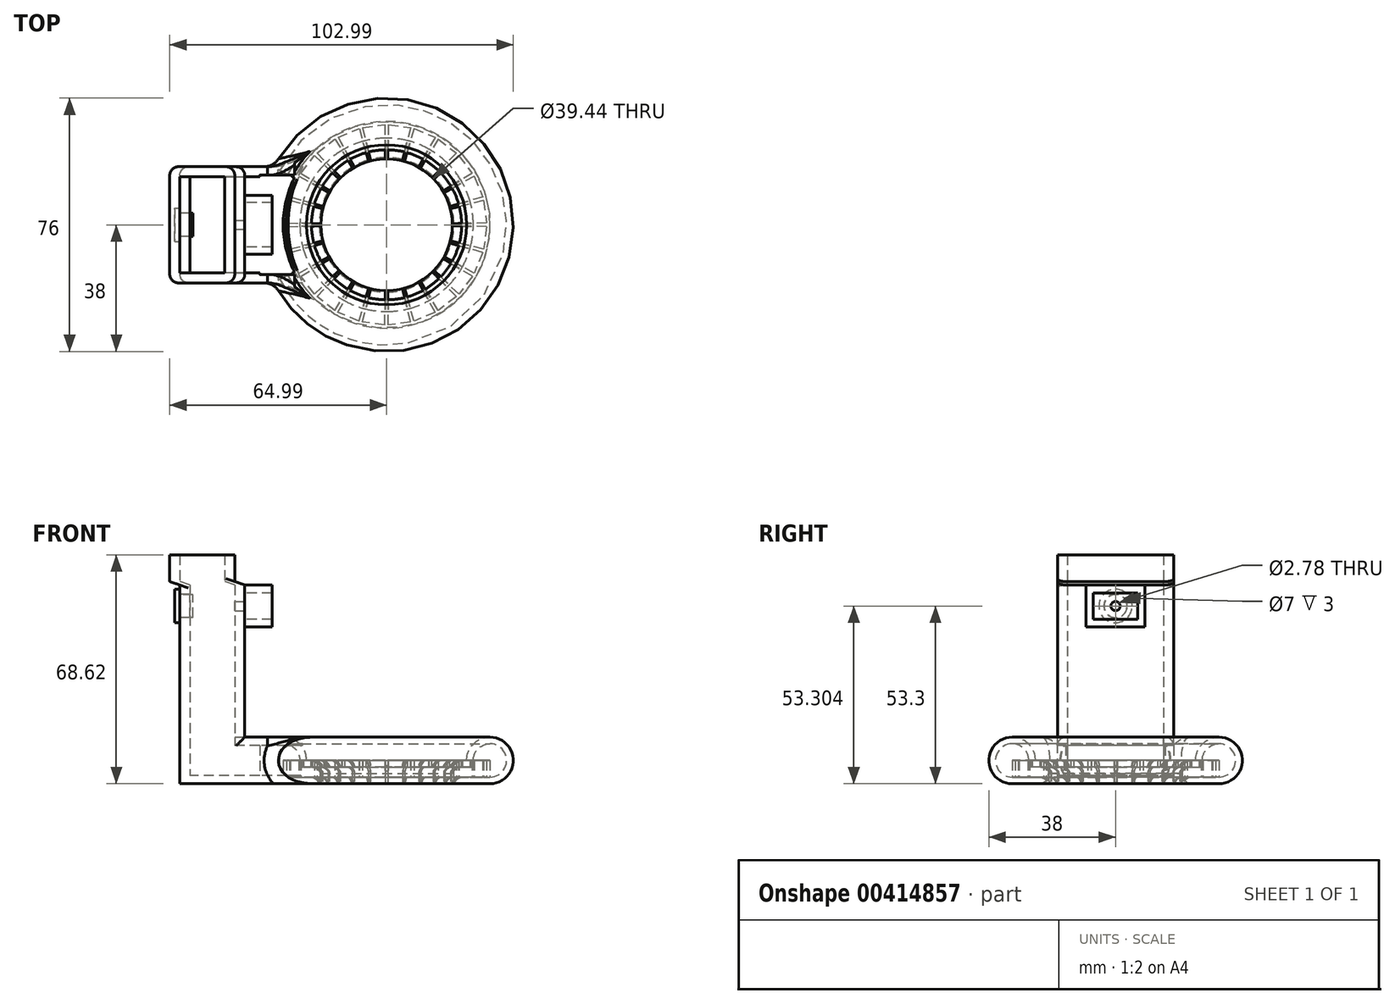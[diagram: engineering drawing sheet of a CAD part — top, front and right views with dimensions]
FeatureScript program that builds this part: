
annotation { "Feature Type Name" : "Feature", "Feature Type Description" : "" }
export const myFeature = defineFeature(function(context is Context, id is Id, definition is map)
    precondition{}
    {
        {
            var Q0;
            Q0=qCreatedBy(makeId("Right.planeOp"),FACE);
            cPlane(context, id + "F0", {"entities" : qUnion([Q0]), "cplaneType" : CPlaneType.OFFSET, "offset" : 42.5 * mm, "oppositeDirection" : true, "width" : 150 * mm, "height" : 150 * mm});
        }
        {
            var Q0;
            Q0=qCreatedBy(makeId("Front.planeOp"),FACE);
            cPlane(context, id + "F1", {"entities" : qUnion([Q0]), "cplaneType" : CPlaneType.OFFSET, "offset" : 17.41 * mm, "width" : 150 * mm, "height" : 150 * mm});
        }
        {
            var Q0;
            Q0=qCreatedBy(makeId("Front.planeOp"),FACE);
            cPlane(context, id + "F2", {"entities" : qUnion([Q0]), "cplaneType" : CPlaneType.OFFSET, "offset" : 17.41 * mm, "oppositeDirection" : true, "width" : 150 * mm, "height" : 150 * mm});
        }
        {
            var Q0;
            Q0=qCreatedBy(makeId("Top.planeOp"),FACE);
            cPlane(context, id + "F3", {"entities" : qUnion([Q0]), "cplaneType" : CPlaneType.OFFSET, "offset" : 7 * mm, "width" : 150 * mm, "height" : 150 * mm});
        }
        {
            var Q0;
            Q0=qCreatedBy(id+"F3.planeOp",FACE);
            cPlane(context, id + "F4", {"entities" : qUnion([Q0]), "cplaneType" : CPlaneType.OFFSET, "offset" : 6.95 * mm, "width" : 150 * mm, "height" : 150 * mm});
        }
        {
            var Q0;
            Q0=qCreatedBy(id+"F3.planeOp",FACE);
            cPlane(context, id + "F5", {"entities" : qUnion([Q0]), "cplaneType" : CPlaneType.OFFSET, "offset" : 52.62 * mm, "width" : 150 * mm, "height" : 150 * mm});
        }
        {
            var Q0;
            Q0=qCreatedBy(makeId("Right.planeOp"),FACE);
            cPlane(context, id + "F6", {"entities" : qUnion([Q0]), "cplaneType" : CPlaneType.OFFSET, "offset" : 62 * mm, "oppositeDirection" : true, "width" : 150 * mm, "height" : 150 * mm});
        }
        {
            var Q0;
            Q0=qCreatedBy(id+"F5.planeOp",FACE);
            cPlane(context, id + "F7", {"entities" : qUnion([Q0]), "cplaneType" : CPlaneType.OFFSET, "offset" : 1 * mm, "width" : 150 * mm, "height" : 150 * mm});
        }
        {
            var Q0;
            Q0=qCreatedBy(makeId("Top.planeOp"),FACE);
            var sketch = newSketch(context, id + "F8", { "sketchPlane" : qUnion([Q0])});
            skCircle(sketch, "E0", {"center": v(-293.13, 11) * mm, "radius": 45 * mm});
            skCircle(sketch, "E1.0", {"center": v(-293.13, 11) * mm, "radius": 38.5 * mm});
            skCircle(sketch, "E2", {"center": v(0, 0) * mm, "radius": 1.25 * mm, "construction": true});
            skLineSegment(sketch, "E3", {"start": v(-292.49, 47.5) * mm, "end": v(-292.6, 41) * mm});
            skLineSegment(sketch, "E4", {"start": v(-284.93, 39.86) * mm, "end": v(-283.16, 46.11) * mm});
            skLineSegment(sketch, "E5", {"start": v(-274.33, 42.29) * mm, "end": v(-277.67, 36.72) * mm});
            skLineSegment(sketch, "E6", {"start": v(-271.5, 31.8) * mm, "end": v(-266.82, 36.3) * mm});
            skLineSegment(sketch, "E7", {"start": v(-266.9, 25.56) * mm, "end": v(-261.21, 28.71) * mm});
            skLineSegment(sketch, "E8", {"start": v(-264.04, 18.33) * mm, "end": v(-257.73, 19.92) * mm});
            skLineSegment(sketch, "E9", {"start": v(-263.13, 10.5) * mm, "end": v(-256.63, 10.38) * mm});
            skLineSegment(sketch, "E10.MirrorCS", {"start": v(-264.3, 2.68) * mm, "end": v(-258.06, 0.88) * mm});
            skLineSegment(sketch, "E11.MirrorCS", {"start": v(-267.4, -4.44) * mm, "end": v(-261.83, -7.78) * mm});
            skLineSegment(sketch, "E12.MirrorCS", {"start": v(-272.22, -10.52) * mm, "end": v(-267.7, -15.18) * mm});
            skLineSegment(sketch, "E13.MirrorCS", {"start": v(-275.4, -20.9) * mm, "end": v(-278.55, -15.23) * mm});
            skLineSegment(sketch, "E14.MirrorCS", {"start": v(-285.92, -18.12) * mm, "end": v(-284.35, -24.43) * mm});
            skLineSegment(sketch, "E15.MirrorCS", {"start": v(-300.3, 40.13) * mm, "end": v(-301.87, 46.44) * mm});
            skLineSegment(sketch, "E16.MirrorCS", {"start": v(-310.82, 42.92) * mm, "end": v(-307.67, 37.25) * mm});
            skLineSegment(sketch, "E17.MirrorCS", {"start": v(-314.01, 32.54) * mm, "end": v(-318.54, 37.2) * mm});
            skLineSegment(sketch, "E18.MirrorCS", {"start": v(-318.83, 26.46) * mm, "end": v(-324.4, 29.81) * mm});
            skLineSegment(sketch, "E19.MirrorCS", {"start": v(-321.94, 19.34) * mm, "end": v(-328.19, 21.15) * mm});
            skLineSegment(sketch, "E20.MirrorCS", {"start": v(-322.22, 3.7) * mm, "end": v(-328.53, 2.11) * mm});
            skLineSegment(sketch, "E21.MirrorCS", {"start": v(-319.37, -3.53) * mm, "end": v(-325.06, -6.68) * mm});
            skLineSegment(sketch, "E22.MirrorCS", {"start": v(-314.77, -9.77) * mm, "end": v(-319.46, -14.28) * mm});
            skLineSegment(sketch, "E23.MirrorCS", {"start": v(-311.95, -20.27) * mm, "end": v(-308.6, -14.7) * mm});
            skLineSegment(sketch, "E24.MirrorCS", {"start": v(-301.35, -17.85) * mm, "end": v(-303.13, -24.1) * mm});
            skLineSegment(sketch, "E25", {"start": v(-293.65, -19) * mm, "end": v(-293.76, -25.5) * mm});
            skLineSegment(sketch, "E26", {"start": v(-323.12, 11.52) * mm, "end": v(-329.62, 11.64) * mm});
            skLineSegment(sketch, "E27", {"start": v(-293.76, 47.5) * mm, "end": v(-293.65, 41) * mm});
            skLineSegment(sketch, "E28", {"start": v(-285.94, 40.13) * mm, "end": v(-284.39, 46.44) * mm});
            skLineSegment(sketch, "E29", {"start": v(-275.43, 42.92) * mm, "end": v(-278.58, 37.25) * mm});
            skLineSegment(sketch, "E30", {"start": v(-272.24, 32.54) * mm, "end": v(-267.72, 37.2) * mm});
            skLineSegment(sketch, "E31", {"start": v(-267.42, 26.46) * mm, "end": v(-261.85, 29.81) * mm});
            skLineSegment(sketch, "E32", {"start": v(-264.3, 19.34) * mm, "end": v(-258.07, 21.15) * mm});
            skLineSegment(sketch, "E33", {"start": v(-263.13, 11.54) * mm, "end": v(-256.63, 11.65) * mm});
            skLineSegment(sketch, "E34.MirrorCS", {"start": v(-264.03, 3.7) * mm, "end": v(-257.73, 2.11) * mm});
            skLineSegment(sketch, "E35.MirrorCS", {"start": v(-266.88, -3.53) * mm, "end": v(-261.2, -6.68) * mm});
            skLineSegment(sketch, "E36.MirrorCS", {"start": v(-271.48, -9.77) * mm, "end": v(-266.8, -14.28) * mm});
            skLineSegment(sketch, "E37.MirrorCS", {"start": v(-274.3, -20.27) * mm, "end": v(-277.65, -14.7) * mm});
            skLineSegment(sketch, "E38.MirrorCS", {"start": v(-284.9, -17.85) * mm, "end": v(-283.12, -24.1) * mm});
            skLineSegment(sketch, "E39.MirrorCS", {"start": v(-301.32, 39.86) * mm, "end": v(-303.1, 46.11) * mm});
            skLineSegment(sketch, "E40.MirrorCS", {"start": v(-311.93, 42.29) * mm, "end": v(-308.58, 36.72) * mm});
            skLineSegment(sketch, "E41.MirrorCS", {"start": v(-314.75, 31.8) * mm, "end": v(-319.44, 36.3) * mm});
            skLineSegment(sketch, "E42.MirrorCS", {"start": v(-319.36, 25.56) * mm, "end": v(-325.04, 28.71) * mm});
            skLineSegment(sketch, "E43.MirrorCS", {"start": v(-322.22, 18.33) * mm, "end": v(-328.52, 19.92) * mm});
            skLineSegment(sketch, "E44.MirrorCS", {"start": v(-321.95, 2.68) * mm, "end": v(-328.2, 0.88) * mm});
            skLineSegment(sketch, "E45.MirrorCS", {"start": v(-318.85, -4.44) * mm, "end": v(-324.42, -7.78) * mm});
            skLineSegment(sketch, "E46.MirrorCS", {"start": v(-314.03, -10.52) * mm, "end": v(-318.56, -15.18) * mm});
            skLineSegment(sketch, "E47.MirrorCS", {"start": v(-310.85, -20.9) * mm, "end": v(-307.7, -15.23) * mm});
            skLineSegment(sketch, "E48.MirrorCS", {"start": v(-300.34, -18.12) * mm, "end": v(-301.9, -24.43) * mm});
            skLineSegment(sketch, "E49", {"start": v(-292.6, -19) * mm, "end": v(-292.49, -25.5) * mm});
            skLineSegment(sketch, "E50", {"start": v(-323.12, 10.48) * mm, "end": v(-329.62, 10.36) * mm});
            skCircle(sketch, "E51", {"center": v(-293.13, 11) * mm, "radius": 1.25 * mm, "construction": true});
            skLineSegment(sketch, "E52", {"start": v(-322.22, 18.33) * mm, "end": v(-321.94, 19.34) * mm});
            skLineSegment(sketch, "E53", {"start": v(-321.94, 19.34) * mm, "end": v(-319.36, 25.56) * mm});
            skLineSegment(sketch, "E54", {"start": v(-319.36, 25.56) * mm, "end": v(-318.83, 26.46) * mm});
            skLineSegment(sketch, "E55", {"start": v(-318.83, 26.46) * mm, "end": v(-314.75, 31.8) * mm});
            skLineSegment(sketch, "E56", {"start": v(-314.75, 31.8) * mm, "end": v(-314.01, 32.54) * mm});
            skLineSegment(sketch, "E57", {"start": v(-314.01, 32.54) * mm, "end": v(-308.58, 36.72) * mm});
            skLineSegment(sketch, "E58", {"start": v(-308.58, 36.72) * mm, "end": v(-307.67, 37.25) * mm});
            skLineSegment(sketch, "E59", {"start": v(-307.67, 37.25) * mm, "end": v(-301.32, 39.86) * mm});
            skLineSegment(sketch, "E60", {"start": v(-301.32, 39.86) * mm, "end": v(-300.3, 40.13) * mm});
            skLineSegment(sketch, "E61", {"start": v(-300.3, 40.13) * mm, "end": v(-293.65, 41) * mm});
            skLineSegment(sketch, "E62", {"start": v(-293.65, 41) * mm, "end": v(-292.6, 41) * mm});
            skLineSegment(sketch, "E63", {"start": v(-292.6, 41) * mm, "end": v(-285.94, 40.13) * mm});
            skLineSegment(sketch, "E64", {"start": v(-285.94, 40.13) * mm, "end": v(-284.93, 39.86) * mm});
            skLineSegment(sketch, "E65", {"start": v(-284.93, 39.86) * mm, "end": v(-278.58, 37.25) * mm});
            skLineSegment(sketch, "E66", {"start": v(-278.58, 37.25) * mm, "end": v(-277.67, 36.72) * mm});
            skLineSegment(sketch, "E67", {"start": v(-277.67, 36.72) * mm, "end": v(-272.24, 32.54) * mm});
            skLineSegment(sketch, "E68", {"start": v(-272.24, 32.54) * mm, "end": v(-271.5, 31.8) * mm});
            skLineSegment(sketch, "E69", {"start": v(-271.5, 31.8) * mm, "end": v(-267.42, 26.46) * mm});
            skLineSegment(sketch, "E70", {"start": v(-267.42, 26.46) * mm, "end": v(-266.9, 25.56) * mm});
            skLineSegment(sketch, "E71", {"start": v(-266.9, 25.56) * mm, "end": v(-264.3, 19.34) * mm});
            skLineSegment(sketch, "E72", {"start": v(-264.3, 19.34) * mm, "end": v(-264.04, 18.33) * mm});
            skLineSegment(sketch, "E73", {"start": v(-264.04, 18.33) * mm, "end": v(-263.13, 11.54) * mm});
            skLineSegment(sketch, "E74", {"start": v(-263.13, 11.54) * mm, "end": v(-263.13, 10.5) * mm});
            skLineSegment(sketch, "E75", {"start": v(-263.13, 10.5) * mm, "end": v(-264.03, 3.7) * mm});
            skLineSegment(sketch, "E76", {"start": v(-264.03, 3.7) * mm, "end": v(-264.3, 2.68) * mm});
            skLineSegment(sketch, "E77", {"start": v(-264.3, 2.68) * mm, "end": v(-266.88, -3.53) * mm});
            skLineSegment(sketch, "E78", {"start": v(-266.88, -3.53) * mm, "end": v(-267.4, -4.44) * mm});
            skLineSegment(sketch, "E79", {"start": v(-267.4, -4.44) * mm, "end": v(-271.48, -9.77) * mm});
            skLineSegment(sketch, "E80", {"start": v(-271.48, -9.77) * mm, "end": v(-272.22, -10.52) * mm});
            skLineSegment(sketch, "E81", {"start": v(-272.22, -10.52) * mm, "end": v(-277.65, -14.7) * mm});
            skLineSegment(sketch, "E82", {"start": v(-277.65, -14.7) * mm, "end": v(-278.55, -15.23) * mm});
            skLineSegment(sketch, "E83", {"start": v(-278.55, -15.23) * mm, "end": v(-284.9, -17.85) * mm});
            skLineSegment(sketch, "E84", {"start": v(-284.9, -17.85) * mm, "end": v(-285.92, -18.12) * mm});
            skLineSegment(sketch, "E85", {"start": v(-285.92, -18.12) * mm, "end": v(-292.6, -19) * mm});
            skLineSegment(sketch, "E86", {"start": v(-292.6, -19) * mm, "end": v(-293.65, -19) * mm});
            skLineSegment(sketch, "E87", {"start": v(-293.65, -19) * mm, "end": v(-300.34, -18.12) * mm});
            skLineSegment(sketch, "E88", {"start": v(-300.34, -18.12) * mm, "end": v(-301.35, -17.85) * mm});
            skLineSegment(sketch, "E89", {"start": v(-301.35, -17.85) * mm, "end": v(-307.7, -15.23) * mm});
            skLineSegment(sketch, "E90", {"start": v(-307.7, -15.23) * mm, "end": v(-308.6, -14.7) * mm});
            skLineSegment(sketch, "E91", {"start": v(-308.6, -14.7) * mm, "end": v(-314.03, -10.52) * mm});
            skLineSegment(sketch, "E92", {"start": v(-314.03, -10.52) * mm, "end": v(-314.77, -9.77) * mm});
            skLineSegment(sketch, "E93", {"start": v(-314.77, -9.77) * mm, "end": v(-318.85, -4.44) * mm});
            skLineSegment(sketch, "E94", {"start": v(-318.85, -4.44) * mm, "end": v(-319.37, -3.53) * mm});
            skLineSegment(sketch, "E95", {"start": v(-321.95, 2.68) * mm, "end": v(-322.22, 3.7) * mm});
            skLineSegment(sketch, "E96", {"start": v(-319.37, -3.53) * mm, "end": v(-321.95, 2.68) * mm});
            skLineSegment(sketch, "E97", {"start": v(-322.22, 3.7) * mm, "end": v(-323.12, 10.48) * mm});
            skLineSegment(sketch, "E98", {"start": v(-323.12, 10.48) * mm, "end": v(-323.12, 11.52) * mm});
            skLineSegment(sketch, "E99", {"start": v(-323.12, 11.52) * mm, "end": v(-322.22, 18.33) * mm});
            skLineSegment(sketch, "E100", {"start": v(-329.62, 11.64) * mm, "end": v(-328.52, 19.92) * mm});
            skLineSegment(sketch, "E101", {"start": v(-328.19, 21.15) * mm, "end": v(-325.04, 28.71) * mm});
            skLineSegment(sketch, "E102", {"start": v(-324.4, 29.81) * mm, "end": v(-319.44, 36.3) * mm});
            skLineSegment(sketch, "E103", {"start": v(-318.54, 37.2) * mm, "end": v(-311.93, 42.29) * mm});
            skLineSegment(sketch, "E104", {"start": v(-310.82, 42.92) * mm, "end": v(-303.1, 46.11) * mm});
            skLineSegment(sketch, "E105", {"start": v(-301.87, 46.44) * mm, "end": v(-293.76, 47.5) * mm});
            skLineSegment(sketch, "E106", {"start": v(-292.49, 47.5) * mm, "end": v(-284.39, 46.44) * mm});
            skLineSegment(sketch, "E107", {"start": v(-283.16, 46.11) * mm, "end": v(-275.43, 42.92) * mm});
            skLineSegment(sketch, "E108", {"start": v(-274.33, 42.29) * mm, "end": v(-267.72, 37.2) * mm});
            skLineSegment(sketch, "E109", {"start": v(-266.82, 36.3) * mm, "end": v(-261.85, 29.81) * mm});
            skLineSegment(sketch, "E110", {"start": v(-261.21, 28.71) * mm, "end": v(-258.07, 21.15) * mm});
            skLineSegment(sketch, "E111", {"start": v(-257.73, 19.92) * mm, "end": v(-256.63, 11.65) * mm});
            skLineSegment(sketch, "E112", {"start": v(-256.63, 10.38) * mm, "end": v(-257.73, 2.11) * mm});
            skLineSegment(sketch, "E113", {"start": v(-258.06, 0.88) * mm, "end": v(-261.2, -6.68) * mm});
            skLineSegment(sketch, "E114", {"start": v(-261.83, -7.78) * mm, "end": v(-266.8, -14.28) * mm});
            skLineSegment(sketch, "E115", {"start": v(-267.7, -15.18) * mm, "end": v(-274.3, -20.27) * mm});
            skLineSegment(sketch, "E116", {"start": v(-275.4, -20.9) * mm, "end": v(-283.12, -24.1) * mm});
            skLineSegment(sketch, "E117", {"start": v(-284.35, -24.43) * mm, "end": v(-292.49, -25.5) * mm});
            skLineSegment(sketch, "E118", {"start": v(-293.76, -25.5) * mm, "end": v(-301.9, -24.43) * mm});
            skLineSegment(sketch, "E119", {"start": v(-303.13, -24.1) * mm, "end": v(-310.85, -20.9) * mm});
            skLineSegment(sketch, "E120", {"start": v(-311.95, -20.27) * mm, "end": v(-318.56, -15.18) * mm});
            skLineSegment(sketch, "E121", {"start": v(-319.46, -14.28) * mm, "end": v(-324.42, -7.78) * mm});
            skLineSegment(sketch, "E122", {"start": v(-325.06, -6.68) * mm, "end": v(-328.2, 0.88) * mm});
            skLineSegment(sketch, "E123", {"start": v(-328.53, 2.11) * mm, "end": v(-329.62, 10.36) * mm});
            skCircle(sketch, "E124", {"center": v(0, 0) * mm, "radius": 20 * mm});
            skLineSegment(sketch, "E125", {"start": v(8.2, 28.86) * mm, "end": v(5.46, 19.24) * mm});
            skLineSegment(sketch, "E126", {"start": v(15.46, 25.72) * mm, "end": v(10.3, 17.15) * mm});
            skLineSegment(sketch, "E127", {"start": v(21.62, 20.8) * mm, "end": v(14.41, 13.87) * mm});
            skLineSegment(sketch, "E128", {"start": v(26.23, 14.56) * mm, "end": v(17.49, 9.7) * mm});
            skLineSegment(sketch, "E129", {"start": v(29.1, 7.33) * mm, "end": v(19.4, 4.9) * mm});
            skLineSegment(sketch, "E130", {"start": v(30, -0.5) * mm, "end": v(20, -0.34) * mm});
            skLineSegment(sketch, "E131", {"start": v(28.82, -8.32) * mm, "end": v(19.22, -5.54) * mm});
            skLineSegment(sketch, "E132", {"start": v(25.72, -15.44) * mm, "end": v(17.15, -10.29) * mm});
            skLineSegment(sketch, "E133", {"start": v(20.9, -21.52) * mm, "end": v(13.94, -14.34) * mm});
            skLineSegment(sketch, "E134", {"start": v(14.57, -26.23) * mm, "end": v(9.72, -17.48) * mm});
            skLineSegment(sketch, "E135", {"start": v(7.21, -29.12) * mm, "end": v(4.81, -19.41) * mm});
            skLineSegment(sketch, "E136", {"start": v(-0.52, -30) * mm, "end": v(-0.35, -20) * mm});
            skLineSegment(sketch, "E137.MirrorCS", {"start": v(-7.18, 29.13) * mm, "end": v(-4.78, 19.42) * mm});
            skLineSegment(sketch, "E138.MirrorCS", {"start": v(-14.55, 26.25) * mm, "end": v(-9.7, 17.5) * mm});
            skLineSegment(sketch, "E139.MirrorCS", {"start": v(-20.88, 21.54) * mm, "end": v(-13.92, 14.36) * mm});
            skLineSegment(sketch, "E140.MirrorCS", {"start": v(-25.7, 15.46) * mm, "end": v(-17.14, 10.31) * mm});
            skLineSegment(sketch, "E141.MirrorCS", {"start": v(-28.82, 8.34) * mm, "end": v(-19.2, 5.57) * mm});
            skLineSegment(sketch, "E142.MirrorCS", {"start": v(-29.1, -7.3) * mm, "end": v(-19.4, -4.87) * mm});
            skLineSegment(sketch, "E143.MirrorCS", {"start": v(-26.25, -14.53) * mm, "end": v(-17.5, -9.68) * mm});
            skLineSegment(sketch, "E144.MirrorCS", {"start": v(-21.64, -20.77) * mm, "end": v(-14.43, -13.85) * mm});
            skLineSegment(sketch, "E145.MirrorCS", {"start": v(-15.48, -25.7) * mm, "end": v(-10.32, -17.13) * mm});
            skLineSegment(sketch, "E146.MirrorCS", {"start": v(-8.22, -28.85) * mm, "end": v(-5.49, -19.23) * mm});
            skLineSegment(sketch, "E147", {"start": v(-30, 0.52) * mm, "end": v(-20, 0.35) * mm});
            skLineSegment(sketch, "E148", {"start": v(0.52, 30) * mm, "end": v(0.35, 20) * mm});
            skLineSegment(sketch, "E149", {"start": v(7.18, 29.13) * mm, "end": v(4.78, 19.42) * mm});
            skLineSegment(sketch, "E150", {"start": v(14.55, 26.25) * mm, "end": v(9.7, 17.5) * mm});
            skLineSegment(sketch, "E151", {"start": v(20.88, 21.54) * mm, "end": v(13.92, 14.36) * mm});
            skLineSegment(sketch, "E152", {"start": v(25.7, 15.46) * mm, "end": v(17.14, 10.31) * mm});
            skLineSegment(sketch, "E153", {"start": v(28.82, 8.34) * mm, "end": v(19.2, 5.57) * mm});
            skLineSegment(sketch, "E154", {"start": v(30, 0.54) * mm, "end": v(20, 0.36) * mm});
            skLineSegment(sketch, "E155", {"start": v(29.1, -7.3) * mm, "end": v(19.4, -4.87) * mm});
            skLineSegment(sketch, "E156", {"start": v(26.25, -14.53) * mm, "end": v(17.5, -9.68) * mm});
            skLineSegment(sketch, "E157", {"start": v(21.64, -20.77) * mm, "end": v(14.43, -13.85) * mm});
            skLineSegment(sketch, "E158", {"start": v(15.48, -25.7) * mm, "end": v(10.32, -17.13) * mm});
            skLineSegment(sketch, "E159", {"start": v(8.22, -28.85) * mm, "end": v(5.49, -19.23) * mm});
            skLineSegment(sketch, "E160", {"start": v(0.52, -30) * mm, "end": v(0.35, -20) * mm});
            skLineSegment(sketch, "E161.MirrorCS", {"start": v(-8.2, 28.86) * mm, "end": v(-5.46, 19.24) * mm});
            skLineSegment(sketch, "E162.MirrorCS", {"start": v(-15.46, 25.72) * mm, "end": v(-10.3, 17.15) * mm});
            skLineSegment(sketch, "E163.MirrorCS", {"start": v(-21.62, 20.8) * mm, "end": v(-14.41, 13.87) * mm});
            skLineSegment(sketch, "E164.MirrorCS", {"start": v(-26.23, 14.56) * mm, "end": v(-17.49, 9.7) * mm});
            skLineSegment(sketch, "E165.MirrorCS", {"start": v(-29.1, 7.33) * mm, "end": v(-19.4, 4.9) * mm});
            skLineSegment(sketch, "E166.MirrorCS", {"start": v(-28.82, -8.32) * mm, "end": v(-19.22, -5.54) * mm});
            skLineSegment(sketch, "E167.MirrorCS", {"start": v(-25.72, -15.44) * mm, "end": v(-17.15, -10.29) * mm});
            skLineSegment(sketch, "E168.MirrorCS", {"start": v(-20.9, -21.52) * mm, "end": v(-13.94, -14.34) * mm});
            skLineSegment(sketch, "E169.MirrorCS", {"start": v(-14.57, -26.23) * mm, "end": v(-9.72, -17.48) * mm});
            skLineSegment(sketch, "E170.MirrorCS", {"start": v(-7.21, -29.12) * mm, "end": v(-4.81, -19.41) * mm});
            skLineSegment(sketch, "E171", {"start": v(-30, -0.52) * mm, "end": v(-20, -0.35) * mm});
            skLineSegment(sketch, "E172", {"start": v(-0.52, 30) * mm, "end": v(-0.35, 20) * mm});
            skLineSegment(sketch, "E173", {"start": v(-14.55, 26.25) * mm, "end": v(-8.2, 28.86) * mm});
            skLineSegment(sketch, "E174", {"start": v(-7.18, 29.13) * mm, "end": v(-0.52, 30) * mm});
            skLineSegment(sketch, "E175", {"start": v(0.52, 30) * mm, "end": v(7.18, 29.13) * mm});
            skLineSegment(sketch, "E176", {"start": v(8.2, 28.86) * mm, "end": v(14.55, 26.25) * mm});
            skLineSegment(sketch, "E177", {"start": v(15.46, 25.72) * mm, "end": v(20.88, 21.54) * mm});
            skLineSegment(sketch, "E178", {"start": v(21.62, 20.8) * mm, "end": v(25.7, 15.46) * mm});
            skLineSegment(sketch, "E179", {"start": v(26.23, 14.56) * mm, "end": v(28.82, 8.34) * mm});
            skLineSegment(sketch, "E180", {"start": v(29.1, 7.33) * mm, "end": v(30, 0.54) * mm});
            skLineSegment(sketch, "E181", {"start": v(30, -0.5) * mm, "end": v(29.1, -7.3) * mm});
            skLineSegment(sketch, "E182", {"start": v(28.82, -8.32) * mm, "end": v(26.25, -14.53) * mm});
            skLineSegment(sketch, "E183", {"start": v(25.72, -15.44) * mm, "end": v(21.64, -20.77) * mm});
            skLineSegment(sketch, "E184", {"start": v(20.9, -21.52) * mm, "end": v(15.48, -25.7) * mm});
            skLineSegment(sketch, "E185", {"start": v(14.57, -26.23) * mm, "end": v(8.22, -28.85) * mm});
            skLineSegment(sketch, "E186", {"start": v(7.21, -29.12) * mm, "end": v(0.52, -30) * mm});
            skLineSegment(sketch, "E187", {"start": v(-0.52, -30) * mm, "end": v(-7.21, -29.12) * mm});
            skLineSegment(sketch, "E188", {"start": v(-8.22, -28.85) * mm, "end": v(-14.57, -26.23) * mm});
            skLineSegment(sketch, "E189", {"start": v(-15.48, -25.7) * mm, "end": v(-20.9, -21.52) * mm});
            skLineSegment(sketch, "E190", {"start": v(-21.64, -20.77) * mm, "end": v(-25.72, -15.44) * mm});
            skLineSegment(sketch, "E191", {"start": v(-26.25, -14.53) * mm, "end": v(-28.82, -8.32) * mm});
            skLineSegment(sketch, "E192", {"start": v(-29.1, -7.3) * mm, "end": v(-30, -0.52) * mm});
            skLineSegment(sketch, "E193", {"start": v(-28.82, 8.34) * mm, "end": v(-26.23, 14.56) * mm});
            skLineSegment(sketch, "E194", {"start": v(-25.7, 15.46) * mm, "end": v(-21.62, 20.8) * mm});
            skLineSegment(sketch, "E195", {"start": v(-30, 0.52) * mm, "end": v(-29.1, 7.33) * mm});
            skLineSegment(sketch, "E196", {"start": v(-20.88, 21.54) * mm, "end": v(-15.46, 25.72) * mm});
            skCircle(sketch, "E197", {"center": v(0, 0) * mm, "radius": 31 * mm});
            skCircle(sketch, "E198", {"center": v(0, 0) * mm, "radius": 37.5 * mm});
            skSolve(sketch);
        }
        {
            var Q0;
            Q0=qCreatedBy(makeId("Front.planeOp"),FACE);
            var sketch = newSketch(context, id + "F9", { "sketchPlane" : qUnion([Q0])});
            skLineSegment(sketch, "E199.top", {"start": v(38.5, -7) * mm, "end": v(-38.5, -7) * mm, "construction": true});
            skLineSegment(sketch, "E199.left", {"start": v(31, 7) * mm, "end": v(31, -7) * mm, "construction": true});
            skPoint(sketch, "E199.middle", {"position": v(0, 0) * mm});
            skLineSegment(sketch, "E200", {"start": v(-38.5, 0) * mm, "end": v(38.5, 0) * mm, "construction": true});
            skArc(sketch, "E201", {"start": v(31, 0) * mm, "mid": v(35.95, 11.95) * mm, "end": v(24, 7) * mm});
            skArc(sketch, "E202", {"start": v(31, 2) * mm, "mid": v(34.53, 10.54) * mm, "end": v(26, 7) * mm});
            skLineSegment(sketch, "E203", {"start": v(31, 2) * mm, "end": v(31, 0) * mm});
            skLineSegment(sketch, "E204", {"start": v(31, 2) * mm, "end": v(24, 2) * mm, "construction": true});
            skLineSegment(sketch, "E205", {"start": v(24, 2) * mm, "end": v(24, 0) * mm, "construction": true});
            skLineSegment(sketch, "E206", {"start": v(22.5, 0) * mm, "end": v(22.5, 7) * mm, "construction": true});
            skLineSegment(sketch, "E207", {"start": v(24, 7) * mm, "end": v(22.5, 7) * mm});
            skLineSegment(sketch, "E208", {"start": v(30, 7) * mm, "end": v(30, 5) * mm});
            skLineSegment(sketch, "E209", {"start": v(22.5, 5) * mm, "end": v(26, 5) * mm});
            skLineSegment(sketch, "E210", {"start": v(26, 5) * mm, "end": v(26, 7) * mm});
            skLineSegment(sketch, "E211", {"start": v(0, -7) * mm, "end": v(0, 7) * mm, "construction": true});
            skLineSegment(sketch, "E212", {"start": v(31, 7) * mm, "end": v(31, 14) * mm, "construction": true});
            skLineSegment(sketch, "E213", {"start": v(31, 7) * mm, "end": v(38, 7) * mm, "construction": true});
            skLineSegment(sketch, "E214", {"start": v(31, 12) * mm, "end": v(31, 14) * mm});
            skLineSegment(sketch, "E215", {"start": v(36, 7) * mm, "end": v(38, 7) * mm});
            skLineSegment(sketch, "E216.MirrorCS", {"start": v(-31, 2) * mm, "end": v(-31, 0) * mm});
            skLineSegment(sketch, "E217.MirrorCS", {"start": v(-30, 7) * mm, "end": v(-30, 5) * mm});
            skLineSegment(sketch, "E218.MirrorCS", {"start": v(-24, 7) * mm, "end": v(-22.5, 7) * mm});
            skLineSegment(sketch, "E219.MirrorCS", {"start": v(-26, 5) * mm, "end": v(-26, 7) * mm});
            skLineSegment(sketch, "E220.MirrorCS", {"start": v(-36, 7) * mm, "end": v(-38, 7) * mm});
            skLineSegment(sketch, "E221.MirrorCS", {"start": v(-22.5, 5) * mm, "end": v(-26, 5) * mm});
            skLineSegment(sketch, "E222.MirrorCS", {"start": v(-24, 2) * mm, "end": v(-24, 0) * mm, "construction": true});
            skLineSegment(sketch, "E223.MirrorCS", {"start": v(-31, 12) * mm, "end": v(-31, 14) * mm});
            skLineSegment(sketch, "E224.MirrorCS", {"start": v(-31, 7) * mm, "end": v(-38, 7) * mm, "construction": true});
            skLineSegment(sketch, "E225.MirrorCS", {"start": v(-31, 2) * mm, "end": v(-24, 2) * mm, "construction": true});
            skLineSegment(sketch, "E226.MirrorCS", {"start": v(-31, 7) * mm, "end": v(-31, -7) * mm, "construction": true});
            skLineSegment(sketch, "E227.MirrorCS", {"start": v(-31, 7) * mm, "end": v(-31, 14) * mm, "construction": true});
            skArc(sketch, "E228.MirrorCS", {"start": v(-31, 0) * mm, "mid": v(-35.95, 11.95) * mm, "end": v(-24, 7) * mm});
            skArc(sketch, "E229.MirrorCS", {"start": v(-31, 2) * mm, "mid": v(-34.54, 10.54) * mm, "end": v(-26, 7) * mm});
            skLineSegment(sketch, "E230.MirrorCS", {"start": v(-22.5, 0) * mm, "end": v(-22.5, 7) * mm, "construction": true});
            skLineSegment(sketch, "E231", {"start": v(-22.5, 5) * mm, "end": v(-15.5, 5) * mm});
            skArc(sketch, "E232.MirrorCS", {"start": v(-17.5, 7) * mm, "mid": v(-16.08, 6.41) * mm, "end": v(-15.5, 5) * mm});
            skLineSegment(sketch, "E233", {"start": v(-22.5, 7) * mm, "end": v(-17.5, 7) * mm});
            skLineSegment(sketch, "E234", {"start": v(22.5, 5) * mm, "end": v(-22.5, 5) * mm, "construction": true});
            skArc(sketch, "E235", {"start": v(22.5, 7) * mm, "mid": v(20.94, 6.23) * mm, "end": v(19.72, 5) * mm});
            skLineSegment(sketch, "E236", {"start": v(24, 2) * mm, "end": v(-24, 2) * mm, "construction": true});
            skLineSegment(sketch, "E237", {"start": v(19.72, 5) * mm, "end": v(19.72, 0) * mm, "construction": true});
            skArc(sketch, "E238", {"start": v(22.5, 5) * mm, "mid": v(20.83, 4.5) * mm, "end": v(19.72, 3.15) * mm});
            skLineSegment(sketch, "E239", {"start": v(19.72, 5) * mm, "end": v(19.72, 3.15) * mm});
            skSolve(sketch);
        }
        {
            var Q0;
            Q0=qCreatedBy(id+"F0.planeOp",FACE);
            var sketch = newSketch(context, id + "F10", { "sketchPlane" : qUnion([Q0])});
            skLineSegment(sketch, "E240.bottom", {"start": v(45.5, 14) * mm, "end": v(-45.5, 14) * mm, "construction": true});
            skLineSegment(sketch, "E240.top", {"start": v(45.5, -14) * mm, "end": v(-45.5, -14) * mm, "construction": true});
            skLineSegment(sketch, "E240.left", {"start": v(45.5, 14) * mm, "end": v(45.5, -14) * mm, "construction": true});
            skLineSegment(sketch, "E240.right", {"start": v(-45.5, 14) * mm, "end": v(-45.5, -14) * mm, "construction": true});
            skPoint(sketch, "E240.middle", {"position": v(0, 0) * mm});
            skLineSegment(sketch, "E241", {"start": v(-45.5, 0) * mm, "end": v(45.5, 0) * mm, "construction": true});
            skLineSegment(sketch, "E242", {"start": v(0, 14) * mm, "end": v(0, -14) * mm, "construction": true});
            skLineSegment(sketch, "E243.0", {"start": v(-17.41, 14) * mm, "end": v(-17.41, -14) * mm, "construction": true});
            skLineSegment(sketch, "E244.MirrorCS", {"start": v(17.41, 14) * mm, "end": v(17.41, -14) * mm, "construction": true});
            skLineSegment(sketch, "E245.0", {"start": v(45.5, 7) * mm, "end": v(-45.5, 7) * mm, "construction": true});
            skLineSegment(sketch, "E246", {"start": v(-17.41, 14) * mm, "end": v(-17.41, 7) * mm});
            skLineSegment(sketch, "E247", {"start": v(-17.41, 7) * mm, "end": v(17.41, 7) * mm});
            skLineSegment(sketch, "E248", {"start": v(17.41, 7) * mm, "end": v(17.41, 14) * mm});
            skLineSegment(sketch, "E249", {"start": v(17.41, 14) * mm, "end": v(-17.41, 14) * mm});
            skLineSegment(sketch, "E250.0", {"start": v(45.5, 12) * mm, "end": v(-45.5, 12) * mm, "construction": true});
            skLineSegment(sketch, "E251.0", {"start": v(-14.73, 14) * mm, "end": v(-14.73, -14) * mm, "construction": true});
            skLineSegment(sketch, "E252.MirrorCS", {"start": v(14.73, 14) * mm, "end": v(14.73, -14) * mm, "construction": true});
            skLineSegment(sketch, "E253", {"start": v(-14.73, 7) * mm, "end": v(-14.73, 14) * mm});
            skLineSegment(sketch, "E254", {"start": v(14.73, 7) * mm, "end": v(14.73, 14) * mm});
            skLineSegment(sketch, "E255", {"start": v(17.41, 12) * mm, "end": v(-17.41, 12) * mm});
            skPoint(sketch, "E255.startSnap0", {"position": v(17.41, 10.5) * mm});
            skLineSegment(sketch, "E256", {"start": v(-6.63, 57.23) * mm, "end": v(6.63, 57.23) * mm});
            skLineSegment(sketch, "E257", {"start": v(-8.8, 47.05) * mm, "end": v(-8.8, 59.63) * mm});
            skLineSegment(sketch, "E258.MirrorCS", {"start": v(8.8, 47.05) * mm, "end": v(8.8, 59.63) * mm});
            skLineSegment(sketch, "E259", {"start": v(-8.8, 59.63) * mm, "end": v(8.8, 59.63) * mm});
            skLineSegment(sketch, "E260", {"start": v(-6.63, 57.23) * mm, "end": v(-8.8, 57.23) * mm});
            skLineSegment(sketch, "E261", {"start": v(6.63, 57.23) * mm, "end": v(8.8, 57.23) * mm});
            skLineSegment(sketch, "E262", {"start": v(-8.8, 47.05) * mm, "end": v(8.8, 47.05) * mm});
            skCircle(sketch, "E263", {"center": v(0, 0) * mm, "radius": 1.5 * mm, "construction": true});
            skCircle(sketch, "E264", {"center": v(0, 53.3) * mm, "radius": 1.39 * mm});
            skCircle(sketch, "E265", {"center": v(0, 53.3) * mm, "radius": 1.25 * mm, "construction": true});
            skLineSegment(sketch, "E266", {"start": v(14.73, 14) * mm, "end": v(14.73, 52.5) * mm});
            skLineSegment(sketch, "E267", {"start": v(0, 58.3) * mm, "end": v(0, 16.5) * mm, "construction": true});
            skLineSegment(sketch, "E268.MirrorCS", {"start": v(-14.73, 14) * mm, "end": v(-14.73, 52.5) * mm});
            skLineSegment(sketch, "E269", {"start": v(17.41, 14) * mm, "end": v(17.41, 52.5) * mm});
            skLineSegment(sketch, "E270", {"start": v(-17.41, 14) * mm, "end": v(-17.41, 52.5) * mm});
            skLineSegment(sketch, "E271", {"start": v(-8.8, 59.63) * mm, "end": v(-17.41, 59.63) * mm});
            skLineSegment(sketch, "E272", {"start": v(8.8, 59.63) * mm, "end": v(17.41, 59.63) * mm});
            skLineSegment(sketch, "E273", {"start": v(17.41, 50) * mm, "end": v(17.41, 59.63) * mm});
            skLineSegment(sketch, "E274", {"start": v(14.73, 50) * mm, "end": v(14.73, 59.63) * mm});
            skLineSegment(sketch, "E275", {"start": v(-14.73, 50) * mm, "end": v(-14.73, 59.63) * mm});
            skLineSegment(sketch, "E276", {"start": v(-17.41, 50) * mm, "end": v(-17.41, 59.63) * mm});
            skLineSegment(sketch, "E277", {"start": v(0, 53.3) * mm, "end": v(8.8, 53.3) * mm, "construction": true});
            skLineSegment(sketch, "E278.MirrorCS", {"start": v(-6.63, 49.38) * mm, "end": v(6.63, 49.38) * mm});
            skLineSegment(sketch, "E279", {"start": v(-6.63, 57.23) * mm, "end": v(-6.63, 49.38) * mm});
            skLineSegment(sketch, "E280", {"start": v(6.63, 57.23) * mm, "end": v(6.63, 49.38) * mm});
            skSolve(sketch);
        }
        {
            var Q0;
            Q0=qCreatedBy(id+"F1.planeOp",FACE);
            var sketch = newSketch(context, id + "F11", { "sketchPlane" : qUnion([Q0])});
            skLineSegment(sketch, "E281.top", {"start": v(45.5, -14) * mm, "end": v(-45.5, -14) * mm, "construction": true});
            skLineSegment(sketch, "E281.left", {"start": v(45.5, 14) * mm, "end": v(45.5, -14) * mm, "construction": true});
            skLineSegment(sketch, "E281.right", {"start": v(-45.5, 14) * mm, "end": v(-45.5, -14) * mm, "construction": true});
            skPoint(sketch, "E281.middle", {"position": v(0, 0) * mm});
            skLineSegment(sketch, "E282", {"start": v(0, 14) * mm, "end": v(0, -14) * mm, "construction": true});
            skLineSegment(sketch, "E283.0", {"start": v(-17.41, 14) * mm, "end": v(-17.41, -14) * mm, "construction": true});
            skLineSegment(sketch, "E284.MirrorCS", {"start": v(17.41, 14) * mm, "end": v(17.41, -14) * mm, "construction": true});
            skLineSegment(sketch, "E285", {"start": v(-17.41, 14) * mm, "end": v(-17.41, 7) * mm});
            skLineSegment(sketch, "E286", {"start": v(-17.41, 7) * mm, "end": v(17.41, 7) * mm});
            skLineSegment(sketch, "E287", {"start": v(17.41, 7) * mm, "end": v(17.41, 14) * mm});
            skLineSegment(sketch, "E288", {"start": v(17.41, 14) * mm, "end": v(-17.41, 14) * mm});
            skLineSegment(sketch, "E289.0", {"start": v(-14.73, 14) * mm, "end": v(-14.73, -14) * mm, "construction": true});
            skLineSegment(sketch, "E290.MirrorCS", {"start": v(14.73, 14) * mm, "end": v(14.73, -14) * mm, "construction": true});
            skLineSegment(sketch, "E291", {"start": v(-14.73, 7) * mm, "end": v(-14.73, 14) * mm});
            skLineSegment(sketch, "E292", {"start": v(14.73, 7) * mm, "end": v(14.73, 14) * mm});
            skLineSegment(sketch, "E293", {"start": v(17.41, 12) * mm, "end": v(-17.41, 12) * mm});
            skPoint(sketch, "E293.startSnap0", {"position": v(17.41, 10.5) * mm});
            skLineSegment(sketch, "E294", {"start": v(45.5, 14) * mm, "end": v(45.5, 7) * mm});
            skCircle(sketch, "E295", {"center": v(-27.57, 7) * mm, "radius": 7 * mm, "construction": true});
            skArc(sketch, "E296", {"start": v(-27.57, 12) * mm, "mid": v(-32.57, 7) * mm, "end": v(-27.57, 2) * mm});
            skLineSegment(sketch, "E297", {"start": v(-27.57, 12) * mm, "end": v(-27.57, 14) * mm});
            skLineSegment(sketch, "E298", {"start": v(-27.57, 14) * mm, "end": v(-38, 14) * mm});
            skLineSegment(sketch, "E299", {"start": v(-38, 14) * mm, "end": v(-38, 0) * mm});
            skLineSegment(sketch, "E300", {"start": v(-38, 0) * mm, "end": v(-27.57, 0) * mm});
            skLineSegment(sketch, "E301", {"start": v(-27.57, 0) * mm, "end": v(-27.57, 2) * mm});
            skCircle(sketch, "E302", {"center": v(0, 7) * mm, "radius": 1.25 * mm, "construction": true});
            skSolve(sketch);
        }
        {
            var Q0;
            Q0=qCreatedBy(id+"F2.planeOp",FACE);
            var sketch = newSketch(context, id + "F12", { "sketchPlane" : qUnion([Q0])});
            skLineSegment(sketch, "E303.top", {"start": v(45.5, -14) * mm, "end": v(-45.5, -14) * mm, "construction": true});
            skLineSegment(sketch, "E303.left", {"start": v(45.5, 14) * mm, "end": v(45.5, -14) * mm, "construction": true});
            skLineSegment(sketch, "E303.right", {"start": v(-45.5, 14) * mm, "end": v(-45.5, -14) * mm, "construction": true});
            skPoint(sketch, "E303.middle", {"position": v(0, 0) * mm});
            skLineSegment(sketch, "E304", {"start": v(0, 14) * mm, "end": v(0, -14) * mm, "construction": true});
            skLineSegment(sketch, "E305.0", {"start": v(-17.41, 14) * mm, "end": v(-17.41, -14) * mm, "construction": true});
            skLineSegment(sketch, "E306.MirrorCS", {"start": v(17.41, 14) * mm, "end": v(17.41, -14) * mm, "construction": true});
            skLineSegment(sketch, "E307", {"start": v(-17.41, 14) * mm, "end": v(-17.41, 7) * mm});
            skLineSegment(sketch, "E308", {"start": v(-17.41, 7) * mm, "end": v(17.41, 7) * mm});
            skLineSegment(sketch, "E309", {"start": v(17.41, 7) * mm, "end": v(17.41, 14) * mm});
            skLineSegment(sketch, "E310", {"start": v(17.41, 14) * mm, "end": v(-17.41, 14) * mm});
            skLineSegment(sketch, "E311.0", {"start": v(-14.73, 14) * mm, "end": v(-14.73, -14) * mm, "construction": true});
            skLineSegment(sketch, "E312.MirrorCS", {"start": v(14.73, 14) * mm, "end": v(14.73, -14) * mm, "construction": true});
            skLineSegment(sketch, "E313", {"start": v(-14.73, 7) * mm, "end": v(-14.73, 14) * mm});
            skLineSegment(sketch, "E314", {"start": v(14.73, 7) * mm, "end": v(14.73, 14) * mm});
            skLineSegment(sketch, "E315", {"start": v(17.41, 12) * mm, "end": v(-17.41, 12) * mm});
            skPoint(sketch, "E315.startSnap0", {"position": v(17.41, 10.5) * mm});
            skLineSegment(sketch, "E316", {"start": v(45.5, 14) * mm, "end": v(45.5, 7) * mm});
            skCircle(sketch, "E317", {"center": v(-27.57, 7) * mm, "radius": 7 * mm, "construction": true});
            skArc(sketch, "E318", {"start": v(-27.57, 12) * mm, "mid": v(-32.57, 7) * mm, "end": v(-27.57, 2) * mm});
            skLineSegment(sketch, "E319", {"start": v(-27.57, 12) * mm, "end": v(-27.57, 14) * mm});
            skLineSegment(sketch, "E320", {"start": v(-27.57, 14) * mm, "end": v(-38, 14) * mm});
            skLineSegment(sketch, "E321", {"start": v(-38, 14) * mm, "end": v(-38, 0) * mm});
            skLineSegment(sketch, "E322", {"start": v(-38, 0) * mm, "end": v(-27.57, 0) * mm});
            skLineSegment(sketch, "E323", {"start": v(-27.57, 0) * mm, "end": v(-27.57, 2) * mm});
            skCircle(sketch, "E324", {"center": v(0, 7) * mm, "radius": 1.25 * mm, "construction": true});
            skSolve(sketch);
        }
        {
            var Q0;
            Q0=qCreatedBy(makeId("Top.planeOp"),FACE);
            var sketch = newSketch(context, id + "F13", { "sketchPlane" : qUnion([Q0])});
            skPoint(sketch, "E325.middle", {"position": v(0, 0) * mm});
            skCircle(sketch, "E326", {"center": v(0, 0) * mm, "radius": 2.5 * mm, "construction": true});
            skLineSegment(sketch, "E327.MirrorCS", {"start": v(-25.15, 17.41) * mm, "end": v(-38, 17.41) * mm});
            skLineSegment(sketch, "E328.MirrorCS", {"start": v(-25.15, -17.41) * mm, "end": v(-38, -17.41) * mm});
            skLineSegment(sketch, "E329.MirrorCS", {"start": v(-38, 17.41) * mm, "end": v(-38, -17.41) * mm});
            skArc(sketch, "E330", {"start": v(-25.15, 17.41) * mm, "mid": v(-29.5, 0) * mm, "end": v(-25.15, -17.41) * mm});
            skLineSegment(sketch, "E331.bottom", {"start": v(-45.5, 8.28) * mm, "end": v(-45.5, -8.52) * mm, "construction": true});
            skLineSegment(sketch, "E331.left", {"start": v(-45.5, 8.28) * mm, "end": v(-59, 8.28) * mm, "construction": true});
            skLineSegment(sketch, "E332", {"start": v(-45.5, -8.52) * mm, "end": v(-59, -8.52) * mm, "construction": true});
            skLineSegment(sketch, "E333", {"start": v(-59, -8.52) * mm, "end": v(-59, 8.28) * mm, "construction": true});
            skLineSegment(sketch, "E334", {"start": v(-45.5, 8.28) * mm, "end": v(-59, -8.52) * mm, "construction": true});
            skLineSegment(sketch, "E335", {"start": v(-45.5, -8.52) * mm, "end": v(-59, 8.28) * mm, "construction": true});
            skLineSegment(sketch, "E336", {"start": v(-52.24, 0) * mm, "end": v(-42.5, 0) * mm, "construction": true});
            skLineSegment(sketch, "E337", {"start": v(-27.2, 0) * mm, "end": v(-42.4, 0) * mm, "construction": true});
            skLineSegment(sketch, "E338.0", {"start": v(-62, -8.52) * mm, "end": v(-62, 8.28) * mm, "construction": true});
            skLineSegment(sketch, "E339", {"start": v(-45.5, 17.41) * mm, "end": v(-62, 17.41) * mm});
            skLineSegment(sketch, "E340", {"start": v(-62, 17.41) * mm, "end": v(-62, -17.41) * mm});
            skLineSegment(sketch, "E341", {"start": v(-62, -17.41) * mm, "end": v(-45.5, -17.41) * mm});
            skLineSegment(sketch, "E342.0", {"start": v(-59, -14.41) * mm, "end": v(-45.5, -14.41) * mm});
            skLineSegment(sketch, "E342.1", {"start": v(-59, 14.41) * mm, "end": v(-59, -14.41) * mm});
            skLineSegment(sketch, "E342.2", {"start": v(-45.5, 14.41) * mm, "end": v(-59, 14.41) * mm});
            skLineSegment(sketch, "E343", {"start": v(-38, -17.41) * mm, "end": v(-45.5, -17.41) * mm});
            skLineSegment(sketch, "E344", {"start": v(-45.5, -14.41) * mm, "end": v(-38, -14.41) * mm});
            skLineSegment(sketch, "E345", {"start": v(-45.5, 14.41) * mm, "end": v(-38, 14.41) * mm});
            skLineSegment(sketch, "E346", {"start": v(-45.5, 17.41) * mm, "end": v(-38, 17.41) * mm});
            skSolve(sketch);
        }
        {
            var Q0;
            Q0=qCreatedBy(id+"F4.planeOp",FACE);
            var sketch = newSketch(context, id + "F14", { "sketchPlane" : qUnion([Q0])});
            skPoint(sketch, "E347.middle", {"position": v(0, 0) * mm});
            skCircle(sketch, "E348", {"center": v(0, 0) * mm, "radius": 2.5 * mm, "construction": true});
            skLineSegment(sketch, "E349.MirrorCS", {"start": v(-25.15, 17.41) * mm, "end": v(-38, 17.41) * mm});
            skLineSegment(sketch, "E350.MirrorCS", {"start": v(-25.15, -17.41) * mm, "end": v(-38, -17.41) * mm});
            skLineSegment(sketch, "E351.MirrorCS", {"start": v(-45.5, 17.41) * mm, "end": v(-45.5, -17.41) * mm});
            skArc(sketch, "E352", {"start": v(-25.15, 17.41) * mm, "mid": v(-29.5, 0) * mm, "end": v(-25.15, -17.41) * mm});
            skLineSegment(sketch, "E353.bottom", {"start": v(-45.5, 8.28) * mm, "end": v(-45.5, -8.52) * mm, "construction": true});
            skLineSegment(sketch, "E353.left", {"start": v(-45.5, 8.28) * mm, "end": v(-59, 8.28) * mm, "construction": true});
            skLineSegment(sketch, "E354", {"start": v(-45.5, -8.52) * mm, "end": v(-59, -8.52) * mm, "construction": true});
            skLineSegment(sketch, "E355", {"start": v(-59, -8.52) * mm, "end": v(-59, 8.28) * mm, "construction": true});
            skLineSegment(sketch, "E356", {"start": v(-45.5, 8.28) * mm, "end": v(-59, -8.52) * mm, "construction": true});
            skLineSegment(sketch, "E357", {"start": v(-45.5, -8.52) * mm, "end": v(-59, 8.28) * mm, "construction": true});
            skLineSegment(sketch, "E358", {"start": v(-52.24, 0) * mm, "end": v(-42.5, 0) * mm, "construction": true});
            skLineSegment(sketch, "E359", {"start": v(-27.2, 0) * mm, "end": v(-42.4, 0) * mm, "construction": true});
            skLineSegment(sketch, "E360.0", {"start": v(-62, -8.52) * mm, "end": v(-62, 8.28) * mm, "construction": true});
            skLineSegment(sketch, "E361", {"start": v(-45.5, 17.41) * mm, "end": v(-62, 17.41) * mm});
            skLineSegment(sketch, "E362", {"start": v(-62, 17.41) * mm, "end": v(-62, -17.41) * mm});
            skLineSegment(sketch, "E363", {"start": v(-62, -17.41) * mm, "end": v(-45.5, -17.41) * mm});
            skLineSegment(sketch, "E364.0", {"start": v(-59, -14.41) * mm, "end": v(-45.5, -14.41) * mm});
            skLineSegment(sketch, "E364.1", {"start": v(-59, 14.41) * mm, "end": v(-59, -14.41) * mm});
            skLineSegment(sketch, "E364.2", {"start": v(-45.5, 14.41) * mm, "end": v(-59, 14.41) * mm});
            skLineSegment(sketch, "E365.0", {"start": v(-42.5, 17.41) * mm, "end": v(-42.5, -17.41) * mm});
            skLineSegment(sketch, "E366", {"start": v(-38, 17.41) * mm, "end": v(-45.5, 17.41) * mm});
            skLineSegment(sketch, "E367", {"start": v(-38, -17.41) * mm, "end": v(-45.5, -17.41) * mm});
            skSolve(sketch);
        }
        {
            var Q0;
            {var subQ45=sQuery(id+"F8.wireOp",EDGE,"E125");Q0=makeQuery(id+"F8.imprint","IMPRINT",FACE,{"disambiguationData":[TD([[makeQuery(id+"F8.imprint","IMPRINT",EDGE,{"derivedFrom":subQ45}),-1.0]])]});}
            extrude(context, id + "F15", {"entities" : qUnion([Q0]), "depth" : 7 * mm});
        }
        {
            var Q0;
            {var subQ0=sQuery(id+"F8.wireOp",EDGE,"E138.MirrorCS");Q0=makeQuery(id+"F8.imprint","IMPRINT",FACE,{"disambiguationData":[TD([[makeQuery(id+"F8.imprint","IMPRINT",EDGE,{"derivedFrom":subQ0}),1.0]])]});}
            var Q1;
            {var subQ0=sQuery(id+"F8.wireOp",EDGE,"E137.MirrorCS");Q1=makeQuery(id+"F8.imprint","IMPRINT",FACE,{"disambiguationData":[TD([[makeQuery(id+"F8.imprint","IMPRINT",EDGE,{"derivedFrom":subQ0}),1.0]])]});}
            var Q2;
            {var subQ0=sQuery(id+"F8.wireOp",EDGE,"E148");Q2=makeQuery(id+"F8.imprint","IMPRINT",FACE,{"disambiguationData":[TD([[makeQuery(id+"F8.imprint","IMPRINT",EDGE,{"derivedFrom":subQ0}),1.0]])]});}
            var Q3;
            {var subQ0=sQuery(id+"F8.wireOp",EDGE,"E125");Q3=makeQuery(id+"F8.imprint","IMPRINT",FACE,{"disambiguationData":[TD([[makeQuery(id+"F8.imprint","IMPRINT",EDGE,{"derivedFrom":subQ0}),1.0]])]});}
            var Q4;
            {var subQ0=sQuery(id+"F8.wireOp",EDGE,"E126");Q4=makeQuery(id+"F8.imprint","IMPRINT",FACE,{"disambiguationData":[TD([[makeQuery(id+"F8.imprint","IMPRINT",EDGE,{"derivedFrom":subQ0}),1.0]])]});}
            var Q5;
            {var subQ0=sQuery(id+"F8.wireOp",EDGE,"E127");Q5=makeQuery(id+"F8.imprint","IMPRINT",FACE,{"disambiguationData":[TD([[makeQuery(id+"F8.imprint","IMPRINT",EDGE,{"derivedFrom":subQ0}),1.0]])]});}
            var Q6;
            {var subQ0=sQuery(id+"F8.wireOp",EDGE,"E128");Q6=makeQuery(id+"F8.imprint","IMPRINT",FACE,{"disambiguationData":[TD([[makeQuery(id+"F8.imprint","IMPRINT",EDGE,{"derivedFrom":subQ0}),1.0]])]});}
            var Q7;
            {var subQ0=sQuery(id+"F8.wireOp",EDGE,"E129");Q7=makeQuery(id+"F8.imprint","IMPRINT",FACE,{"disambiguationData":[TD([[makeQuery(id+"F8.imprint","IMPRINT",EDGE,{"derivedFrom":subQ0}),1.0]])]});}
            var Q8;
            {var subQ0=sQuery(id+"F8.wireOp",EDGE,"E130");Q8=makeQuery(id+"F8.imprint","IMPRINT",FACE,{"disambiguationData":[TD([[makeQuery(id+"F8.imprint","IMPRINT",EDGE,{"derivedFrom":subQ0}),1.0]])]});}
            var Q9;
            {var subQ0=sQuery(id+"F8.wireOp",EDGE,"E131");Q9=makeQuery(id+"F8.imprint","IMPRINT",FACE,{"disambiguationData":[TD([[makeQuery(id+"F8.imprint","IMPRINT",EDGE,{"derivedFrom":subQ0}),1.0]])]});}
            var Q10;
            {var subQ0=sQuery(id+"F8.wireOp",EDGE,"E132");Q10=makeQuery(id+"F8.imprint","IMPRINT",FACE,{"disambiguationData":[TD([[makeQuery(id+"F8.imprint","IMPRINT",EDGE,{"derivedFrom":subQ0}),1.0]])]});}
            var Q11;
            {var subQ0=sQuery(id+"F8.wireOp",EDGE,"E133");Q11=makeQuery(id+"F8.imprint","IMPRINT",FACE,{"disambiguationData":[TD([[makeQuery(id+"F8.imprint","IMPRINT",EDGE,{"derivedFrom":subQ0}),1.0]])]});}
            var Q12;
            {var subQ0=sQuery(id+"F8.wireOp",EDGE,"E134");Q12=makeQuery(id+"F8.imprint","IMPRINT",FACE,{"disambiguationData":[TD([[makeQuery(id+"F8.imprint","IMPRINT",EDGE,{"derivedFrom":subQ0}),1.0]])]});}
            var Q13;
            {var subQ0=sQuery(id+"F8.wireOp",EDGE,"E135");Q13=makeQuery(id+"F8.imprint","IMPRINT",FACE,{"disambiguationData":[TD([[makeQuery(id+"F8.imprint","IMPRINT",EDGE,{"derivedFrom":subQ0}),1.0]])]});}
            var Q14;
            {var subQ0=sQuery(id+"F8.wireOp",EDGE,"E136");Q14=makeQuery(id+"F8.imprint","IMPRINT",FACE,{"disambiguationData":[TD([[makeQuery(id+"F8.imprint","IMPRINT",EDGE,{"derivedFrom":subQ0}),1.0]])]});}
            var Q15;
            {var subQ0=sQuery(id+"F8.wireOp",EDGE,"E146.MirrorCS");Q15=makeQuery(id+"F8.imprint","IMPRINT",FACE,{"disambiguationData":[TD([[makeQuery(id+"F8.imprint","IMPRINT",EDGE,{"derivedFrom":subQ0}),1.0]])]});}
            var Q16;
            {var subQ0=sQuery(id+"F8.wireOp",EDGE,"E145.MirrorCS");Q16=makeQuery(id+"F8.imprint","IMPRINT",FACE,{"disambiguationData":[TD([[makeQuery(id+"F8.imprint","IMPRINT",EDGE,{"derivedFrom":subQ0}),1.0]])]});}
            var Q17;
            {var subQ0=sQuery(id+"F8.wireOp",EDGE,"E144.MirrorCS");Q17=makeQuery(id+"F8.imprint","IMPRINT",FACE,{"disambiguationData":[TD([[makeQuery(id+"F8.imprint","IMPRINT",EDGE,{"derivedFrom":subQ0}),1.0]])]});}
            var Q18;
            {var subQ0=sQuery(id+"F8.wireOp",EDGE,"E143.MirrorCS");Q18=makeQuery(id+"F8.imprint","IMPRINT",FACE,{"disambiguationData":[TD([[makeQuery(id+"F8.imprint","IMPRINT",EDGE,{"derivedFrom":subQ0}),1.0]])]});}
            var Q19;
            {var subQ0=sQuery(id+"F8.wireOp",EDGE,"E142.MirrorCS");Q19=makeQuery(id+"F8.imprint","IMPRINT",FACE,{"disambiguationData":[TD([[makeQuery(id+"F8.imprint","IMPRINT",EDGE,{"derivedFrom":subQ0}),1.0]])]});}
            var Q20;
            {var subQ0=sQuery(id+"F8.wireOp",EDGE,"E147");Q20=makeQuery(id+"F8.imprint","IMPRINT",FACE,{"disambiguationData":[TD([[makeQuery(id+"F8.imprint","IMPRINT",EDGE,{"derivedFrom":subQ0}),1.0]])]});}
            var Q21;
            {var subQ0=sQuery(id+"F8.wireOp",EDGE,"E141.MirrorCS");Q21=makeQuery(id+"F8.imprint","IMPRINT",FACE,{"disambiguationData":[TD([[makeQuery(id+"F8.imprint","IMPRINT",EDGE,{"derivedFrom":subQ0}),1.0]])]});}
            var Q22;
            {var subQ0=sQuery(id+"F8.wireOp",EDGE,"E140.MirrorCS");Q22=makeQuery(id+"F8.imprint","IMPRINT",FACE,{"disambiguationData":[TD([[makeQuery(id+"F8.imprint","IMPRINT",EDGE,{"derivedFrom":subQ0}),1.0]])]});}
            var Q23;
            {var subQ0=sQuery(id+"F8.wireOp",EDGE,"E139.MirrorCS");Q23=makeQuery(id+"F8.imprint","IMPRINT",FACE,{"disambiguationData":[TD([[makeQuery(id+"F8.imprint","IMPRINT",EDGE,{"derivedFrom":subQ0}),1.0]])]});}
            extrude(context, id + "F16", {"entities" : qUnion([Q0, Q1, Q2, Q3, Q4, Q5, Q6, Q7, Q8, Q9, Q10, Q11, Q12, Q13, Q14, Q15, Q16, Q17, Q18, Q19, Q20, Q21, Q22, Q23]), "operationType" : NewBodyOperationType.ADD, "depth" : 2 * mm});
        }
        {
            var Q0;
            {var subQ0=sQuery(id+"F9.wireOp",EDGE,"E203");Q0=makeQuery(id+"F9.imprint","IMPRINT",FACE,{"disambiguationData":[TD([[makeQuery(id+"F9.imprint","IMPRINT",EDGE,{"derivedFrom":subQ0}),1.0]])]});}
            var Q1;
            {var subQ0=sQuery(id+"F9.wireOp",EDGE,"E214");Q1=makeQuery(id+"F9.imprint","IMPRINT",FACE,{"disambiguationData":[TD([[makeQuery(id+"F9.imprint","IMPRINT",EDGE,{"derivedFrom":subQ0}),-1.0]])]});}
            var Q2;
            Q2=sQuery(id+"F9.wireOp",EDGE,"E211");
            revolve(context, id + "F17", {"operationType" : NewBodyOperationType.ADD, "entities" : qUnion([Q0, Q1]), "axis" : qUnion([Q2]), "revolveType" : RevolveType.SYMMETRIC, "angle" : 306 * degree});
        }
        {
            var Q0;
            {var subQ3=sQuery(id+"F9.wireOp",EDGE,"E207");Q0=makeQuery(id+"F9.imprint","IMPRINT",FACE,{"disambiguationData":[TD([[makeQuery(id+"F9.imprint","IMPRINT",EDGE,{"derivedFrom":subQ3}),1.0]])]});}
            var Q1;
            Q1=makeQuery(id+"F9.imprint","IMPRINT",FACE,{"disambiguationData":[TD([[makeQuery(id+"F9.imprint","IMPRINT",EDGE,{"derivedFrom":sQuery(id+"F9.wireOp",EDGE,"E208")}),-1.0]])]});
            var Q2;
            Q2=sQuery(id+"F9.wireOp",EDGE,"E211");
            revolve(context, id + "F18", {"operationType" : NewBodyOperationType.ADD, "entities" : qUnion([Q0, Q1]), "axis" : qUnion([Q2]), "revolveType" : RevolveType.FULL});
        }
        {
            var Q0;
            Q0=makeQuery(id+"F12.imprint","IMPRINT",FACE,{"disambiguationData":[TD([[makeQuery(id+"F12.imprint","IMPRINT",EDGE,{"derivedFrom":sQuery(id+"F12.wireOp",EDGE,"E318")}),-1.0]])]});
            extrude(context, id + "F19", {"entities" : qUnion([Q0]), "operationType" : NewBodyOperationType.ADD, "depth" : 2.5 * mm});
        }
        {
            var Q0;
            Q0=makeQuery(id+"F11.imprint","IMPRINT",FACE,{"disambiguationData":[TD([[makeQuery(id+"F11.imprint","IMPRINT",EDGE,{"derivedFrom":sQuery(id+"F11.wireOp",EDGE,"E296")}),-1.0]])]});
            extrude(context, id + "F20", {"entities" : qUnion([Q0]), "operationType" : NewBodyOperationType.ADD, "oppositeDirection" : true, "depth" : 2.5 * mm});
        }
        {
            var Q0;
            Q0=makeQuery(id+"F13.imprint","IMPRINT",FACE,{"disambiguationData":[TD([[makeQuery(id+"F13.imprint","IMPRINT",EDGE,{"derivedFrom":sQuery(id+"F13.wireOp",EDGE,"E327.MirrorCS")}),1.0]])]});
            var Q1;
            {var subQ1=sQuery(id+"F13.wireOp",EDGE,"E331.bottom");Q1=makeQuery(id+"F13.imprint","IMPRINT",FACE,{"disambiguationData":[TD([[makeQuery(id+"F13.imprint","IMPRINT",EDGE,{"derivedFrom":subQ1}),1.0]])]});}
            var Q2;
            {var subQ5=sQuery(id+"F13.wireOp",EDGE,"E333");Q2=makeQuery(id+"F13.imprint","IMPRINT",FACE,{"disambiguationData":[TD([[makeQuery(id+"F13.imprint","IMPRINT",EDGE,{"derivedFrom":subQ5}),-1.0]])]});}
            var Q3;
            {var subQ0=sQuery(id+"F13.wireOp",EDGE,"E342.0");Q3=makeQuery(id+"F13.imprint","IMPRINT",FACE,{"disambiguationData":[TD([[makeQuery(id+"F13.imprint","IMPRINT",EDGE,{"derivedFrom":subQ0}),1.0]])]});}
            var Q4;
            Q4=makeQuery(id+"F13.imprint","IMPRINT",FACE,{"disambiguationData":[TD([[makeQuery(id+"F13.imprint","IMPRINT",EDGE,{"derivedFrom":sQuery(id+"F13.wireOp",EDGE,"E339")}),1.0]])]});
            extrude(context, id + "F21", {"entities" : qUnion([Q0, Q1, Q2, Q3, Q4]), "operationType" : NewBodyOperationType.ADD, "depth" : 2.5 * mm});
        }
        {
            var Q0;
            {var subQ3=sQuery(id+"F14.wireOp",EDGE,"E349.MirrorCS");Q0=makeQuery(id+"F14.imprint","IMPRINT",FACE,{"disambiguationData":[TD([[makeQuery(id+"F14.imprint","IMPRINT",EDGE,{"derivedFrom":subQ3}),1.0]])]});}
            var Q1;
            {var subQ7=sQuery(id+"F14.wireOp",EDGE,"E365.0");Q1=makeQuery(id+"F14.imprint","IMPRINT",FACE,{"disambiguationData":[TD([[makeQuery(id+"F14.imprint","IMPRINT",EDGE,{"derivedFrom":subQ7}),-1.0]])]});}
            extrude(context, id + "F22", {"entities" : qUnion([Q0, Q1]), "operationType" : NewBodyOperationType.ADD, "oppositeDirection" : true, "depth" : 2.5 * mm});
        }
        {
            var Q0;
            {var subQ4=sQuery(id+"F13.wireOp",EDGE,"E333");Q0=makeQuery(id+"F13.imprint","IMPRINT",FACE,{"disambiguationData":[TD([[makeQuery(id+"F13.imprint","IMPRINT",EDGE,{"derivedFrom":subQ4}),1.0]])]});}
            var Q1;
            {var subQ0=sQuery(id+"F13.wireOp",EDGE,"6jEM1cKR-Vwea-ILg7-sG8q-rrc46WkZxeoR");Q1=makeQuery(id+"F13.imprint","IMPRINT",FACE,{"disambiguationData":[TD([[makeQuery(id+"F13.imprint","IMPRINT",EDGE,{"derivedFrom":subQ0}),-1.0]])]});}
            var Q2;
            {var subQ0=sQuery(id+"F13.wireOp",EDGE,"E339");Q2=makeQuery(id+"F13.imprint","IMPRINT",FACE,{"disambiguationData":[TD([[makeQuery(id+"F13.imprint","IMPRINT",EDGE,{"derivedFrom":subQ0}),1.0]])]});}
            extrude(context, id + "F23", {"entities" : qUnion([Q0, Q1, Q2]), "operationType" : NewBodyOperationType.ADD, "depth" : 14 * mm});
        }
        {
            var Q0;
            {var subQ0=sQuery(id+"F14.wireOp",EDGE,"E361");Q0=makeQuery(id+"F14.imprint","IMPRINT",FACE,{"disambiguationData":[TD([[makeQuery(id+"F14.imprint","IMPRINT",EDGE,{"derivedFrom":subQ0}),1.0]])]});}
            extrude(context, id + "F24", {"entities" : qUnion([Q0]), "operationType" : NewBodyOperationType.ADD, "depth" : 45.67 * mm});
        }
        {
            var Q0;
            Q0=makeQuery(id+"F10.imprint","IMPRINT",FACE,{"disambiguationData":[TD([[makeQuery(id+"F10.imprint","IMPRINT",EDGE,{"derivedFrom":sQuery(id+"F10.wireOp",EDGE,"E256")}),-1.0]])]});
            var Q1;
            {var subQ0=sQuery(id+"F10.wireOp",EDGE,"6a0bf37f-b3f9-4be4-bbcd-48762ca18b15");Q1=makeQuery(id+"F10.imprint","IMPRINT",FACE,{"disambiguationData":[TD([[makeQuery(id+"F10.imprint","IMPRINT",EDGE,{"derivedFrom":subQ0}),-1.0]])]});}
            var Q2;
            Q2=makeQuery(id+"F10.imprint","IMPRINT",FACE,{"disambiguationData":[TD([[makeQuery(id+"F10.imprint","IMPRINT",EDGE,{"derivedFrom":sQuery(id+"F10.wireOp",EDGE,"E256")}),1.0]])]});
            var Q3;
            Q3=makeQuery(id+"F10.imprint","IMPRINT",FACE,{"disambiguationData":[TD([[makeQuery(id+"F10.imprint","IMPRINT",EDGE,{"derivedFrom":sQuery(id+"F10.wireOp",EDGE,"74831fd5-661e-4b10-8ee2-b21f2208addb.1")}),-1.0]])]});
            var Q4;
            {var subQ0=sQuery(id+"F10.wireOp",EDGE,"36538cae-b972-4159-a8ab-ed7d0897e562");Q4=makeQuery(id+"F10.imprint","IMPRINT",FACE,{"disambiguationData":[TD([[makeQuery(id+"F10.imprint","IMPRINT",EDGE,{"derivedFrom":subQ0}),1.0]])]});}
            var Q5;
            Q5=makeQuery(id+"F10.imprint","IMPRINT",FACE,{"disambiguationData":[TD([[makeQuery(id+"F10.imprint","IMPRINT",EDGE,{"derivedFrom":sQuery(id+"F10.wireOp",EDGE,"b83bca02-1ddf-4d69-9cef-079f7d8efa28.MirrorCS")}),-1.0]])]});
            var Q6;
            Q6=makeQuery(id+"F10.imprint","IMPRINT",FACE,{"disambiguationData":[TD([[makeQuery(id+"F10.imprint","IMPRINT",EDGE,{"derivedFrom":sQuery(id+"F10.wireOp",EDGE,"5ed1b390-7d64-40a2-9961-03988ffd9427.0")}),1.0]])]});
            var Q7;
            {var subQ2=sQuery(id+"F10.wireOp",EDGE,"E268.MirrorCS");Q7=makeQuery(id+"F10.imprint","IMPRINT",FACE,{"disambiguationData":[TD([[makeQuery(id+"F10.imprint","IMPRINT",EDGE,{"derivedFrom":subQ2}),1.0]])]});}
            var Q8;
            {var subQ0=sQuery(id+"F10.wireOp",EDGE,"E262");Q8=makeQuery(id+"F10.imprint","IMPRINT",FACE,{"disambiguationData":[TD([[makeQuery(id+"F10.imprint","IMPRINT",EDGE,{"derivedFrom":subQ0}),-1.0]])]});}
            var Q9;
            {var subQ2=sQuery(id+"F10.wireOp",EDGE,"E266");Q9=makeQuery(id+"F10.imprint","IMPRINT",FACE,{"disambiguationData":[TD([[makeQuery(id+"F10.imprint","IMPRINT",EDGE,{"derivedFrom":subQ2}),-1.0]])]});}
            var Q10;
            {var subQ4=sQuery(id+"F10.wireOp",EDGE,"E260");Q10=makeQuery(id+"F10.imprint","IMPRINT",FACE,{"disambiguationData":[TD([[makeQuery(id+"F10.imprint","IMPRINT",EDGE,{"derivedFrom":subQ4}),1.0]])]});}
            extrude(context, id + "F25", {"entities" : qUnion([Q0, Q1, Q2, Q3, Q4, Q5, Q6, Q7, Q8, Q9, Q10]), "operationType" : NewBodyOperationType.ADD, "oppositeDirection" : true, "depth" : 3 * mm});
        }
        {
            var Q0;
            Q0=makeQuery(id+"F10.imprint","IMPRINT",FACE,{"disambiguationData":[TD([[makeQuery(id+"F10.imprint","IMPRINT",EDGE,{"derivedFrom":sQuery(id+"F10.wireOp",EDGE,"b83bca02-1ddf-4d69-9cef-079f7d8efa28.MirrorCS")}),-1.0]])]});
            var Q1;
            Q1=makeQuery(id+"F10.imprint","IMPRINT",FACE,{"disambiguationData":[TD([[makeQuery(id+"F10.imprint","IMPRINT",EDGE,{"derivedFrom":sQuery(id+"F10.wireOp",EDGE,"E256")}),1.0]])]});
            var Q2;
            Q2=makeQuery(id+"F10.imprint","IMPRINT",FACE,{"disambiguationData":[TD([[makeQuery(id+"F10.imprint","IMPRINT",EDGE,{"derivedFrom":sQuery(id+"F10.wireOp",EDGE,"5ed1b390-7d64-40a2-9961-03988ffd9427.0")}),1.0]])]});
            var Q3;
            Q3=makeQuery(id+"F10.imprint","IMPRINT",FACE,{"disambiguationData":[TD([[makeQuery(id+"F10.imprint","IMPRINT",EDGE,{"derivedFrom":sQuery(id+"F10.wireOp",EDGE,"74831fd5-661e-4b10-8ee2-b21f2208addb.1")}),-1.0]])]});
            var Q4;
            {var subQ4=sQuery(id+"F10.wireOp",EDGE,"E260");Q4=makeQuery(id+"F10.imprint","IMPRINT",FACE,{"disambiguationData":[TD([[makeQuery(id+"F10.imprint","IMPRINT",EDGE,{"derivedFrom":subQ4}),1.0]])]});}
            extrude(context, id + "F26", {"entities" : qUnion([Q0, Q1, Q2, Q3, Q4]), "operationType" : NewBodyOperationType.ADD, "depth" : 8.2 * mm});
        }
        {
            var Q0;
            Q0=qCreatedBy(id+"F6.planeOp",FACE);
            var sketch = newSketch(context, id + "F27", { "sketchPlane" : qUnion([Q0])});
            skCircle(sketch, "E368", {"center": v(0, 0) * mm, "radius": 1.5 * mm, "construction": true});
            skCircle(sketch, "E369", {"center": v(0, 53.3) * mm, "radius": 1.25 * mm, "construction": true});
            skLineSegment(sketch, "E370", {"start": v(0, 55.8) * mm, "end": v(0, 14) * mm, "construction": true});
            skCircle(sketch, "E371", {"center": v(0, 53.3) * mm, "radius": 3.45 * mm});
            skCircle(sketch, "E372", {"center": v(0, 53.3) * mm, "radius": 5 * mm});
            skSolve(sketch);
        }
        {
            var Q0;
            Q0=qCreatedBy(id+"F5.planeOp",FACE);
            var sketch = newSketch(context, id + "F28", { "sketchPlane" : qUnion([Q0])});
            skPoint(sketch, "E373.middle", {"position": v(0, 0) * mm});
            skCircle(sketch, "E374", {"center": v(0, 0) * mm, "radius": 1.5 * mm, "construction": true});
            skLineSegment(sketch, "E375.bottom", {"start": v(-45.5, 8.28) * mm, "end": v(-45.5, -8.52) * mm, "construction": true});
            skLineSegment(sketch, "E375.left", {"start": v(-45.5, 8.28) * mm, "end": v(-59, 8.28) * mm, "construction": true});
            skLineSegment(sketch, "E376", {"start": v(-45.5, -8.52) * mm, "end": v(-59, -8.52) * mm, "construction": true});
            skLineSegment(sketch, "E377", {"start": v(-59, -8.52) * mm, "end": v(-59, 8.28) * mm, "construction": true});
            skLineSegment(sketch, "E378", {"start": v(-45.5, 8.28) * mm, "end": v(-59, -8.52) * mm, "construction": true});
            skLineSegment(sketch, "E379", {"start": v(-45.5, -8.52) * mm, "end": v(-59, 8.28) * mm, "construction": true});
            skLineSegment(sketch, "E380", {"start": v(-52.24, 0) * mm, "end": v(-42.5, 0) * mm, "construction": true});
            skLineSegment(sketch, "E381", {"start": v(-27.2, 0) * mm, "end": v(-42.4, 0) * mm, "construction": true});
            skLineSegment(sketch, "E382.0", {"start": v(-62, -8.52) * mm, "end": v(-62, 8.28) * mm, "construction": true});
            skLineSegment(sketch, "E383", {"start": v(-62, 17.41) * mm, "end": v(-62, -17.41) * mm});
            skLineSegment(sketch, "E384.0", {"start": v(-59, -14.41) * mm, "end": v(-45.5, -14.41) * mm, "construction": true});
            skLineSegment(sketch, "E384.1", {"start": v(-59, 14.41) * mm, "end": v(-59, -14.41) * mm});
            skLineSegment(sketch, "E384.2", {"start": v(-45.5, 14.41) * mm, "end": v(-59, 14.41) * mm, "construction": true});
            skLineSegment(sketch, "E385.0", {"start": v(-42.5, 17.41) * mm, "end": v(-42.5, -17.41) * mm});
            skLineSegment(sketch, "E386", {"start": v(-62, 17.41) * mm, "end": v(-42.5, 17.41) * mm});
            skLineSegment(sketch, "E387", {"start": v(-42.5, -17.41) * mm, "end": v(-62, -17.41) * mm});
            skLineSegment(sketch, "E388", {"start": v(-45.5, 14.41) * mm, "end": v(-45.5, -14.41) * mm});
            skLineSegment(sketch, "E389", {"start": v(-62, 14.41) * mm, "end": v(-42.5, 14.41) * mm});
            skLineSegment(sketch, "E390", {"start": v(-42.5, -14.41) * mm, "end": v(-62, -14.41) * mm});
            skPoint(sketch, "E390.endSnap0", {"position": v(-52.25, -14.41) * mm});
            skSolve(sketch);
        }
        {
            var Q0;
            Q0=qCreatedBy(id+"F7.planeOp",FACE);
            var sketch = newSketch(context, id + "F29", { "sketchPlane" : qUnion([Q0])});
            skPoint(sketch, "E391.middle", {"position": v(-3, 0) * mm});
            skLineSegment(sketch, "E392.bottom", {"start": v(-48.5, 8.28) * mm, "end": v(-48.5, -8.52) * mm, "construction": true});
            skLineSegment(sketch, "E392.left", {"start": v(-48.5, 8.28) * mm, "end": v(-62, 8.28) * mm, "construction": true});
            skLineSegment(sketch, "E393", {"start": v(-48.5, -8.52) * mm, "end": v(-62, -8.52) * mm, "construction": true});
            skLineSegment(sketch, "E394", {"start": v(-62, -8.52) * mm, "end": v(-62, 8.28) * mm, "construction": true});
            skLineSegment(sketch, "E395", {"start": v(-48.5, 8.28) * mm, "end": v(-62, -8.52) * mm, "construction": true});
            skLineSegment(sketch, "E396", {"start": v(-48.5, -8.52) * mm, "end": v(-62, 8.28) * mm, "construction": true});
            skLineSegment(sketch, "E397", {"start": v(-55.24, 0) * mm, "end": v(-45.5, 0) * mm, "construction": true});
            skLineSegment(sketch, "E398", {"start": v(-30.2, 0) * mm, "end": v(-45.4, 0) * mm, "construction": true});
            skLineSegment(sketch, "E399.0", {"start": v(-65, -8.52) * mm, "end": v(-65, 8.28) * mm, "construction": true});
            skLineSegment(sketch, "E400", {"start": v(-65, 17.41) * mm, "end": v(-65, -17.41) * mm});
            skLineSegment(sketch, "E401.0", {"start": v(-62, -14.41) * mm, "end": v(-48.5, -14.41) * mm, "construction": true});
            skLineSegment(sketch, "E401.1", {"start": v(-62, 14.41) * mm, "end": v(-62, -14.41) * mm});
            skLineSegment(sketch, "E401.2", {"start": v(-48.5, 14.41) * mm, "end": v(-62, 14.41) * mm, "construction": true});
            skLineSegment(sketch, "E402.0", {"start": v(-45.5, 17.41) * mm, "end": v(-45.5, -17.41) * mm});
            skLineSegment(sketch, "E403", {"start": v(-65, 17.41) * mm, "end": v(-45.5, 17.41) * mm});
            skLineSegment(sketch, "E404", {"start": v(-45.5, -17.41) * mm, "end": v(-65, -17.41) * mm});
            skCircle(sketch, "E405", {"center": v(0, 0) * mm, "radius": 3 * mm, "construction": true});
            skLineSegment(sketch, "E406", {"start": v(-48.5, 14.41) * mm, "end": v(-48.5, -14.41) * mm});
            skLineSegment(sketch, "E407", {"start": v(-65, 14.41) * mm, "end": v(-45.5, 14.41) * mm});
            skLineSegment(sketch, "E408", {"start": v(-45.5, -14.41) * mm, "end": v(-65, -14.41) * mm});
            skSolve(sketch);
        }
        {
            var Q0;
            Q0=sQuery(id+"F27.wireOp",VERTEX,"E369.center");
            var Q1;
            Q1=makeQuery(id+"F15.opExtrude","SWEPT_BODY",BODY,{"disambiguationData":[OSD([sQuery(id+"F8.wireOp",EDGE,"E125"),sQuery(id+"F8.wireOp",EDGE,"E126"),sQuery(id+"F8.wireOp",EDGE,"E127"),sQuery(id+"F8.wireOp",EDGE,"E128"),sQuery(id+"F8.wireOp",EDGE,"E129"),sQuery(id+"F8.wireOp",EDGE,"E130"),sQuery(id+"F8.wireOp",EDGE,"E131"),sQuery(id+"F8.wireOp",EDGE,"E132"),sQuery(id+"F8.wireOp",EDGE,"E133"),sQuery(id+"F8.wireOp",EDGE,"E134"),sQuery(id+"F8.wireOp",EDGE,"E135"),sQuery(id+"F8.wireOp",EDGE,"E136"),sQuery(id+"F8.wireOp",EDGE,"E137.MirrorCS"),sQuery(id+"F8.wireOp",EDGE,"E138.MirrorCS"),sQuery(id+"F8.wireOp",EDGE,"E139.MirrorCS"),sQuery(id+"F8.wireOp",EDGE,"E140.MirrorCS"),sQuery(id+"F8.wireOp",EDGE,"E141.MirrorCS"),sQuery(id+"F8.wireOp",EDGE,"E142.MirrorCS"),sQuery(id+"F8.wireOp",EDGE,"E143.MirrorCS"),sQuery(id+"F8.wireOp",EDGE,"E144.MirrorCS"),sQuery(id+"F8.wireOp",EDGE,"E145.MirrorCS"),sQuery(id+"F8.wireOp",EDGE,"E146.MirrorCS"),sQuery(id+"F8.wireOp",EDGE,"E147"),sQuery(id+"F8.wireOp",EDGE,"E148"),sQuery(id+"F8.wireOp",EDGE,"E124"),sQuery(id+"F8.wireOp",EDGE,"E149"),sQuery(id+"F8.wireOp",EDGE,"E150"),sQuery(id+"F8.wireOp",EDGE,"E151"),sQuery(id+"F8.wireOp",EDGE,"E152"),sQuery(id+"F8.wireOp",EDGE,"E153"),sQuery(id+"F8.wireOp",EDGE,"E154"),sQuery(id+"F8.wireOp",EDGE,"E155"),sQuery(id+"F8.wireOp",EDGE,"E156"),sQuery(id+"F8.wireOp",EDGE,"E157"),sQuery(id+"F8.wireOp",EDGE,"E158"),sQuery(id+"F8.wireOp",EDGE,"E159"),sQuery(id+"F8.wireOp",EDGE,"E160"),sQuery(id+"F8.wireOp",EDGE,"E161.MirrorCS"),sQuery(id+"F8.wireOp",EDGE,"E162.MirrorCS"),sQuery(id+"F8.wireOp",EDGE,"E163.MirrorCS"),sQuery(id+"F8.wireOp",EDGE,"E164.MirrorCS"),sQuery(id+"F8.wireOp",EDGE,"E165.MirrorCS"),sQuery(id+"F8.wireOp",EDGE,"E166.MirrorCS"),sQuery(id+"F8.wireOp",EDGE,"E167.MirrorCS"),sQuery(id+"F8.wireOp",EDGE,"E168.MirrorCS"),sQuery(id+"F8.wireOp",EDGE,"E169.MirrorCS"),sQuery(id+"F8.wireOp",EDGE,"E170.MirrorCS"),sQuery(id+"F8.wireOp",EDGE,"E171"),sQuery(id+"F8.wireOp",EDGE,"E172"),sQuery(id+"F8.wireOp",EDGE,"E173"),sQuery(id+"F8.wireOp",EDGE,"E174"),sQuery(id+"F8.wireOp",EDGE,"E175"),sQuery(id+"F8.wireOp",EDGE,"E176"),sQuery(id+"F8.wireOp",EDGE,"E177"),sQuery(id+"F8.wireOp",EDGE,"E178"),sQuery(id+"F8.wireOp",EDGE,"E179"),sQuery(id+"F8.wireOp",EDGE,"E180"),sQuery(id+"F8.wireOp",EDGE,"E181"),sQuery(id+"F8.wireOp",EDGE,"E182"),sQuery(id+"F8.wireOp",EDGE,"E183"),sQuery(id+"F8.wireOp",EDGE,"E184"),sQuery(id+"F8.wireOp",EDGE,"E185"),sQuery(id+"F8.wireOp",EDGE,"E186"),sQuery(id+"F8.wireOp",EDGE,"E187"),sQuery(id+"F8.wireOp",EDGE,"E188"),sQuery(id+"F8.wireOp",EDGE,"E189"),sQuery(id+"F8.wireOp",EDGE,"E190"),sQuery(id+"F8.wireOp",EDGE,"E191"),sQuery(id+"F8.wireOp",EDGE,"E192"),sQuery(id+"F8.wireOp",EDGE,"E193"),sQuery(id+"F8.wireOp",EDGE,"E194"),sQuery(id+"F8.wireOp",EDGE,"E195"),sQuery(id+"F8.wireOp",EDGE,"E196"),sQuery(id+"F8.wireOp",EDGE,"E197")])]});
            hole(context, id + "F30", {"style" : HoleStyle.SIMPLE, "endStyle" : HoleEndStyle.BLIND, "oppositeDirection" : true, "holeDiameter" : 7 * mm, "holeDepth" : 4 * mm, "isTappedThrough" : true, "tappedDepth" : 12 * mm, "tapClearance" : 3, "startFromSketch" : true, "locations" : qUnion([Q0]), "scope" : qUnion([Q1])});
        }
        {
            var Q0;
            {var subQ4=sQuery(id+"F28.wireOp",EDGE,"E387");Q0=makeQuery(id+"F28.imprint","IMPRINT",FACE,{"disambiguationData":[TD([[makeQuery(id+"F28.imprint","IMPRINT",EDGE,{"derivedFrom":subQ4}),-1.0]])]});}
            var Q1;
            {var subQ4=sQuery(id+"F29.wireOp",EDGE,"E404");Q1=makeQuery(id+"F29.imprint","IMPRINT",FACE,{"disambiguationData":[TD([[makeQuery(id+"F29.imprint","IMPRINT",EDGE,{"derivedFrom":subQ4}),-1.0]])]});}
            loft(context, id + "F31", {"sheetProfilesArray" : [{ "sheetProfileEntities" : qUnion([Q0]) }, { "sheetProfileEntities" : qUnion([Q1]) }]});
        }
        {
            var Q1;
            {var subQ5=sQuery(id+"F28.wireOp",EDGE,"E388");Q1=makeQuery(id+"F28.imprint","IMPRINT",FACE,{"disambiguationData":[TD([[makeQuery(id+"F28.imprint","IMPRINT",EDGE,{"derivedFrom":subQ5}),1.0]])]});}
            var Q2;
            {var subQ5=sQuery(id+"F29.wireOp",EDGE,"E406");Q2=makeQuery(id+"F29.imprint","IMPRINT",FACE,{"disambiguationData":[TD([[makeQuery(id+"F29.imprint","IMPRINT",EDGE,{"derivedFrom":subQ5}),1.0]])]});}
            loft(context, id + "F32", {"operationType" : NewBodyOperationType.ADD, "sheetProfilesArray" : [{ "sheetProfileEntities" : qUnion([Q1]) }, { "sheetProfileEntities" : qUnion([Q2]) }]});
        }
        {
            var Q1;
            {var subQ0=sQuery(id+"F28.wireOp",EDGE,"E386");Q1=makeQuery(id+"F28.imprint","IMPRINT",FACE,{"disambiguationData":[TD([[makeQuery(id+"F28.imprint","IMPRINT",EDGE,{"derivedFrom":subQ0}),-1.0]])]});}
            var Q2;
            {var subQ0=sQuery(id+"F29.wireOp",EDGE,"E403");Q2=makeQuery(id+"F29.imprint","IMPRINT",FACE,{"disambiguationData":[TD([[makeQuery(id+"F29.imprint","IMPRINT",EDGE,{"derivedFrom":subQ0}),-1.0]])]});}
            loft(context, id + "F33", {"operationType" : NewBodyOperationType.ADD, "sheetProfilesArray" : [{ "sheetProfileEntities" : qUnion([Q1]) }, { "sheetProfileEntities" : qUnion([Q2]) }]});
        }
        {
            var Q1;
            {var subQ5=sQuery(id+"F28.wireOp",EDGE,"E384.1");Q1=makeQuery(id+"F28.imprint","IMPRINT",FACE,{"disambiguationData":[TD([[makeQuery(id+"F28.imprint","IMPRINT",EDGE,{"derivedFrom":subQ5}),-1.0]])]});}
            var Q2;
            {var subQ5=sQuery(id+"F29.wireOp",EDGE,"E401.1");Q2=makeQuery(id+"F29.imprint","IMPRINT",FACE,{"disambiguationData":[TD([[makeQuery(id+"F29.imprint","IMPRINT",EDGE,{"derivedFrom":subQ5}),-1.0]])]});}
            loft(context, id + "F34", {"operationType" : NewBodyOperationType.ADD, "sheetProfilesArray" : [{ "sheetProfileEntities" : qUnion([Q1]) }, { "sheetProfileEntities" : qUnion([Q2]) }]});
        }
        {
            var Q0;
            {var subQ0=sQuery(id+"F29.wireOp",EDGE,"E403");Q0=makeQuery(id+"F29.imprint","IMPRINT",FACE,{"disambiguationData":[TD([[makeQuery(id+"F29.imprint","IMPRINT",EDGE,{"derivedFrom":subQ0}),-1.0]])]});}
            var Q1;
            {var subQ5=sQuery(id+"F29.wireOp",EDGE,"E406");Q1=makeQuery(id+"F29.imprint","IMPRINT",FACE,{"disambiguationData":[TD([[makeQuery(id+"F29.imprint","IMPRINT",EDGE,{"derivedFrom":subQ5}),1.0]])]});}
            var Q2;
            {var subQ4=sQuery(id+"F29.wireOp",EDGE,"E404");Q2=makeQuery(id+"F29.imprint","IMPRINT",FACE,{"disambiguationData":[TD([[makeQuery(id+"F29.imprint","IMPRINT",EDGE,{"derivedFrom":subQ4}),-1.0]])]});}
            var Q3;
            {var subQ5=sQuery(id+"F29.wireOp",EDGE,"E401.1");Q3=makeQuery(id+"F29.imprint","IMPRINT",FACE,{"disambiguationData":[TD([[makeQuery(id+"F29.imprint","IMPRINT",EDGE,{"derivedFrom":subQ5}),-1.0]])]});}
            extrude(context, id + "F35", {"entities" : qUnion([Q0, Q1, Q2, Q3]), "operationType" : NewBodyOperationType.ADD, "depth" : 8 * mm});
        }
        {
            var Q0;
            {var subQ0=sQuery(id+"F8.wireOp",EDGE,"E121");var subQ1=sQuery(id+"F8.wireOp",EDGE,"E45.MirrorCS");var subQ2=sQuery(id+"F8.wireOp",EDGE,"E22.MirrorCS");var subQ3=makeQuery(id+"F16.opExtrude","CAP_FACE",FACE,{"disambiguationData":[OSD([subQ2,subQ1,sQuery(id+"F8.wireOp",EDGE,"E93"),subQ0])],"isStart":true});var subQ4=sQuery(id+"F12.wireOp",EDGE,"E323");var subQ5=sQuery(id+"F12.wireOp",EDGE,"E322");var subQ6=sQuery(id+"F12.wireOp",EDGE,"E321");var subQ7=sQuery(id+"F12.wireOp",EDGE,"E320");var subQ8=sQuery(id+"F12.wireOp",EDGE,"E319");var subQ9=sQuery(id+"F12.wireOp",EDGE,"E318");var subQ10=makeQuery(id+"F19.opExtrude","CAP_FACE",FACE,{"disambiguationData":[OSD([subQ9,subQ8,subQ7,subQ6,subQ5,subQ4])],"isStart":false});var subQ11=sQuery(id+"F8.wireOp",EDGE,"E122");var subQ12=sQuery(id+"F8.wireOp",EDGE,"E44.MirrorCS");var subQ13=sQuery(id+"F8.wireOp",EDGE,"E21.MirrorCS");var subQ14=makeQuery(id+"F16.opExtrude","CAP_FACE",FACE,{"disambiguationData":[OSD([subQ13,subQ12,sQuery(id+"F8.wireOp",EDGE,"E96"),subQ11])],"isStart":true});var subQ15=makeQuery(id+"F18.opRevolve","SWEPT_FACE",FACE,{"disambiguationData":[OSD([sQuery(id+"F9.wireOp",EDGE,"E207")])]});var subQ16=sQuery(id+"F8.wireOp",EDGE,"E123");var subQ17=sQuery(id+"F8.wireOp",EDGE,"E50");var subQ18=sQuery(id+"F8.wireOp",EDGE,"E20.MirrorCS");var subQ19=makeQuery(id+"F16.opExtrude","CAP_FACE",FACE,{"disambiguationData":[OSD([subQ18,subQ17,sQuery(id+"F8.wireOp",EDGE,"E97"),subQ16])],"isStart":true});var subQ20=sQuery(id+"F9.wireOp",EDGE,"E214");var subQ21=sQuery(id+"F9.wireOp",EDGE,"E203");var subQ22=sQuery(id+"F9.wireOp",EDGE,"E202");var subQ23=sQuery(id+"F9.wireOp",EDGE,"E201");var subQ24=makeQuery(id+"F17.opRevolve","CAP_FACE",FACE,{"disambiguationData":[OSD([subQ23,subQ22,subQ21,subQ20])],"isStart":false});var subQ25=sQuery(id+"F8.wireOp",EDGE,"E101");var subQ26=sQuery(id+"F8.wireOp",EDGE,"E42.MirrorCS");var subQ27=sQuery(id+"F8.wireOp",EDGE,"E19.MirrorCS");var subQ28=makeQuery(id+"F16.opExtrude","CAP_FACE",FACE,{"disambiguationData":[OSD([subQ27,subQ26,sQuery(id+"F8.wireOp",EDGE,"E53"),subQ25])],"isStart":true});var subQ29=sQuery(id+"F8.wireOp",EDGE,"E102");var subQ30=sQuery(id+"F8.wireOp",EDGE,"E41.MirrorCS");var subQ31=sQuery(id+"F8.wireOp",EDGE,"E18.MirrorCS");var subQ32=makeQuery(id+"F16.opExtrude","CAP_FACE",FACE,{"disambiguationData":[OSD([subQ31,subQ30,sQuery(id+"F8.wireOp",EDGE,"E55"),subQ29])],"isStart":true});var subQ33=sQuery(id+"F8.wireOp",EDGE,"E103");var subQ34=sQuery(id+"F8.wireOp",EDGE,"E40.MirrorCS");var subQ35=sQuery(id+"F8.wireOp",EDGE,"E17.MirrorCS");var subQ36=makeQuery(id+"F16.opExtrude","CAP_FACE",FACE,{"disambiguationData":[OSD([subQ35,subQ34,sQuery(id+"F8.wireOp",EDGE,"E57"),subQ33])],"isStart":true});var subQ37=sQuery(id+"F8.wireOp",EDGE,"E104");var subQ38=sQuery(id+"F8.wireOp",EDGE,"E39.MirrorCS");var subQ39=sQuery(id+"F8.wireOp",EDGE,"E16.MirrorCS");var subQ40=makeQuery(id+"F16.opExtrude","CAP_FACE",FACE,{"disambiguationData":[OSD([subQ39,subQ38,sQuery(id+"F8.wireOp",EDGE,"E59"),subQ37])],"isStart":true});var subQ41=sQuery(id+"F8.wireOp",EDGE,"E105");var subQ42=sQuery(id+"F8.wireOp",EDGE,"E27");var subQ43=sQuery(id+"F8.wireOp",EDGE,"E15.MirrorCS");var subQ44=makeQuery(id+"F16.opExtrude","CAP_FACE",FACE,{"disambiguationData":[OSD([subQ43,subQ42,sQuery(id+"F8.wireOp",EDGE,"E61"),subQ41])],"isStart":true});var subQ45=sQuery(id+"F8.wireOp",EDGE,"E117");var subQ46=sQuery(id+"F8.wireOp",EDGE,"E49");var subQ47=sQuery(id+"F8.wireOp",EDGE,"E14.MirrorCS");var subQ48=makeQuery(id+"F16.opExtrude","CAP_FACE",FACE,{"disambiguationData":[OSD([subQ47,subQ46,sQuery(id+"F8.wireOp",EDGE,"E85"),subQ45])],"isStart":true});var subQ49=sQuery(id+"F8.wireOp",EDGE,"E116");var subQ50=sQuery(id+"F8.wireOp",EDGE,"E38.MirrorCS");var subQ51=sQuery(id+"F8.wireOp",EDGE,"E13.MirrorCS");var subQ52=makeQuery(id+"F16.opExtrude","CAP_FACE",FACE,{"disambiguationData":[OSD([subQ51,subQ50,sQuery(id+"F8.wireOp",EDGE,"E83"),subQ49])],"isStart":true});var subQ53=sQuery(id+"F8.wireOp",EDGE,"E115");var subQ54=sQuery(id+"F8.wireOp",EDGE,"E37.MirrorCS");var subQ55=sQuery(id+"F8.wireOp",EDGE,"E12.MirrorCS");var subQ56=makeQuery(id+"F16.opExtrude","CAP_FACE",FACE,{"disambiguationData":[OSD([subQ55,subQ54,sQuery(id+"F8.wireOp",EDGE,"E81"),subQ53])],"isStart":true});var subQ57=sQuery(id+"F8.wireOp",EDGE,"E114");var subQ58=sQuery(id+"F8.wireOp",EDGE,"E36.MirrorCS");var subQ59=sQuery(id+"F8.wireOp",EDGE,"E11.MirrorCS");var subQ60=makeQuery(id+"F16.opExtrude","CAP_FACE",FACE,{"disambiguationData":[OSD([subQ59,subQ58,sQuery(id+"F8.wireOp",EDGE,"E79"),subQ57])],"isStart":true});var subQ61=sQuery(id+"F8.wireOp",EDGE,"E107");var subQ62=sQuery(id+"F8.wireOp",EDGE,"E29");var subQ63=sQuery(id+"F8.wireOp",EDGE,"E4");var subQ64=makeQuery(id+"F16.opExtrude","CAP_FACE",FACE,{"disambiguationData":[OSD([subQ63,subQ62,sQuery(id+"F8.wireOp",EDGE,"E65"),subQ61])],"isStart":true});var subQ65=makeQuery(id+"F17.opRevolve","CAP_FACE",FACE,{"disambiguationData":[OSD([subQ23,subQ22,subQ21,subQ20])],"isStart":true});var subQ66=sQuery(id+"F8.wireOp",EDGE,"E106");var subQ67=sQuery(id+"F8.wireOp",EDGE,"E28");var subQ68=sQuery(id+"F8.wireOp",EDGE,"E3");var subQ69=makeQuery(id+"F16.opExtrude","CAP_FACE",FACE,{"disambiguationData":[OSD([subQ68,subQ67,sQuery(id+"F8.wireOp",EDGE,"E63"),subQ66])],"isStart":true});var subQ70=sQuery(id+"F8.wireOp",EDGE,"E120");var subQ71=sQuery(id+"F8.wireOp",EDGE,"E119");var subQ72=sQuery(id+"F8.wireOp",EDGE,"E118");var subQ73=sQuery(id+"F8.wireOp",EDGE,"E113");var subQ74=sQuery(id+"F8.wireOp",EDGE,"E112");var subQ75=sQuery(id+"F8.wireOp",EDGE,"E111");var subQ76=sQuery(id+"F8.wireOp",EDGE,"E110");var subQ77=sQuery(id+"F8.wireOp",EDGE,"E109");var subQ78=sQuery(id+"F8.wireOp",EDGE,"E108");var subQ79=sQuery(id+"F8.wireOp",EDGE,"E100");var subQ80=sQuery(id+"F8.wireOp",EDGE,"E98");var subQ81=sQuery(id+"F8.wireOp",EDGE,"E95");var subQ82=sQuery(id+"F8.wireOp",EDGE,"E94");var subQ83=sQuery(id+"F8.wireOp",EDGE,"E92");var subQ84=sQuery(id+"F8.wireOp",EDGE,"E90");var subQ85=sQuery(id+"F8.wireOp",EDGE,"E88");var subQ86=sQuery(id+"F8.wireOp",EDGE,"E86");var subQ87=sQuery(id+"F8.wireOp",EDGE,"E84");var subQ88=sQuery(id+"F8.wireOp",EDGE,"E82");var subQ89=sQuery(id+"F8.wireOp",EDGE,"E80");var subQ90=sQuery(id+"F8.wireOp",EDGE,"E78");var subQ91=sQuery(id+"F8.wireOp",EDGE,"E76");var subQ92=sQuery(id+"F8.wireOp",EDGE,"E74");var subQ93=sQuery(id+"F8.wireOp",EDGE,"E72");var subQ94=sQuery(id+"F8.wireOp",EDGE,"E70");var subQ95=sQuery(id+"F8.wireOp",EDGE,"E68");var subQ96=sQuery(id+"F8.wireOp",EDGE,"E66");var subQ97=sQuery(id+"F8.wireOp",EDGE,"E64");var subQ98=sQuery(id+"F8.wireOp",EDGE,"E62");var subQ99=sQuery(id+"F8.wireOp",EDGE,"E60");var subQ100=sQuery(id+"F8.wireOp",EDGE,"E58");var subQ101=sQuery(id+"F8.wireOp",EDGE,"E56");var subQ102=sQuery(id+"F8.wireOp",EDGE,"E54");var subQ103=sQuery(id+"F8.wireOp",EDGE,"E52");var subQ104=sQuery(id+"F8.wireOp",EDGE,"E48.MirrorCS");var subQ105=sQuery(id+"F8.wireOp",EDGE,"E47.MirrorCS");var subQ106=sQuery(id+"F8.wireOp",EDGE,"E46.MirrorCS");var subQ107=sQuery(id+"F8.wireOp",EDGE,"E43.MirrorCS");var subQ108=sQuery(id+"F8.wireOp",EDGE,"E35.MirrorCS");var subQ109=sQuery(id+"F8.wireOp",EDGE,"E34.MirrorCS");var subQ110=sQuery(id+"F8.wireOp",EDGE,"E33");var subQ111=sQuery(id+"F8.wireOp",EDGE,"E32");var subQ112=sQuery(id+"F8.wireOp",EDGE,"E31");var subQ113=sQuery(id+"F8.wireOp",EDGE,"E30");var subQ114=sQuery(id+"F8.wireOp",EDGE,"E26");var subQ115=sQuery(id+"F8.wireOp",EDGE,"E25");var subQ116=sQuery(id+"F8.wireOp",EDGE,"E24.MirrorCS");var subQ117=sQuery(id+"F8.wireOp",EDGE,"E23.MirrorCS");var subQ118=sQuery(id+"F8.wireOp",EDGE,"E10.MirrorCS");var subQ119=sQuery(id+"F8.wireOp",EDGE,"E9");var subQ120=sQuery(id+"F8.wireOp",EDGE,"E8");var subQ121=sQuery(id+"F8.wireOp",EDGE,"E7");var subQ122=sQuery(id+"F8.wireOp",EDGE,"E6");var subQ123=sQuery(id+"F8.wireOp",EDGE,"E5");var subQ124=sQuery(id+"F8.wireOp",EDGE,"E1.0");var subQ125=makeQuery(id+"F15.opExtrude","CAP_FACE",FACE,{"disambiguationData":[OSD([subQ124,subQ68,subQ63,subQ123,subQ122,subQ121,subQ120,subQ119,subQ118,subQ59,subQ55,subQ51,subQ47,subQ43,subQ39,subQ35,subQ31,subQ27,subQ18,subQ13,subQ2,subQ117,subQ116,subQ115,subQ114,subQ42,subQ67,subQ62,subQ113,subQ112,subQ111,subQ110,subQ109,subQ108,subQ58,subQ54,subQ50,subQ38,subQ34,subQ30,subQ26,subQ107,subQ12,subQ1,subQ106,subQ105,subQ104,subQ46,subQ17,subQ103,subQ102,subQ101,subQ100,subQ99,subQ98,subQ97,subQ96,subQ95,subQ94,subQ93,subQ92,subQ91,subQ90,subQ89,subQ88,subQ87,subQ86,subQ85,subQ84,subQ83,subQ82,subQ81,subQ80,subQ79,subQ25,subQ29,subQ33,subQ37,subQ41,subQ66,subQ61,subQ78,subQ77,subQ76,subQ75,subQ74,subQ73,subQ57,subQ53,subQ49,subQ45,subQ72,subQ71,subQ70,subQ0,subQ11,subQ16])],"isStart":true});var subQ126=makeQuery(id+"F16.opExtrude","CAP_FACE",FACE,{"disambiguationData":[OSD([subQ114,subQ107,sQuery(id+"F8.wireOp",EDGE,"E99"),subQ79])],"isStart":true});var subQ127=makeQuery(id+"F16.opExtrude","CAP_FACE",FACE,{"disambiguationData":[OSD([subQ119,subQ109,sQuery(id+"F8.wireOp",EDGE,"E75"),subQ74])],"isStart":true});var subQ129=makeQuery(id+"F16.opExtrude","CAP_FACE",FACE,{"disambiguationData":[OSD([subQ123,subQ113,sQuery(id+"F8.wireOp",EDGE,"E67"),subQ78])],"isStart":true});var subQ130=makeQuery(id+"F16.opExtrude","CAP_FACE",FACE,{"disambiguationData":[OSD([subQ122,subQ112,sQuery(id+"F8.wireOp",EDGE,"E69"),subQ77])],"isStart":true});var subQ131=makeQuery(id+"F19.opExtrude","CAP_FACE",FACE,{"disambiguationData":[OSD([subQ9,subQ8,subQ7,subQ6,subQ5,subQ4])],"isStart":true});var subQ132=makeQuery(id+"F16.opExtrude","CAP_FACE",FACE,{"disambiguationData":[OSD([subQ121,subQ111,sQuery(id+"F8.wireOp",EDGE,"E71"),subQ76])],"isStart":true});var subQ133=makeQuery(id+"F19.opExtrude","SWEPT_FACE",FACE,{"disambiguationData":[OSD([subQ7])]});var subQ139=makeQuery(id+"F15.opExtrude","CAP_FACE",FACE,{"disambiguationData":[OSD([subQ124,subQ68,subQ63,subQ123,subQ122,subQ121,subQ120,subQ119,subQ118,subQ59,subQ55,subQ51,subQ47,subQ43,subQ39,subQ35,subQ31,subQ27,subQ18,subQ13,subQ2,subQ117,subQ116,subQ115,subQ114,subQ42,subQ67,subQ62,subQ113,subQ112,subQ111,subQ110,subQ109,subQ108,subQ58,subQ54,subQ50,subQ38,subQ34,subQ30,subQ26,subQ107,subQ12,subQ1,subQ106,subQ105,subQ104,subQ46,subQ17,subQ103,subQ102,subQ101,subQ100,subQ99,subQ98,subQ97,subQ96,subQ95,subQ94,subQ93,subQ92,subQ91,subQ90,subQ89,subQ88,subQ87,subQ86,subQ85,subQ84,subQ83,subQ82,subQ81,subQ80,subQ79,subQ25,subQ29,subQ33,subQ37,subQ41,subQ66,subQ61,subQ78,subQ77,subQ76,subQ75,subQ74,subQ73,subQ57,subQ53,subQ49,subQ45,subQ72,subQ71,subQ70,subQ0,subQ11,subQ16])],"isStart":false});var subQ140=makeQuery(id+"F16.opExtrude","CAP_FACE",FACE,{"disambiguationData":[OSD([subQ120,subQ110,sQuery(id+"F8.wireOp",EDGE,"E73"),subQ75])],"isStart":true});var subQ141=makeQuery(id+"F19.opExtrude","SWEPT_FACE",FACE,{"disambiguationData":[OSD([subQ4])]});var subQ142=makeQuery(id+"F16.opExtrude","CAP_FACE",FACE,{"disambiguationData":[OSD([subQ118,subQ108,sQuery(id+"F8.wireOp",EDGE,"E77"),subQ73])],"isStart":true});var subQ143=makeQuery(id+"F16.opExtrude","CAP_FACE",FACE,{"disambiguationData":[OSD([subQ117,subQ106,sQuery(id+"F8.wireOp",EDGE,"E91"),subQ70])],"isStart":true});var subQ144=makeQuery(id+"F16.opExtrude","CAP_FACE",FACE,{"disambiguationData":[OSD([subQ116,subQ105,sQuery(id+"F8.wireOp",EDGE,"E89"),subQ71])],"isStart":true});var subQ145=makeQuery(id+"F16.opExtrude","CAP_FACE",FACE,{"disambiguationData":[OSD([subQ115,subQ104,sQuery(id+"F8.wireOp",EDGE,"E87"),subQ72])],"isStart":true});var subQ146=makeQuery(id+"F18.opRevolve","SWEPT_FACE",FACE,{"disambiguationData":[OSD([subQ20])]});var subQ147=makeQuery(id+"F19.opExtrude","SWEPT_FACE",FACE,{"disambiguationData":[OSD([subQ8])]});var subQ148=makeQuery(id+"F19.opExtrude","SWEPT_FACE",FACE,{"disambiguationData":[OSD([subQ5])]});Q0=makeQuery(id+"F21.boolean.opBoolean","INTERSECT",EDGE,{"derivedFrom":[makeQuery(id+"F20.boolean.opBoolean","SPLIT",FACE,{"disambiguationData":[TD([subQ15])],"derivedFrom":makeQuery(id+"F19.boolean.opBoolean","SPLIT",FACE,{"disambiguationData":[TD([makeQuery(id+"F15.opExtrude","SWEPT_FACE",FACE,{"disambiguationData":[OSD([subQ124])]}),subQ125,subQ139,subQ69,subQ64,subQ129,subQ130,subQ132,subQ140,subQ127,subQ142,subQ60,subQ56,subQ52,subQ48,subQ44,subQ40,subQ36,subQ32,subQ28,subQ19,subQ14,subQ3,subQ143,subQ144,subQ145,subQ126,subQ65,subQ24,subQ15,subQ146,subQ131,subQ10,subQ147,subQ133,subQ148,subQ141])],"derivedFrom":makeQuery(id+"F18.boolean.opBoolean","MERGE",FACE,{"derivedFrom":[makeQuery(id+"F17.opRevolve","SWEPT_FACE",FACE,{"disambiguationData":[OSD([subQ23])]}),makeQuery(id+"F18.opRevolve","SWEPT_FACE",FACE,{"disambiguationData":[OSD([subQ23])]})]})})}),makeQuery(id+"F21.opExtrude","SWEPT_FACE",FACE,{"disambiguationData":[OSD([sQuery(id+"F13.wireOp",EDGE,"E328.MirrorCS")])]})]});}
            var Q1;
            {var subQ0=sQuery(id+"F8.wireOp",EDGE,"E121");var subQ1=sQuery(id+"F8.wireOp",EDGE,"E45.MirrorCS");var subQ2=sQuery(id+"F8.wireOp",EDGE,"E22.MirrorCS");var subQ3=makeQuery(id+"F16.opExtrude","CAP_FACE",FACE,{"disambiguationData":[OSD([subQ2,subQ1,sQuery(id+"F8.wireOp",EDGE,"E93"),subQ0])],"isStart":true});var subQ4=sQuery(id+"F12.wireOp",EDGE,"E323");var subQ5=sQuery(id+"F12.wireOp",EDGE,"E322");var subQ6=sQuery(id+"F12.wireOp",EDGE,"E321");var subQ7=sQuery(id+"F12.wireOp",EDGE,"E320");var subQ8=sQuery(id+"F12.wireOp",EDGE,"E319");var subQ9=sQuery(id+"F12.wireOp",EDGE,"E318");var subQ10=makeQuery(id+"F19.opExtrude","CAP_FACE",FACE,{"disambiguationData":[OSD([subQ9,subQ8,subQ7,subQ6,subQ5,subQ4])],"isStart":false});var subQ11=sQuery(id+"F8.wireOp",EDGE,"E122");var subQ12=sQuery(id+"F8.wireOp",EDGE,"E44.MirrorCS");var subQ13=sQuery(id+"F8.wireOp",EDGE,"E21.MirrorCS");var subQ14=makeQuery(id+"F16.opExtrude","CAP_FACE",FACE,{"disambiguationData":[OSD([subQ13,subQ12,sQuery(id+"F8.wireOp",EDGE,"E96"),subQ11])],"isStart":true});var subQ15=makeQuery(id+"F18.opRevolve","SWEPT_FACE",FACE,{"disambiguationData":[OSD([sQuery(id+"F9.wireOp",EDGE,"E207")])]});var subQ16=sQuery(id+"F8.wireOp",EDGE,"E123");var subQ17=sQuery(id+"F8.wireOp",EDGE,"E50");var subQ18=sQuery(id+"F8.wireOp",EDGE,"E20.MirrorCS");var subQ19=makeQuery(id+"F16.opExtrude","CAP_FACE",FACE,{"disambiguationData":[OSD([subQ18,subQ17,sQuery(id+"F8.wireOp",EDGE,"E97"),subQ16])],"isStart":true});var subQ20=sQuery(id+"F9.wireOp",EDGE,"E214");var subQ21=sQuery(id+"F9.wireOp",EDGE,"E203");var subQ22=sQuery(id+"F9.wireOp",EDGE,"E202");var subQ23=sQuery(id+"F9.wireOp",EDGE,"E201");var subQ24=makeQuery(id+"F17.opRevolve","CAP_FACE",FACE,{"disambiguationData":[OSD([subQ23,subQ22,subQ21,subQ20])],"isStart":false});var subQ25=sQuery(id+"F8.wireOp",EDGE,"E101");var subQ26=sQuery(id+"F8.wireOp",EDGE,"E42.MirrorCS");var subQ27=sQuery(id+"F8.wireOp",EDGE,"E19.MirrorCS");var subQ28=makeQuery(id+"F16.opExtrude","CAP_FACE",FACE,{"disambiguationData":[OSD([subQ27,subQ26,sQuery(id+"F8.wireOp",EDGE,"E53"),subQ25])],"isStart":true});var subQ29=sQuery(id+"F8.wireOp",EDGE,"E102");var subQ30=sQuery(id+"F8.wireOp",EDGE,"E41.MirrorCS");var subQ31=sQuery(id+"F8.wireOp",EDGE,"E18.MirrorCS");var subQ32=makeQuery(id+"F16.opExtrude","CAP_FACE",FACE,{"disambiguationData":[OSD([subQ31,subQ30,sQuery(id+"F8.wireOp",EDGE,"E55"),subQ29])],"isStart":true});var subQ33=sQuery(id+"F8.wireOp",EDGE,"E103");var subQ34=sQuery(id+"F8.wireOp",EDGE,"E40.MirrorCS");var subQ35=sQuery(id+"F8.wireOp",EDGE,"E17.MirrorCS");var subQ36=makeQuery(id+"F16.opExtrude","CAP_FACE",FACE,{"disambiguationData":[OSD([subQ35,subQ34,sQuery(id+"F8.wireOp",EDGE,"E57"),subQ33])],"isStart":true});var subQ37=sQuery(id+"F8.wireOp",EDGE,"E104");var subQ38=sQuery(id+"F8.wireOp",EDGE,"E39.MirrorCS");var subQ39=sQuery(id+"F8.wireOp",EDGE,"E16.MirrorCS");var subQ40=makeQuery(id+"F16.opExtrude","CAP_FACE",FACE,{"disambiguationData":[OSD([subQ39,subQ38,sQuery(id+"F8.wireOp",EDGE,"E59"),subQ37])],"isStart":true});var subQ41=sQuery(id+"F8.wireOp",EDGE,"E105");var subQ42=sQuery(id+"F8.wireOp",EDGE,"E27");var subQ43=sQuery(id+"F8.wireOp",EDGE,"E15.MirrorCS");var subQ44=makeQuery(id+"F16.opExtrude","CAP_FACE",FACE,{"disambiguationData":[OSD([subQ43,subQ42,sQuery(id+"F8.wireOp",EDGE,"E61"),subQ41])],"isStart":true});var subQ45=sQuery(id+"F8.wireOp",EDGE,"E117");var subQ46=sQuery(id+"F8.wireOp",EDGE,"E49");var subQ47=sQuery(id+"F8.wireOp",EDGE,"E14.MirrorCS");var subQ48=makeQuery(id+"F16.opExtrude","CAP_FACE",FACE,{"disambiguationData":[OSD([subQ47,subQ46,sQuery(id+"F8.wireOp",EDGE,"E85"),subQ45])],"isStart":true});var subQ49=sQuery(id+"F8.wireOp",EDGE,"E116");var subQ50=sQuery(id+"F8.wireOp",EDGE,"E38.MirrorCS");var subQ51=sQuery(id+"F8.wireOp",EDGE,"E13.MirrorCS");var subQ52=makeQuery(id+"F16.opExtrude","CAP_FACE",FACE,{"disambiguationData":[OSD([subQ51,subQ50,sQuery(id+"F8.wireOp",EDGE,"E83"),subQ49])],"isStart":true});var subQ53=sQuery(id+"F8.wireOp",EDGE,"E115");var subQ54=sQuery(id+"F8.wireOp",EDGE,"E37.MirrorCS");var subQ55=sQuery(id+"F8.wireOp",EDGE,"E12.MirrorCS");var subQ56=makeQuery(id+"F16.opExtrude","CAP_FACE",FACE,{"disambiguationData":[OSD([subQ55,subQ54,sQuery(id+"F8.wireOp",EDGE,"E81"),subQ53])],"isStart":true});var subQ57=sQuery(id+"F8.wireOp",EDGE,"E114");var subQ58=sQuery(id+"F8.wireOp",EDGE,"E36.MirrorCS");var subQ59=sQuery(id+"F8.wireOp",EDGE,"E11.MirrorCS");var subQ60=makeQuery(id+"F16.opExtrude","CAP_FACE",FACE,{"disambiguationData":[OSD([subQ59,subQ58,sQuery(id+"F8.wireOp",EDGE,"E79"),subQ57])],"isStart":true});var subQ61=sQuery(id+"F8.wireOp",EDGE,"E107");var subQ62=sQuery(id+"F8.wireOp",EDGE,"E29");var subQ63=sQuery(id+"F8.wireOp",EDGE,"E4");var subQ64=makeQuery(id+"F16.opExtrude","CAP_FACE",FACE,{"disambiguationData":[OSD([subQ63,subQ62,sQuery(id+"F8.wireOp",EDGE,"E65"),subQ61])],"isStart":true});var subQ65=makeQuery(id+"F17.opRevolve","CAP_FACE",FACE,{"disambiguationData":[OSD([subQ23,subQ22,subQ21,subQ20])],"isStart":true});var subQ66=sQuery(id+"F8.wireOp",EDGE,"E106");var subQ67=sQuery(id+"F8.wireOp",EDGE,"E28");var subQ68=sQuery(id+"F8.wireOp",EDGE,"E3");var subQ69=makeQuery(id+"F16.opExtrude","CAP_FACE",FACE,{"disambiguationData":[OSD([subQ68,subQ67,sQuery(id+"F8.wireOp",EDGE,"E63"),subQ66])],"isStart":true});var subQ70=sQuery(id+"F8.wireOp",EDGE,"E120");var subQ71=sQuery(id+"F8.wireOp",EDGE,"E119");var subQ72=sQuery(id+"F8.wireOp",EDGE,"E118");var subQ73=sQuery(id+"F8.wireOp",EDGE,"E113");var subQ74=sQuery(id+"F8.wireOp",EDGE,"E112");var subQ75=sQuery(id+"F8.wireOp",EDGE,"E111");var subQ76=sQuery(id+"F8.wireOp",EDGE,"E110");var subQ77=sQuery(id+"F8.wireOp",EDGE,"E109");var subQ78=sQuery(id+"F8.wireOp",EDGE,"E108");var subQ79=sQuery(id+"F8.wireOp",EDGE,"E100");var subQ80=sQuery(id+"F8.wireOp",EDGE,"E98");var subQ81=sQuery(id+"F8.wireOp",EDGE,"E95");var subQ82=sQuery(id+"F8.wireOp",EDGE,"E94");var subQ83=sQuery(id+"F8.wireOp",EDGE,"E92");var subQ84=sQuery(id+"F8.wireOp",EDGE,"E90");var subQ85=sQuery(id+"F8.wireOp",EDGE,"E88");var subQ86=sQuery(id+"F8.wireOp",EDGE,"E86");var subQ87=sQuery(id+"F8.wireOp",EDGE,"E84");var subQ88=sQuery(id+"F8.wireOp",EDGE,"E82");var subQ89=sQuery(id+"F8.wireOp",EDGE,"E80");var subQ90=sQuery(id+"F8.wireOp",EDGE,"E78");var subQ91=sQuery(id+"F8.wireOp",EDGE,"E76");var subQ92=sQuery(id+"F8.wireOp",EDGE,"E74");var subQ93=sQuery(id+"F8.wireOp",EDGE,"E72");var subQ94=sQuery(id+"F8.wireOp",EDGE,"E70");var subQ95=sQuery(id+"F8.wireOp",EDGE,"E68");var subQ96=sQuery(id+"F8.wireOp",EDGE,"E66");var subQ97=sQuery(id+"F8.wireOp",EDGE,"E64");var subQ98=sQuery(id+"F8.wireOp",EDGE,"E62");var subQ99=sQuery(id+"F8.wireOp",EDGE,"E60");var subQ100=sQuery(id+"F8.wireOp",EDGE,"E58");var subQ101=sQuery(id+"F8.wireOp",EDGE,"E56");var subQ102=sQuery(id+"F8.wireOp",EDGE,"E54");var subQ103=sQuery(id+"F8.wireOp",EDGE,"E52");var subQ104=sQuery(id+"F8.wireOp",EDGE,"E48.MirrorCS");var subQ105=sQuery(id+"F8.wireOp",EDGE,"E47.MirrorCS");var subQ106=sQuery(id+"F8.wireOp",EDGE,"E46.MirrorCS");var subQ107=sQuery(id+"F8.wireOp",EDGE,"E43.MirrorCS");var subQ108=sQuery(id+"F8.wireOp",EDGE,"E35.MirrorCS");var subQ109=sQuery(id+"F8.wireOp",EDGE,"E34.MirrorCS");var subQ110=sQuery(id+"F8.wireOp",EDGE,"E33");var subQ111=sQuery(id+"F8.wireOp",EDGE,"E32");var subQ112=sQuery(id+"F8.wireOp",EDGE,"E31");var subQ113=sQuery(id+"F8.wireOp",EDGE,"E30");var subQ114=sQuery(id+"F8.wireOp",EDGE,"E26");var subQ115=sQuery(id+"F8.wireOp",EDGE,"E25");var subQ116=sQuery(id+"F8.wireOp",EDGE,"E24.MirrorCS");var subQ117=sQuery(id+"F8.wireOp",EDGE,"E23.MirrorCS");var subQ118=sQuery(id+"F8.wireOp",EDGE,"E10.MirrorCS");var subQ119=sQuery(id+"F8.wireOp",EDGE,"E9");var subQ120=sQuery(id+"F8.wireOp",EDGE,"E8");var subQ121=sQuery(id+"F8.wireOp",EDGE,"E7");var subQ122=sQuery(id+"F8.wireOp",EDGE,"E6");var subQ123=sQuery(id+"F8.wireOp",EDGE,"E5");var subQ124=sQuery(id+"F8.wireOp",EDGE,"E1.0");var subQ125=makeQuery(id+"F15.opExtrude","CAP_FACE",FACE,{"disambiguationData":[OSD([subQ124,subQ68,subQ63,subQ123,subQ122,subQ121,subQ120,subQ119,subQ118,subQ59,subQ55,subQ51,subQ47,subQ43,subQ39,subQ35,subQ31,subQ27,subQ18,subQ13,subQ2,subQ117,subQ116,subQ115,subQ114,subQ42,subQ67,subQ62,subQ113,subQ112,subQ111,subQ110,subQ109,subQ108,subQ58,subQ54,subQ50,subQ38,subQ34,subQ30,subQ26,subQ107,subQ12,subQ1,subQ106,subQ105,subQ104,subQ46,subQ17,subQ103,subQ102,subQ101,subQ100,subQ99,subQ98,subQ97,subQ96,subQ95,subQ94,subQ93,subQ92,subQ91,subQ90,subQ89,subQ88,subQ87,subQ86,subQ85,subQ84,subQ83,subQ82,subQ81,subQ80,subQ79,subQ25,subQ29,subQ33,subQ37,subQ41,subQ66,subQ61,subQ78,subQ77,subQ76,subQ75,subQ74,subQ73,subQ57,subQ53,subQ49,subQ45,subQ72,subQ71,subQ70,subQ0,subQ11,subQ16])],"isStart":true});var subQ126=makeQuery(id+"F16.opExtrude","CAP_FACE",FACE,{"disambiguationData":[OSD([subQ114,subQ107,sQuery(id+"F8.wireOp",EDGE,"E99"),subQ79])],"isStart":true});var subQ127=makeQuery(id+"F16.opExtrude","CAP_FACE",FACE,{"disambiguationData":[OSD([subQ119,subQ109,sQuery(id+"F8.wireOp",EDGE,"E75"),subQ74])],"isStart":true});var subQ129=makeQuery(id+"F16.opExtrude","CAP_FACE",FACE,{"disambiguationData":[OSD([subQ123,subQ113,sQuery(id+"F8.wireOp",EDGE,"E67"),subQ78])],"isStart":true});var subQ130=makeQuery(id+"F16.opExtrude","CAP_FACE",FACE,{"disambiguationData":[OSD([subQ122,subQ112,sQuery(id+"F8.wireOp",EDGE,"E69"),subQ77])],"isStart":true});var subQ131=makeQuery(id+"F19.opExtrude","CAP_FACE",FACE,{"disambiguationData":[OSD([subQ9,subQ8,subQ7,subQ6,subQ5,subQ4])],"isStart":true});var subQ132=makeQuery(id+"F16.opExtrude","CAP_FACE",FACE,{"disambiguationData":[OSD([subQ121,subQ111,sQuery(id+"F8.wireOp",EDGE,"E71"),subQ76])],"isStart":true});var subQ133=makeQuery(id+"F19.opExtrude","SWEPT_FACE",FACE,{"disambiguationData":[OSD([subQ7])]});var subQ139=makeQuery(id+"F15.opExtrude","CAP_FACE",FACE,{"disambiguationData":[OSD([subQ124,subQ68,subQ63,subQ123,subQ122,subQ121,subQ120,subQ119,subQ118,subQ59,subQ55,subQ51,subQ47,subQ43,subQ39,subQ35,subQ31,subQ27,subQ18,subQ13,subQ2,subQ117,subQ116,subQ115,subQ114,subQ42,subQ67,subQ62,subQ113,subQ112,subQ111,subQ110,subQ109,subQ108,subQ58,subQ54,subQ50,subQ38,subQ34,subQ30,subQ26,subQ107,subQ12,subQ1,subQ106,subQ105,subQ104,subQ46,subQ17,subQ103,subQ102,subQ101,subQ100,subQ99,subQ98,subQ97,subQ96,subQ95,subQ94,subQ93,subQ92,subQ91,subQ90,subQ89,subQ88,subQ87,subQ86,subQ85,subQ84,subQ83,subQ82,subQ81,subQ80,subQ79,subQ25,subQ29,subQ33,subQ37,subQ41,subQ66,subQ61,subQ78,subQ77,subQ76,subQ75,subQ74,subQ73,subQ57,subQ53,subQ49,subQ45,subQ72,subQ71,subQ70,subQ0,subQ11,subQ16])],"isStart":false});var subQ140=makeQuery(id+"F16.opExtrude","CAP_FACE",FACE,{"disambiguationData":[OSD([subQ120,subQ110,sQuery(id+"F8.wireOp",EDGE,"E73"),subQ75])],"isStart":true});var subQ141=makeQuery(id+"F19.opExtrude","SWEPT_FACE",FACE,{"disambiguationData":[OSD([subQ4])]});var subQ142=makeQuery(id+"F16.opExtrude","CAP_FACE",FACE,{"disambiguationData":[OSD([subQ118,subQ108,sQuery(id+"F8.wireOp",EDGE,"E77"),subQ73])],"isStart":true});var subQ143=makeQuery(id+"F16.opExtrude","CAP_FACE",FACE,{"disambiguationData":[OSD([subQ117,subQ106,sQuery(id+"F8.wireOp",EDGE,"E91"),subQ70])],"isStart":true});var subQ144=makeQuery(id+"F16.opExtrude","CAP_FACE",FACE,{"disambiguationData":[OSD([subQ116,subQ105,sQuery(id+"F8.wireOp",EDGE,"E89"),subQ71])],"isStart":true});var subQ145=makeQuery(id+"F16.opExtrude","CAP_FACE",FACE,{"disambiguationData":[OSD([subQ115,subQ104,sQuery(id+"F8.wireOp",EDGE,"E87"),subQ72])],"isStart":true});var subQ146=makeQuery(id+"F18.opRevolve","SWEPT_FACE",FACE,{"disambiguationData":[OSD([subQ20])]});var subQ147=makeQuery(id+"F19.opExtrude","SWEPT_FACE",FACE,{"disambiguationData":[OSD([subQ8])]});var subQ148=makeQuery(id+"F19.opExtrude","SWEPT_FACE",FACE,{"disambiguationData":[OSD([subQ5])]});Q1=makeQuery(id+"F21.boolean.opBoolean","INTERSECT",EDGE,{"derivedFrom":[makeQuery(id+"F20.boolean.opBoolean","SPLIT",FACE,{"disambiguationData":[TD([subQ15])],"derivedFrom":makeQuery(id+"F19.boolean.opBoolean","SPLIT",FACE,{"disambiguationData":[TD([makeQuery(id+"F15.opExtrude","SWEPT_FACE",FACE,{"disambiguationData":[OSD([subQ124])]}),subQ125,subQ139,subQ69,subQ64,subQ129,subQ130,subQ132,subQ140,subQ127,subQ142,subQ60,subQ56,subQ52,subQ48,subQ44,subQ40,subQ36,subQ32,subQ28,subQ19,subQ14,subQ3,subQ143,subQ144,subQ145,subQ126,subQ65,subQ24,subQ15,subQ146,subQ131,subQ10,subQ147,subQ133,subQ148,subQ141])],"derivedFrom":makeQuery(id+"F18.boolean.opBoolean","MERGE",FACE,{"derivedFrom":[makeQuery(id+"F17.opRevolve","SWEPT_FACE",FACE,{"disambiguationData":[OSD([subQ23])]}),makeQuery(id+"F18.opRevolve","SWEPT_FACE",FACE,{"disambiguationData":[OSD([subQ23])]})]})})}),makeQuery(id+"F21.opExtrude","SWEPT_FACE",FACE,{"disambiguationData":[OSD([sQuery(id+"F13.wireOp",EDGE,"E327.MirrorCS")])]})]});}
            fillet(context, id + "F36", {"entities" : qUnion([Q0, Q1]), "radius" : 5 * mm, "tangentPropagation" : true, "allowEdgeOverflow" : false});
        }
        {
            var Q0;
            Q0=makeQuery(id+"F24.boolean.opBoolean","MERGE",EDGE,{"derivedFrom":[makeQuery(id+"F23.opExtrude","SWEPT_EDGE",EDGE,{"disambiguationData":[OSD([sQuery(id+"F13.wireOp",EDGE,"E339"),sQuery(id+"F13.wireOp",EDGE,"E340")])]}),makeQuery(id+"F24.opExtrude","SWEPT_EDGE",EDGE,{"disambiguationData":[OSD([sQuery(id+"F14.wireOp",EDGE,"E361"),sQuery(id+"F14.wireOp",EDGE,"E362")])]})]});
            var Q1;
            Q1=makeQuery(id+"F24.boolean.opBoolean","MERGE",EDGE,{"derivedFrom":[makeQuery(id+"F23.opExtrude","SWEPT_EDGE",EDGE,{"disambiguationData":[OSD([sQuery(id+"F13.wireOp",EDGE,"E340"),sQuery(id+"F13.wireOp",EDGE,"E341")])]}),makeQuery(id+"F24.opExtrude","SWEPT_EDGE",EDGE,{"disambiguationData":[OSD([sQuery(id+"F14.wireOp",EDGE,"E362"),sQuery(id+"F14.wireOp",EDGE,"E363")])]})]});
            var Q2;
            Q2=makeQuery(id+"F24.opExtrude","SWEPT_EDGE",EDGE,{"disambiguationData":[OSD([sQuery(id+"F14.wireOp",EDGE,"E350.MirrorCS"),sQuery(id+"F14.wireOp",EDGE,"E365.0")])]});
            var Q3;
            Q3=makeQuery(id+"F24.opExtrude","SWEPT_EDGE",EDGE,{"disambiguationData":[OSD([sQuery(id+"F14.wireOp",EDGE,"E349.MirrorCS"),sQuery(id+"F14.wireOp",EDGE,"E365.0")])]});
            var Q4;
            Q4=makeQuery(id+"F23.opExtrude","CAP_EDGE",EDGE,{"disambiguationData":[OSD([sQuery(id+"F13.wireOp",EDGE,"E340")])],"isStart":true});
            var Q5;
            Q5=makeQuery(id+"F23.opExtrude","CAP_EDGE",EDGE,{"disambiguationData":[OSD([sQuery(id+"F13.wireOp",EDGE,"E341")])],"isStart":true});
            var Q6;
            Q6=makeQuery(id+"F23.opExtrude","CAP_EDGE",EDGE,{"disambiguationData":[OSD([sQuery(id+"F13.wireOp",EDGE,"E339")])],"isStart":true});
            var Q7;
            {var subQ3=sQuery(id+"F11.wireOp",EDGE,"E298");var subQ4=sQuery(id+"F11.wireOp",EDGE,"E297");var subQ8=sQuery(id+"F9.wireOp",EDGE,"E201");var subQ9=makeQuery(id+"F18.opRevolve","SWEPT_FACE",FACE,{"disambiguationData":[OSD([subQ8])]});var subQ10=makeQuery(id+"F17.opRevolve","SWEPT_FACE",FACE,{"disambiguationData":[OSD([subQ8])]});var subQ11=makeQuery(id+"F20.opExtrude","SWEPT_FACE",FACE,{"disambiguationData":[OSD([subQ4])]});var subQ12=makeQuery(id+"F21.opExtrude","SWEPT_FACE",FACE,{"disambiguationData":[OSD([sQuery(id+"F13.wireOp",EDGE,"E328.MirrorCS")])]});var subQ13=sQuery(id+"F13.wireOp",EDGE,"E341");var subQ14=makeQuery(id+"F20.opExtrude","SWEPT_FACE",FACE,{"disambiguationData":[OSD([subQ3])]});var subQ15=sQuery(id+"F12.wireOp",EDGE,"E320");var subQ16=makeQuery(id+"F19.opExtrude","SWEPT_FACE",FACE,{"disambiguationData":[OSD([subQ15])]});var subQ17=sQuery(id+"F8.wireOp",EDGE,"E121");var subQ18=sQuery(id+"F8.wireOp",EDGE,"E45.MirrorCS");var subQ19=sQuery(id+"F8.wireOp",EDGE,"E22.MirrorCS");var subQ20=makeQuery(id+"F16.opExtrude","CAP_FACE",FACE,{"disambiguationData":[OSD([subQ19,subQ18,sQuery(id+"F8.wireOp",EDGE,"E93"),subQ17])],"isStart":true});var subQ21=sQuery(id+"F12.wireOp",EDGE,"E323");var subQ22=sQuery(id+"F12.wireOp",EDGE,"E322");var subQ23=sQuery(id+"F12.wireOp",EDGE,"E321");var subQ24=sQuery(id+"F12.wireOp",EDGE,"E319");var subQ25=sQuery(id+"F12.wireOp",EDGE,"E318");var subQ26=makeQuery(id+"F19.opExtrude","CAP_FACE",FACE,{"disambiguationData":[OSD([subQ25,subQ24,subQ15,subQ23,subQ22,subQ21])],"isStart":false});var subQ27=sQuery(id+"F8.wireOp",EDGE,"E122");var subQ28=sQuery(id+"F8.wireOp",EDGE,"E44.MirrorCS");var subQ29=sQuery(id+"F8.wireOp",EDGE,"E21.MirrorCS");var subQ30=makeQuery(id+"F16.opExtrude","CAP_FACE",FACE,{"disambiguationData":[OSD([subQ29,subQ28,sQuery(id+"F8.wireOp",EDGE,"E96"),subQ27])],"isStart":true});var subQ31=makeQuery(id+"F18.opRevolve","SWEPT_FACE",FACE,{"disambiguationData":[OSD([sQuery(id+"F9.wireOp",EDGE,"E207")])]});var subQ32=sQuery(id+"F8.wireOp",EDGE,"E123");var subQ33=sQuery(id+"F8.wireOp",EDGE,"E50");var subQ34=sQuery(id+"F8.wireOp",EDGE,"E20.MirrorCS");var subQ35=makeQuery(id+"F16.opExtrude","CAP_FACE",FACE,{"disambiguationData":[OSD([subQ34,subQ33,sQuery(id+"F8.wireOp",EDGE,"E97"),subQ32])],"isStart":true});var subQ36=sQuery(id+"F9.wireOp",EDGE,"E214");var subQ37=sQuery(id+"F9.wireOp",EDGE,"E203");var subQ38=sQuery(id+"F9.wireOp",EDGE,"E202");var subQ39=makeQuery(id+"F17.opRevolve","CAP_FACE",FACE,{"disambiguationData":[OSD([subQ8,subQ38,subQ37,subQ36])],"isStart":false});var subQ40=sQuery(id+"F8.wireOp",EDGE,"E101");var subQ41=sQuery(id+"F8.wireOp",EDGE,"E42.MirrorCS");var subQ42=sQuery(id+"F8.wireOp",EDGE,"E19.MirrorCS");var subQ43=makeQuery(id+"F16.opExtrude","CAP_FACE",FACE,{"disambiguationData":[OSD([subQ42,subQ41,sQuery(id+"F8.wireOp",EDGE,"E53"),subQ40])],"isStart":true});var subQ44=sQuery(id+"F8.wireOp",EDGE,"E102");var subQ45=sQuery(id+"F8.wireOp",EDGE,"E41.MirrorCS");var subQ46=sQuery(id+"F8.wireOp",EDGE,"E18.MirrorCS");var subQ47=makeQuery(id+"F16.opExtrude","CAP_FACE",FACE,{"disambiguationData":[OSD([subQ46,subQ45,sQuery(id+"F8.wireOp",EDGE,"E55"),subQ44])],"isStart":true});var subQ48=sQuery(id+"F8.wireOp",EDGE,"E103");var subQ49=sQuery(id+"F8.wireOp",EDGE,"E40.MirrorCS");var subQ50=sQuery(id+"F8.wireOp",EDGE,"E17.MirrorCS");var subQ51=makeQuery(id+"F16.opExtrude","CAP_FACE",FACE,{"disambiguationData":[OSD([subQ50,subQ49,sQuery(id+"F8.wireOp",EDGE,"E57"),subQ48])],"isStart":true});var subQ52=sQuery(id+"F8.wireOp",EDGE,"E104");var subQ53=sQuery(id+"F8.wireOp",EDGE,"E39.MirrorCS");var subQ54=sQuery(id+"F8.wireOp",EDGE,"E16.MirrorCS");var subQ55=makeQuery(id+"F16.opExtrude","CAP_FACE",FACE,{"disambiguationData":[OSD([subQ54,subQ53,sQuery(id+"F8.wireOp",EDGE,"E59"),subQ52])],"isStart":true});var subQ56=sQuery(id+"F8.wireOp",EDGE,"E105");var subQ57=sQuery(id+"F8.wireOp",EDGE,"E27");var subQ58=sQuery(id+"F8.wireOp",EDGE,"E15.MirrorCS");var subQ59=makeQuery(id+"F16.opExtrude","CAP_FACE",FACE,{"disambiguationData":[OSD([subQ58,subQ57,sQuery(id+"F8.wireOp",EDGE,"E61"),subQ56])],"isStart":true});var subQ60=sQuery(id+"F8.wireOp",EDGE,"E117");var subQ61=sQuery(id+"F8.wireOp",EDGE,"E49");var subQ62=sQuery(id+"F8.wireOp",EDGE,"E14.MirrorCS");var subQ63=makeQuery(id+"F16.opExtrude","CAP_FACE",FACE,{"disambiguationData":[OSD([subQ62,subQ61,sQuery(id+"F8.wireOp",EDGE,"E85"),subQ60])],"isStart":true});var subQ64=sQuery(id+"F8.wireOp",EDGE,"E116");var subQ65=sQuery(id+"F8.wireOp",EDGE,"E38.MirrorCS");var subQ66=sQuery(id+"F8.wireOp",EDGE,"E13.MirrorCS");var subQ67=makeQuery(id+"F16.opExtrude","CAP_FACE",FACE,{"disambiguationData":[OSD([subQ66,subQ65,sQuery(id+"F8.wireOp",EDGE,"E83"),subQ64])],"isStart":true});var subQ68=sQuery(id+"F8.wireOp",EDGE,"E115");var subQ69=sQuery(id+"F8.wireOp",EDGE,"E37.MirrorCS");var subQ70=sQuery(id+"F8.wireOp",EDGE,"E12.MirrorCS");var subQ71=makeQuery(id+"F16.opExtrude","CAP_FACE",FACE,{"disambiguationData":[OSD([subQ70,subQ69,sQuery(id+"F8.wireOp",EDGE,"E81"),subQ68])],"isStart":true});var subQ72=sQuery(id+"F8.wireOp",EDGE,"E114");var subQ73=sQuery(id+"F8.wireOp",EDGE,"E36.MirrorCS");var subQ74=sQuery(id+"F8.wireOp",EDGE,"E11.MirrorCS");var subQ75=makeQuery(id+"F16.opExtrude","CAP_FACE",FACE,{"disambiguationData":[OSD([subQ74,subQ73,sQuery(id+"F8.wireOp",EDGE,"E79"),subQ72])],"isStart":true});var subQ76=sQuery(id+"F8.wireOp",EDGE,"E107");var subQ77=sQuery(id+"F8.wireOp",EDGE,"E29");var subQ78=sQuery(id+"F8.wireOp",EDGE,"E4");var subQ79=makeQuery(id+"F16.opExtrude","CAP_FACE",FACE,{"disambiguationData":[OSD([subQ78,subQ77,sQuery(id+"F8.wireOp",EDGE,"E65"),subQ76])],"isStart":true});var subQ80=makeQuery(id+"F17.opRevolve","CAP_FACE",FACE,{"disambiguationData":[OSD([subQ8,subQ38,subQ37,subQ36])],"isStart":true});var subQ81=sQuery(id+"F8.wireOp",EDGE,"E106");var subQ82=sQuery(id+"F8.wireOp",EDGE,"E28");var subQ83=sQuery(id+"F8.wireOp",EDGE,"E3");var subQ84=makeQuery(id+"F16.opExtrude","CAP_FACE",FACE,{"disambiguationData":[OSD([subQ83,subQ82,sQuery(id+"F8.wireOp",EDGE,"E63"),subQ81])],"isStart":true});var subQ85=sQuery(id+"F8.wireOp",EDGE,"E120");var subQ86=sQuery(id+"F8.wireOp",EDGE,"E119");var subQ87=sQuery(id+"F8.wireOp",EDGE,"E118");var subQ88=sQuery(id+"F8.wireOp",EDGE,"E113");var subQ89=sQuery(id+"F8.wireOp",EDGE,"E112");var subQ90=sQuery(id+"F8.wireOp",EDGE,"E111");var subQ91=sQuery(id+"F8.wireOp",EDGE,"E110");var subQ92=sQuery(id+"F8.wireOp",EDGE,"E109");var subQ93=sQuery(id+"F8.wireOp",EDGE,"E108");var subQ94=sQuery(id+"F8.wireOp",EDGE,"E100");var subQ95=sQuery(id+"F8.wireOp",EDGE,"E98");var subQ96=sQuery(id+"F8.wireOp",EDGE,"E95");var subQ97=sQuery(id+"F8.wireOp",EDGE,"E94");var subQ98=sQuery(id+"F8.wireOp",EDGE,"E92");var subQ99=sQuery(id+"F8.wireOp",EDGE,"E90");var subQ100=sQuery(id+"F8.wireOp",EDGE,"E88");var subQ101=sQuery(id+"F8.wireOp",EDGE,"E86");var subQ102=sQuery(id+"F8.wireOp",EDGE,"E84");var subQ103=sQuery(id+"F8.wireOp",EDGE,"E82");var subQ104=sQuery(id+"F8.wireOp",EDGE,"E80");var subQ105=sQuery(id+"F8.wireOp",EDGE,"E78");var subQ106=sQuery(id+"F8.wireOp",EDGE,"E76");var subQ107=sQuery(id+"F8.wireOp",EDGE,"E74");var subQ108=sQuery(id+"F8.wireOp",EDGE,"E72");var subQ109=sQuery(id+"F8.wireOp",EDGE,"E70");var subQ110=sQuery(id+"F8.wireOp",EDGE,"E68");var subQ111=sQuery(id+"F8.wireOp",EDGE,"E66");var subQ112=sQuery(id+"F8.wireOp",EDGE,"E64");var subQ113=sQuery(id+"F8.wireOp",EDGE,"E62");var subQ114=sQuery(id+"F8.wireOp",EDGE,"E60");var subQ115=sQuery(id+"F8.wireOp",EDGE,"E58");var subQ116=sQuery(id+"F8.wireOp",EDGE,"E56");var subQ117=sQuery(id+"F8.wireOp",EDGE,"E54");var subQ118=sQuery(id+"F8.wireOp",EDGE,"E52");var subQ119=sQuery(id+"F8.wireOp",EDGE,"E48.MirrorCS");var subQ120=sQuery(id+"F8.wireOp",EDGE,"E47.MirrorCS");var subQ121=sQuery(id+"F8.wireOp",EDGE,"E46.MirrorCS");var subQ122=sQuery(id+"F8.wireOp",EDGE,"E43.MirrorCS");var subQ123=sQuery(id+"F8.wireOp",EDGE,"E35.MirrorCS");var subQ124=sQuery(id+"F8.wireOp",EDGE,"E34.MirrorCS");var subQ125=sQuery(id+"F8.wireOp",EDGE,"E33");var subQ126=sQuery(id+"F8.wireOp",EDGE,"E32");var subQ127=sQuery(id+"F8.wireOp",EDGE,"E31");var subQ128=sQuery(id+"F8.wireOp",EDGE,"E30");var subQ129=sQuery(id+"F8.wireOp",EDGE,"E26");var subQ130=sQuery(id+"F8.wireOp",EDGE,"E25");var subQ131=sQuery(id+"F8.wireOp",EDGE,"E24.MirrorCS");var subQ132=sQuery(id+"F8.wireOp",EDGE,"E23.MirrorCS");var subQ133=sQuery(id+"F8.wireOp",EDGE,"E10.MirrorCS");var subQ134=sQuery(id+"F8.wireOp",EDGE,"E9");var subQ135=sQuery(id+"F8.wireOp",EDGE,"E8");var subQ136=sQuery(id+"F8.wireOp",EDGE,"E7");var subQ137=sQuery(id+"F8.wireOp",EDGE,"E6");var subQ138=sQuery(id+"F8.wireOp",EDGE,"E5");var subQ139=sQuery(id+"F8.wireOp",EDGE,"E1.0");var subQ140=makeQuery(id+"F15.opExtrude","CAP_FACE",FACE,{"disambiguationData":[OSD([subQ139,subQ83,subQ78,subQ138,subQ137,subQ136,subQ135,subQ134,subQ133,subQ74,subQ70,subQ66,subQ62,subQ58,subQ54,subQ50,subQ46,subQ42,subQ34,subQ29,subQ19,subQ132,subQ131,subQ130,subQ129,subQ57,subQ82,subQ77,subQ128,subQ127,subQ126,subQ125,subQ124,subQ123,subQ73,subQ69,subQ65,subQ53,subQ49,subQ45,subQ41,subQ122,subQ28,subQ18,subQ121,subQ120,subQ119,subQ61,subQ33,subQ118,subQ117,subQ116,subQ115,subQ114,subQ113,subQ112,subQ111,subQ110,subQ109,subQ108,subQ107,subQ106,subQ105,subQ104,subQ103,subQ102,subQ101,subQ100,subQ99,subQ98,subQ97,subQ96,subQ95,subQ94,subQ40,subQ44,subQ48,subQ52,subQ56,subQ81,subQ76,subQ93,subQ92,subQ91,subQ90,subQ89,subQ88,subQ72,subQ68,subQ64,subQ60,subQ87,subQ86,subQ85,subQ17,subQ27,subQ32])],"isStart":true});var subQ141=makeQuery(id+"F16.opExtrude","CAP_FACE",FACE,{"disambiguationData":[OSD([subQ129,subQ122,sQuery(id+"F8.wireOp",EDGE,"E99"),subQ94])],"isStart":true});var subQ142=makeQuery(id+"F16.opExtrude","CAP_FACE",FACE,{"disambiguationData":[OSD([subQ134,subQ124,sQuery(id+"F8.wireOp",EDGE,"E75"),subQ89])],"isStart":true});var subQ143=makeQuery(id+"F16.opExtrude","CAP_FACE",FACE,{"disambiguationData":[OSD([subQ138,subQ128,sQuery(id+"F8.wireOp",EDGE,"E67"),subQ93])],"isStart":true});var subQ144=makeQuery(id+"F16.opExtrude","CAP_FACE",FACE,{"disambiguationData":[OSD([subQ137,subQ127,sQuery(id+"F8.wireOp",EDGE,"E69"),subQ92])],"isStart":true});var subQ145=makeQuery(id+"F19.opExtrude","CAP_FACE",FACE,{"disambiguationData":[OSD([subQ25,subQ24,subQ15,subQ23,subQ22,subQ21])],"isStart":true});var subQ146=makeQuery(id+"F16.opExtrude","CAP_FACE",FACE,{"disambiguationData":[OSD([subQ136,subQ126,sQuery(id+"F8.wireOp",EDGE,"E71"),subQ91])],"isStart":true});var subQ147=makeQuery(id+"F15.opExtrude","CAP_FACE",FACE,{"disambiguationData":[OSD([subQ139,subQ83,subQ78,subQ138,subQ137,subQ136,subQ135,subQ134,subQ133,subQ74,subQ70,subQ66,subQ62,subQ58,subQ54,subQ50,subQ46,subQ42,subQ34,subQ29,subQ19,subQ132,subQ131,subQ130,subQ129,subQ57,subQ82,subQ77,subQ128,subQ127,subQ126,subQ125,subQ124,subQ123,subQ73,subQ69,subQ65,subQ53,subQ49,subQ45,subQ41,subQ122,subQ28,subQ18,subQ121,subQ120,subQ119,subQ61,subQ33,subQ118,subQ117,subQ116,subQ115,subQ114,subQ113,subQ112,subQ111,subQ110,subQ109,subQ108,subQ107,subQ106,subQ105,subQ104,subQ103,subQ102,subQ101,subQ100,subQ99,subQ98,subQ97,subQ96,subQ95,subQ94,subQ40,subQ44,subQ48,subQ52,subQ56,subQ81,subQ76,subQ93,subQ92,subQ91,subQ90,subQ89,subQ88,subQ72,subQ68,subQ64,subQ60,subQ87,subQ86,subQ85,subQ17,subQ27,subQ32])],"isStart":false});var subQ148=makeQuery(id+"F16.opExtrude","CAP_FACE",FACE,{"disambiguationData":[OSD([subQ135,subQ125,sQuery(id+"F8.wireOp",EDGE,"E73"),subQ90])],"isStart":true});var subQ149=makeQuery(id+"F19.opExtrude","SWEPT_FACE",FACE,{"disambiguationData":[OSD([subQ21])]});var subQ150=makeQuery(id+"F16.opExtrude","CAP_FACE",FACE,{"disambiguationData":[OSD([subQ133,subQ123,sQuery(id+"F8.wireOp",EDGE,"E77"),subQ88])],"isStart":true});var subQ151=makeQuery(id+"F16.opExtrude","CAP_FACE",FACE,{"disambiguationData":[OSD([subQ132,subQ121,sQuery(id+"F8.wireOp",EDGE,"E91"),subQ85])],"isStart":true});var subQ152=makeQuery(id+"F16.opExtrude","CAP_FACE",FACE,{"disambiguationData":[OSD([subQ131,subQ120,sQuery(id+"F8.wireOp",EDGE,"E89"),subQ86])],"isStart":true});var subQ153=makeQuery(id+"F16.opExtrude","CAP_FACE",FACE,{"disambiguationData":[OSD([subQ130,subQ119,sQuery(id+"F8.wireOp",EDGE,"E87"),subQ87])],"isStart":true});var subQ154=makeQuery(id+"F18.opRevolve","SWEPT_FACE",FACE,{"disambiguationData":[OSD([subQ36])]});var subQ155=makeQuery(id+"F19.opExtrude","SWEPT_FACE",FACE,{"disambiguationData":[OSD([subQ24])]});var subQ156=makeQuery(id+"F19.opExtrude","SWEPT_FACE",FACE,{"disambiguationData":[OSD([subQ22])]});Q7=makeQuery(id+"F36.opFillet","BLEND_EDGE",EDGE,{"blendedFrom":[makeQuery(id+"F21.boolean.opBoolean","INTERSECT",EDGE,{"derivedFrom":[makeQuery(id+"F20.boolean.opBoolean","SPLIT",FACE,{"disambiguationData":[TD([subQ31])],"derivedFrom":makeQuery(id+"F19.boolean.opBoolean","SPLIT",FACE,{"disambiguationData":[TD([makeQuery(id+"F15.opExtrude","SWEPT_FACE",FACE,{"disambiguationData":[OSD([subQ139])]}),subQ140,subQ147,subQ84,subQ79,subQ143,subQ144,subQ146,subQ148,subQ142,subQ150,subQ75,subQ71,subQ67,subQ63,subQ59,subQ55,subQ51,subQ47,subQ43,subQ35,subQ30,subQ20,subQ151,subQ152,subQ153,subQ141,subQ80,subQ39,subQ31,subQ154,subQ145,subQ26,subQ155,subQ16,subQ156,subQ149])],"derivedFrom":makeQuery(id+"F18.boolean.opBoolean","MERGE",FACE,{"derivedFrom":[subQ10,subQ9]})})}),subQ12]}),makeQuery(id+"F24.boolean.opBoolean","SPLIT",FACE,{"disambiguationData":[TD([subQ11])],"derivedFrom":makeQuery(id+"F23.boolean.opBoolean","MERGE",FACE,{"derivedFrom":[subQ16,subQ14,makeQuery(id+"F23.opExtrude","CAP_FACE",FACE,{"disambiguationData":[OSD([sQuery(id+"F13.wireOp",EDGE,"E329.MirrorCS"),sQuery(id+"F13.wireOp",EDGE,"E339"),sQuery(id+"F13.wireOp",EDGE,"E340"),subQ13,sQuery(id+"F13.wireOp",EDGE,"E342.0"),sQuery(id+"F13.wireOp",EDGE,"E342.1"),sQuery(id+"F13.wireOp",EDGE,"E342.2")])],"isStart":false})]})})],"blendedInto":[makeQuery(id+"F24.boolean.opBoolean","SPLIT",FACE,{"disambiguationData":[TD([subQ11])],"derivedFrom":makeQuery(id+"F23.boolean.opBoolean","MERGE",FACE,{"derivedFrom":[subQ16,subQ14,makeQuery(id+"F23.opExtrude","CAP_FACE",FACE,{"disambiguationData":[OSD([sQuery(id+"F13.wireOp",EDGE,"E329.MirrorCS"),sQuery(id+"F13.wireOp",EDGE,"E339"),sQuery(id+"F13.wireOp",EDGE,"E340"),subQ13,sQuery(id+"F13.wireOp",EDGE,"E342.0"),sQuery(id+"F13.wireOp",EDGE,"E342.1"),sQuery(id+"F13.wireOp",EDGE,"E342.2")])],"isStart":false})]})})]});}
            var Q8;
            {var subQ0=sQuery(id+"F12.wireOp",EDGE,"E323");var subQ1=sQuery(id+"F12.wireOp",EDGE,"E322");var subQ2=sQuery(id+"F12.wireOp",EDGE,"E321");var subQ3=sQuery(id+"F12.wireOp",EDGE,"E320");var subQ4=sQuery(id+"F12.wireOp",EDGE,"E319");var subQ5=sQuery(id+"F12.wireOp",EDGE,"E318");var subQ6=makeQuery(id+"F19.opExtrude","CAP_FACE",FACE,{"disambiguationData":[OSD([subQ5,subQ4,subQ3,subQ2,subQ1,subQ0])],"isStart":false});var subQ7=sQuery(id+"F9.wireOp",EDGE,"E201");var subQ8=makeQuery(id+"F18.opRevolve","SWEPT_FACE",FACE,{"disambiguationData":[OSD([subQ7])]});var subQ9=makeQuery(id+"F19.opExtrude","SWEPT_FACE",FACE,{"disambiguationData":[OSD([subQ4])]});var subQ10=sQuery(id+"F13.wireOp",EDGE,"E339");var subQ11=makeQuery(id+"F19.opExtrude","CAP_FACE",FACE,{"disambiguationData":[OSD([subQ5,subQ4,subQ3,subQ2,subQ1,subQ0])],"isStart":true});var subQ12=makeQuery(id+"F17.opRevolve","SWEPT_FACE",FACE,{"disambiguationData":[OSD([subQ7])]});var subQ13=makeQuery(id+"F21.opExtrude","SWEPT_FACE",FACE,{"disambiguationData":[OSD([sQuery(id+"F13.wireOp",EDGE,"E327.MirrorCS")])]});var subQ14=sQuery(id+"F11.wireOp",EDGE,"E298");var subQ15=makeQuery(id+"F20.opExtrude","SWEPT_FACE",FACE,{"disambiguationData":[OSD([subQ14])]});var subQ16=makeQuery(id+"F19.opExtrude","SWEPT_FACE",FACE,{"disambiguationData":[OSD([subQ3])]});var subQ17=sQuery(id+"F8.wireOp",EDGE,"E121");var subQ18=sQuery(id+"F8.wireOp",EDGE,"E45.MirrorCS");var subQ19=sQuery(id+"F8.wireOp",EDGE,"E22.MirrorCS");var subQ20=makeQuery(id+"F16.opExtrude","CAP_FACE",FACE,{"disambiguationData":[OSD([subQ19,subQ18,sQuery(id+"F8.wireOp",EDGE,"E93"),subQ17])],"isStart":true});var subQ21=sQuery(id+"F8.wireOp",EDGE,"E122");var subQ22=sQuery(id+"F8.wireOp",EDGE,"E44.MirrorCS");var subQ23=sQuery(id+"F8.wireOp",EDGE,"E21.MirrorCS");var subQ24=makeQuery(id+"F16.opExtrude","CAP_FACE",FACE,{"disambiguationData":[OSD([subQ23,subQ22,sQuery(id+"F8.wireOp",EDGE,"E96"),subQ21])],"isStart":true});var subQ25=makeQuery(id+"F18.opRevolve","SWEPT_FACE",FACE,{"disambiguationData":[OSD([sQuery(id+"F9.wireOp",EDGE,"E207")])]});var subQ26=sQuery(id+"F8.wireOp",EDGE,"E123");var subQ27=sQuery(id+"F8.wireOp",EDGE,"E50");var subQ28=sQuery(id+"F8.wireOp",EDGE,"E20.MirrorCS");var subQ29=makeQuery(id+"F16.opExtrude","CAP_FACE",FACE,{"disambiguationData":[OSD([subQ28,subQ27,sQuery(id+"F8.wireOp",EDGE,"E97"),subQ26])],"isStart":true});var subQ30=sQuery(id+"F9.wireOp",EDGE,"E214");var subQ31=sQuery(id+"F9.wireOp",EDGE,"E203");var subQ32=sQuery(id+"F9.wireOp",EDGE,"E202");var subQ33=makeQuery(id+"F17.opRevolve","CAP_FACE",FACE,{"disambiguationData":[OSD([subQ7,subQ32,subQ31,subQ30])],"isStart":false});var subQ34=sQuery(id+"F8.wireOp",EDGE,"E101");var subQ35=sQuery(id+"F8.wireOp",EDGE,"E42.MirrorCS");var subQ36=sQuery(id+"F8.wireOp",EDGE,"E19.MirrorCS");var subQ37=makeQuery(id+"F16.opExtrude","CAP_FACE",FACE,{"disambiguationData":[OSD([subQ36,subQ35,sQuery(id+"F8.wireOp",EDGE,"E53"),subQ34])],"isStart":true});var subQ38=sQuery(id+"F8.wireOp",EDGE,"E102");var subQ39=sQuery(id+"F8.wireOp",EDGE,"E41.MirrorCS");var subQ40=sQuery(id+"F8.wireOp",EDGE,"E18.MirrorCS");var subQ41=makeQuery(id+"F16.opExtrude","CAP_FACE",FACE,{"disambiguationData":[OSD([subQ40,subQ39,sQuery(id+"F8.wireOp",EDGE,"E55"),subQ38])],"isStart":true});var subQ42=sQuery(id+"F8.wireOp",EDGE,"E103");var subQ43=sQuery(id+"F8.wireOp",EDGE,"E40.MirrorCS");var subQ44=sQuery(id+"F8.wireOp",EDGE,"E17.MirrorCS");var subQ45=makeQuery(id+"F16.opExtrude","CAP_FACE",FACE,{"disambiguationData":[OSD([subQ44,subQ43,sQuery(id+"F8.wireOp",EDGE,"E57"),subQ42])],"isStart":true});var subQ46=sQuery(id+"F8.wireOp",EDGE,"E104");var subQ47=sQuery(id+"F8.wireOp",EDGE,"E39.MirrorCS");var subQ48=sQuery(id+"F8.wireOp",EDGE,"E16.MirrorCS");var subQ49=makeQuery(id+"F16.opExtrude","CAP_FACE",FACE,{"disambiguationData":[OSD([subQ48,subQ47,sQuery(id+"F8.wireOp",EDGE,"E59"),subQ46])],"isStart":true});var subQ50=sQuery(id+"F8.wireOp",EDGE,"E105");var subQ51=sQuery(id+"F8.wireOp",EDGE,"E27");var subQ52=sQuery(id+"F8.wireOp",EDGE,"E15.MirrorCS");var subQ53=makeQuery(id+"F16.opExtrude","CAP_FACE",FACE,{"disambiguationData":[OSD([subQ52,subQ51,sQuery(id+"F8.wireOp",EDGE,"E61"),subQ50])],"isStart":true});var subQ54=sQuery(id+"F8.wireOp",EDGE,"E117");var subQ55=sQuery(id+"F8.wireOp",EDGE,"E49");var subQ56=sQuery(id+"F8.wireOp",EDGE,"E14.MirrorCS");var subQ57=makeQuery(id+"F16.opExtrude","CAP_FACE",FACE,{"disambiguationData":[OSD([subQ56,subQ55,sQuery(id+"F8.wireOp",EDGE,"E85"),subQ54])],"isStart":true});var subQ58=sQuery(id+"F8.wireOp",EDGE,"E116");var subQ59=sQuery(id+"F8.wireOp",EDGE,"E38.MirrorCS");var subQ60=sQuery(id+"F8.wireOp",EDGE,"E13.MirrorCS");var subQ61=makeQuery(id+"F16.opExtrude","CAP_FACE",FACE,{"disambiguationData":[OSD([subQ60,subQ59,sQuery(id+"F8.wireOp",EDGE,"E83"),subQ58])],"isStart":true});var subQ62=sQuery(id+"F8.wireOp",EDGE,"E115");var subQ63=sQuery(id+"F8.wireOp",EDGE,"E37.MirrorCS");var subQ64=sQuery(id+"F8.wireOp",EDGE,"E12.MirrorCS");var subQ65=makeQuery(id+"F16.opExtrude","CAP_FACE",FACE,{"disambiguationData":[OSD([subQ64,subQ63,sQuery(id+"F8.wireOp",EDGE,"E81"),subQ62])],"isStart":true});var subQ66=sQuery(id+"F8.wireOp",EDGE,"E114");var subQ67=sQuery(id+"F8.wireOp",EDGE,"E36.MirrorCS");var subQ68=sQuery(id+"F8.wireOp",EDGE,"E11.MirrorCS");var subQ69=makeQuery(id+"F16.opExtrude","CAP_FACE",FACE,{"disambiguationData":[OSD([subQ68,subQ67,sQuery(id+"F8.wireOp",EDGE,"E79"),subQ66])],"isStart":true});var subQ70=sQuery(id+"F8.wireOp",EDGE,"E107");var subQ71=sQuery(id+"F8.wireOp",EDGE,"E29");var subQ72=sQuery(id+"F8.wireOp",EDGE,"E4");var subQ73=makeQuery(id+"F16.opExtrude","CAP_FACE",FACE,{"disambiguationData":[OSD([subQ72,subQ71,sQuery(id+"F8.wireOp",EDGE,"E65"),subQ70])],"isStart":true});var subQ74=makeQuery(id+"F17.opRevolve","CAP_FACE",FACE,{"disambiguationData":[OSD([subQ7,subQ32,subQ31,subQ30])],"isStart":true});var subQ75=sQuery(id+"F8.wireOp",EDGE,"E106");var subQ76=sQuery(id+"F8.wireOp",EDGE,"E28");var subQ77=sQuery(id+"F8.wireOp",EDGE,"E3");var subQ78=makeQuery(id+"F16.opExtrude","CAP_FACE",FACE,{"disambiguationData":[OSD([subQ77,subQ76,sQuery(id+"F8.wireOp",EDGE,"E63"),subQ75])],"isStart":true});var subQ79=sQuery(id+"F8.wireOp",EDGE,"E120");var subQ80=sQuery(id+"F8.wireOp",EDGE,"E119");var subQ81=sQuery(id+"F8.wireOp",EDGE,"E118");var subQ82=sQuery(id+"F8.wireOp",EDGE,"E113");var subQ83=sQuery(id+"F8.wireOp",EDGE,"E112");var subQ84=sQuery(id+"F8.wireOp",EDGE,"E111");var subQ85=sQuery(id+"F8.wireOp",EDGE,"E110");var subQ86=sQuery(id+"F8.wireOp",EDGE,"E109");var subQ87=sQuery(id+"F8.wireOp",EDGE,"E108");var subQ88=sQuery(id+"F8.wireOp",EDGE,"E100");var subQ89=sQuery(id+"F8.wireOp",EDGE,"E98");var subQ90=sQuery(id+"F8.wireOp",EDGE,"E95");var subQ91=sQuery(id+"F8.wireOp",EDGE,"E94");var subQ92=sQuery(id+"F8.wireOp",EDGE,"E92");var subQ93=sQuery(id+"F8.wireOp",EDGE,"E90");var subQ94=sQuery(id+"F8.wireOp",EDGE,"E88");var subQ95=sQuery(id+"F8.wireOp",EDGE,"E86");var subQ96=sQuery(id+"F8.wireOp",EDGE,"E84");var subQ97=sQuery(id+"F8.wireOp",EDGE,"E82");var subQ98=sQuery(id+"F8.wireOp",EDGE,"E80");var subQ99=sQuery(id+"F8.wireOp",EDGE,"E78");var subQ100=sQuery(id+"F8.wireOp",EDGE,"E76");var subQ101=sQuery(id+"F8.wireOp",EDGE,"E74");var subQ102=sQuery(id+"F8.wireOp",EDGE,"E72");var subQ103=sQuery(id+"F8.wireOp",EDGE,"E70");var subQ104=sQuery(id+"F8.wireOp",EDGE,"E68");var subQ105=sQuery(id+"F8.wireOp",EDGE,"E66");var subQ106=sQuery(id+"F8.wireOp",EDGE,"E64");var subQ107=sQuery(id+"F8.wireOp",EDGE,"E62");var subQ108=sQuery(id+"F8.wireOp",EDGE,"E60");var subQ109=sQuery(id+"F8.wireOp",EDGE,"E58");var subQ110=sQuery(id+"F8.wireOp",EDGE,"E56");var subQ111=sQuery(id+"F8.wireOp",EDGE,"E54");var subQ112=sQuery(id+"F8.wireOp",EDGE,"E52");var subQ113=sQuery(id+"F8.wireOp",EDGE,"E48.MirrorCS");var subQ114=sQuery(id+"F8.wireOp",EDGE,"E47.MirrorCS");var subQ115=sQuery(id+"F8.wireOp",EDGE,"E46.MirrorCS");var subQ116=sQuery(id+"F8.wireOp",EDGE,"E43.MirrorCS");var subQ117=sQuery(id+"F8.wireOp",EDGE,"E35.MirrorCS");var subQ118=sQuery(id+"F8.wireOp",EDGE,"E34.MirrorCS");var subQ119=sQuery(id+"F8.wireOp",EDGE,"E33");var subQ120=sQuery(id+"F8.wireOp",EDGE,"E32");var subQ121=sQuery(id+"F8.wireOp",EDGE,"E31");var subQ122=sQuery(id+"F8.wireOp",EDGE,"E30");var subQ123=sQuery(id+"F8.wireOp",EDGE,"E26");var subQ124=sQuery(id+"F8.wireOp",EDGE,"E25");var subQ125=sQuery(id+"F8.wireOp",EDGE,"E24.MirrorCS");var subQ126=sQuery(id+"F8.wireOp",EDGE,"E23.MirrorCS");var subQ127=sQuery(id+"F8.wireOp",EDGE,"E10.MirrorCS");var subQ128=sQuery(id+"F8.wireOp",EDGE,"E9");var subQ129=sQuery(id+"F8.wireOp",EDGE,"E8");var subQ130=sQuery(id+"F8.wireOp",EDGE,"E7");var subQ131=sQuery(id+"F8.wireOp",EDGE,"E6");var subQ132=sQuery(id+"F8.wireOp",EDGE,"E5");var subQ133=sQuery(id+"F8.wireOp",EDGE,"E1.0");var subQ134=makeQuery(id+"F15.opExtrude","CAP_FACE",FACE,{"disambiguationData":[OSD([subQ133,subQ77,subQ72,subQ132,subQ131,subQ130,subQ129,subQ128,subQ127,subQ68,subQ64,subQ60,subQ56,subQ52,subQ48,subQ44,subQ40,subQ36,subQ28,subQ23,subQ19,subQ126,subQ125,subQ124,subQ123,subQ51,subQ76,subQ71,subQ122,subQ121,subQ120,subQ119,subQ118,subQ117,subQ67,subQ63,subQ59,subQ47,subQ43,subQ39,subQ35,subQ116,subQ22,subQ18,subQ115,subQ114,subQ113,subQ55,subQ27,subQ112,subQ111,subQ110,subQ109,subQ108,subQ107,subQ106,subQ105,subQ104,subQ103,subQ102,subQ101,subQ100,subQ99,subQ98,subQ97,subQ96,subQ95,subQ94,subQ93,subQ92,subQ91,subQ90,subQ89,subQ88,subQ34,subQ38,subQ42,subQ46,subQ50,subQ75,subQ70,subQ87,subQ86,subQ85,subQ84,subQ83,subQ82,subQ66,subQ62,subQ58,subQ54,subQ81,subQ80,subQ79,subQ17,subQ21,subQ26])],"isStart":true});var subQ135=makeQuery(id+"F16.opExtrude","CAP_FACE",FACE,{"disambiguationData":[OSD([subQ123,subQ116,sQuery(id+"F8.wireOp",EDGE,"E99"),subQ88])],"isStart":true});var subQ136=makeQuery(id+"F16.opExtrude","CAP_FACE",FACE,{"disambiguationData":[OSD([subQ128,subQ118,sQuery(id+"F8.wireOp",EDGE,"E75"),subQ83])],"isStart":true});var subQ138=makeQuery(id+"F16.opExtrude","CAP_FACE",FACE,{"disambiguationData":[OSD([subQ132,subQ122,sQuery(id+"F8.wireOp",EDGE,"E67"),subQ87])],"isStart":true});var subQ139=makeQuery(id+"F16.opExtrude","CAP_FACE",FACE,{"disambiguationData":[OSD([subQ131,subQ121,sQuery(id+"F8.wireOp",EDGE,"E69"),subQ86])],"isStart":true});var subQ140=makeQuery(id+"F16.opExtrude","CAP_FACE",FACE,{"disambiguationData":[OSD([subQ130,subQ120,sQuery(id+"F8.wireOp",EDGE,"E71"),subQ85])],"isStart":true});var subQ145=makeQuery(id+"F15.opExtrude","CAP_FACE",FACE,{"disambiguationData":[OSD([subQ133,subQ77,subQ72,subQ132,subQ131,subQ130,subQ129,subQ128,subQ127,subQ68,subQ64,subQ60,subQ56,subQ52,subQ48,subQ44,subQ40,subQ36,subQ28,subQ23,subQ19,subQ126,subQ125,subQ124,subQ123,subQ51,subQ76,subQ71,subQ122,subQ121,subQ120,subQ119,subQ118,subQ117,subQ67,subQ63,subQ59,subQ47,subQ43,subQ39,subQ35,subQ116,subQ22,subQ18,subQ115,subQ114,subQ113,subQ55,subQ27,subQ112,subQ111,subQ110,subQ109,subQ108,subQ107,subQ106,subQ105,subQ104,subQ103,subQ102,subQ101,subQ100,subQ99,subQ98,subQ97,subQ96,subQ95,subQ94,subQ93,subQ92,subQ91,subQ90,subQ89,subQ88,subQ34,subQ38,subQ42,subQ46,subQ50,subQ75,subQ70,subQ87,subQ86,subQ85,subQ84,subQ83,subQ82,subQ66,subQ62,subQ58,subQ54,subQ81,subQ80,subQ79,subQ17,subQ21,subQ26])],"isStart":false});var subQ146=makeQuery(id+"F16.opExtrude","CAP_FACE",FACE,{"disambiguationData":[OSD([subQ129,subQ119,sQuery(id+"F8.wireOp",EDGE,"E73"),subQ84])],"isStart":true});var subQ147=makeQuery(id+"F19.opExtrude","SWEPT_FACE",FACE,{"disambiguationData":[OSD([subQ0])]});var subQ148=makeQuery(id+"F16.opExtrude","CAP_FACE",FACE,{"disambiguationData":[OSD([subQ127,subQ117,sQuery(id+"F8.wireOp",EDGE,"E77"),subQ82])],"isStart":true});var subQ149=makeQuery(id+"F16.opExtrude","CAP_FACE",FACE,{"disambiguationData":[OSD([subQ126,subQ115,sQuery(id+"F8.wireOp",EDGE,"E91"),subQ79])],"isStart":true});var subQ150=makeQuery(id+"F16.opExtrude","CAP_FACE",FACE,{"disambiguationData":[OSD([subQ125,subQ114,sQuery(id+"F8.wireOp",EDGE,"E89"),subQ80])],"isStart":true});var subQ151=makeQuery(id+"F16.opExtrude","CAP_FACE",FACE,{"disambiguationData":[OSD([subQ124,subQ113,sQuery(id+"F8.wireOp",EDGE,"E87"),subQ81])],"isStart":true});var subQ152=makeQuery(id+"F18.opRevolve","SWEPT_FACE",FACE,{"disambiguationData":[OSD([subQ30])]});var subQ153=makeQuery(id+"F19.opExtrude","SWEPT_FACE",FACE,{"disambiguationData":[OSD([subQ1])]});Q8=makeQuery(id+"F36.opFillet","BLEND_EDGE",EDGE,{"blendedFrom":[makeQuery(id+"F21.boolean.opBoolean","INTERSECT",EDGE,{"derivedFrom":[makeQuery(id+"F20.boolean.opBoolean","SPLIT",FACE,{"disambiguationData":[TD([subQ25])],"derivedFrom":makeQuery(id+"F19.boolean.opBoolean","SPLIT",FACE,{"disambiguationData":[TD([makeQuery(id+"F15.opExtrude","SWEPT_FACE",FACE,{"disambiguationData":[OSD([subQ133])]}),subQ134,subQ145,subQ78,subQ73,subQ138,subQ139,subQ140,subQ146,subQ136,subQ148,subQ69,subQ65,subQ61,subQ57,subQ53,subQ49,subQ45,subQ41,subQ37,subQ29,subQ24,subQ20,subQ149,subQ150,subQ151,subQ135,subQ74,subQ33,subQ25,subQ152,subQ11,subQ6,subQ9,subQ16,subQ153,subQ147])],"derivedFrom":makeQuery(id+"F18.boolean.opBoolean","MERGE",FACE,{"derivedFrom":[subQ12,subQ8]})})}),subQ13]}),makeQuery(id+"F24.boolean.opBoolean","SPLIT",FACE,{"disambiguationData":[TD([subQ9])],"derivedFrom":makeQuery(id+"F23.boolean.opBoolean","MERGE",FACE,{"derivedFrom":[subQ16,subQ15,makeQuery(id+"F23.opExtrude","CAP_FACE",FACE,{"disambiguationData":[OSD([sQuery(id+"F13.wireOp",EDGE,"E329.MirrorCS"),subQ10,sQuery(id+"F13.wireOp",EDGE,"E340"),sQuery(id+"F13.wireOp",EDGE,"E341"),sQuery(id+"F13.wireOp",EDGE,"E342.0"),sQuery(id+"F13.wireOp",EDGE,"E342.1"),sQuery(id+"F13.wireOp",EDGE,"E342.2")])],"isStart":false})]})})],"blendedInto":[makeQuery(id+"F24.boolean.opBoolean","SPLIT",FACE,{"disambiguationData":[TD([subQ9])],"derivedFrom":makeQuery(id+"F23.boolean.opBoolean","MERGE",FACE,{"derivedFrom":[subQ16,subQ15,makeQuery(id+"F23.opExtrude","CAP_FACE",FACE,{"disambiguationData":[OSD([sQuery(id+"F13.wireOp",EDGE,"E329.MirrorCS"),subQ10,sQuery(id+"F13.wireOp",EDGE,"E340"),sQuery(id+"F13.wireOp",EDGE,"E341"),sQuery(id+"F13.wireOp",EDGE,"E342.0"),sQuery(id+"F13.wireOp",EDGE,"E342.1"),sQuery(id+"F13.wireOp",EDGE,"E342.2")])],"isStart":false})]})})]});}
            var Q9;
            Q9=makeQuery(id+"F25.opExtrude","CAP_EDGE",EDGE,{"disambiguationData":[OSD([sQuery(id+"F10.wireOp",EDGE,"E269")])],"isStart":true});
            var Q10;
            Q10=makeQuery(id+"F25.opExtrude","CAP_EDGE",EDGE,{"disambiguationData":[OSD([sQuery(id+"F10.wireOp",EDGE,"E270")])],"isStart":true});
            var Q11;
            Q11=makeQuery(id+"F25.opExtrude","CAP_EDGE",EDGE,{"disambiguationData":[OSD([sQuery(id+"F10.wireOp",EDGE,"oL6OTD61-6akg-XuXO-bSg7-LTXE6IEmyDXN")])],"isStart":true});
            var Q12;
            Q12=makeQuery(id+"F35.opExtrude","SWEPT_EDGE",EDGE,{"disambiguationData":[OSD([sQuery(id+"F29.wireOp",EDGE,"E402.0"),sQuery(id+"F29.wireOp",EDGE,"E404")])]});
            var Q13;
            Q13=makeQuery(id+"F35.opExtrude","SWEPT_EDGE",EDGE,{"disambiguationData":[OSD([sQuery(id+"F29.wireOp",EDGE,"E402.0"),sQuery(id+"F29.wireOp",EDGE,"E403")])]});
            var Q14;
            Q14=makeQuery(id+"F35.opExtrude","SWEPT_EDGE",EDGE,{"disambiguationData":[OSD([sQuery(id+"F29.wireOp",EDGE,"E400"),sQuery(id+"F29.wireOp",EDGE,"E404")])]});
            var Q15;
            Q15=makeQuery(id+"F35.opExtrude","SWEPT_EDGE",EDGE,{"disambiguationData":[OSD([sQuery(id+"F29.wireOp",EDGE,"E400"),sQuery(id+"F29.wireOp",EDGE,"E403")])]});
            fillet(context, id + "F37", {"entities" : qUnion([Q0, Q1, Q2, Q3, Q4, Q5, Q6, Q7, Q8, Q9, Q10, Q11, Q12, Q13, Q14, Q15]), "radius" : 2.6 * mm, "tangentPropagation" : true, "allowEdgeOverflow" : false});
        }
        {
            var Q0;
            {var subQ0=sQuery(id+"F8.wireOp",EDGE,"E124");Q0=makeQuery(id+"F16.opExtrude","CAP_EDGE",EDGE,{"disambiguationData":[OSD([subQ0]),TDD([makeQuery(id+"F8.imprint","IMPRINT",EDGE,{"disambiguationData":[TD([[makeQuery(id+"F8.imprint","INTERSECT",VERTEX,{"derivedFrom":[sQuery(id+"F8.wireOp",EDGE,"E141.MirrorCS"),subQ0]}),1.0]])],"derivedFrom":subQ0})])],"isStart":false});}
            var Q1;
            {var subQ0=sQuery(id+"F8.wireOp",EDGE,"E124");Q1=makeQuery(id+"F16.opExtrude","CAP_EDGE",EDGE,{"disambiguationData":[OSD([subQ0]),TDD([makeQuery(id+"F8.imprint","IMPRINT",EDGE,{"disambiguationData":[TD([[makeQuery(id+"F8.imprint","INTERSECT",VERTEX,{"derivedFrom":[sQuery(id+"F8.wireOp",EDGE,"E140.MirrorCS"),subQ0]}),1.0]])],"derivedFrom":subQ0})])],"isStart":false});}
            var Q2;
            {var subQ0=sQuery(id+"F8.wireOp",EDGE,"E124");Q2=makeQuery(id+"F16.opExtrude","CAP_EDGE",EDGE,{"disambiguationData":[OSD([subQ0]),TDD([makeQuery(id+"F8.imprint","IMPRINT",EDGE,{"disambiguationData":[TD([[makeQuery(id+"F8.imprint","INTERSECT",VERTEX,{"derivedFrom":[sQuery(id+"F8.wireOp",EDGE,"E139.MirrorCS"),subQ0]}),1.0]])],"derivedFrom":subQ0})])],"isStart":false});}
            var Q3;
            {var subQ0=sQuery(id+"F8.wireOp",EDGE,"E124");Q3=makeQuery(id+"F16.opExtrude","CAP_EDGE",EDGE,{"disambiguationData":[OSD([subQ0]),TDD([makeQuery(id+"F8.imprint","IMPRINT",EDGE,{"disambiguationData":[TD([[makeQuery(id+"F8.imprint","INTERSECT",VERTEX,{"derivedFrom":[sQuery(id+"F8.wireOp",EDGE,"E138.MirrorCS"),subQ0]}),1.0]])],"derivedFrom":subQ0})])],"isStart":false});}
            var Q4;
            {var subQ0=sQuery(id+"F8.wireOp",EDGE,"E124");Q4=makeQuery(id+"F16.opExtrude","CAP_EDGE",EDGE,{"disambiguationData":[OSD([subQ0]),TDD([makeQuery(id+"F8.imprint","IMPRINT",EDGE,{"disambiguationData":[TD([[makeQuery(id+"F8.imprint","INTERSECT",VERTEX,{"derivedFrom":[sQuery(id+"F8.wireOp",EDGE,"E137.MirrorCS"),subQ0]}),1.0]])],"derivedFrom":subQ0})])],"isStart":false});}
            var Q5;
            {var subQ0=sQuery(id+"F8.wireOp",EDGE,"E124");Q5=makeQuery(id+"F16.opExtrude","CAP_EDGE",EDGE,{"disambiguationData":[OSD([subQ0]),TDD([makeQuery(id+"F8.imprint","IMPRINT",EDGE,{"disambiguationData":[TD([[makeQuery(id+"F8.imprint","INTERSECT",VERTEX,{"derivedFrom":[sQuery(id+"F8.wireOp",EDGE,"E148"),subQ0]}),1.0]])],"derivedFrom":subQ0})])],"isStart":false});}
            var Q6;
            {var subQ0=sQuery(id+"F8.wireOp",EDGE,"E124");Q6=makeQuery(id+"F16.opExtrude","CAP_EDGE",EDGE,{"disambiguationData":[OSD([subQ0]),TDD([makeQuery(id+"F8.imprint","IMPRINT",EDGE,{"disambiguationData":[TD([[makeQuery(id+"F8.imprint","INTERSECT",VERTEX,{"derivedFrom":[sQuery(id+"F8.wireOp",EDGE,"E147"),subQ0]}),1.0]])],"derivedFrom":subQ0})])],"isStart":false});}
            var Q7;
            {var subQ0=sQuery(id+"F8.wireOp",EDGE,"E124");Q7=makeQuery(id+"F16.opExtrude","CAP_EDGE",EDGE,{"disambiguationData":[OSD([subQ0]),TDD([makeQuery(id+"F8.imprint","IMPRINT",EDGE,{"disambiguationData":[TD([[makeQuery(id+"F8.imprint","INTERSECT",VERTEX,{"derivedFrom":[sQuery(id+"F8.wireOp",EDGE,"E142.MirrorCS"),subQ0]}),1.0]])],"derivedFrom":subQ0})])],"isStart":false});}
            var Q8;
            {var subQ0=sQuery(id+"F8.wireOp",EDGE,"E124");Q8=makeQuery(id+"F16.opExtrude","CAP_EDGE",EDGE,{"disambiguationData":[OSD([subQ0]),TDD([makeQuery(id+"F8.imprint","IMPRINT",EDGE,{"disambiguationData":[TD([[makeQuery(id+"F8.imprint","INTERSECT",VERTEX,{"derivedFrom":[sQuery(id+"F8.wireOp",EDGE,"E143.MirrorCS"),subQ0]}),1.0]])],"derivedFrom":subQ0})])],"isStart":false});}
            var Q9;
            {var subQ0=sQuery(id+"F8.wireOp",EDGE,"E124");Q9=makeQuery(id+"F16.opExtrude","CAP_EDGE",EDGE,{"disambiguationData":[OSD([subQ0]),TDD([makeQuery(id+"F8.imprint","IMPRINT",EDGE,{"disambiguationData":[TD([[makeQuery(id+"F8.imprint","INTERSECT",VERTEX,{"derivedFrom":[sQuery(id+"F8.wireOp",EDGE,"E144.MirrorCS"),subQ0]}),1.0]])],"derivedFrom":subQ0})])],"isStart":false});}
            var Q10;
            {var subQ0=sQuery(id+"F8.wireOp",EDGE,"E124");Q10=makeQuery(id+"F16.opExtrude","CAP_EDGE",EDGE,{"disambiguationData":[OSD([subQ0]),TDD([makeQuery(id+"F8.imprint","IMPRINT",EDGE,{"disambiguationData":[TD([[makeQuery(id+"F8.imprint","INTERSECT",VERTEX,{"derivedFrom":[sQuery(id+"F8.wireOp",EDGE,"E145.MirrorCS"),subQ0]}),1.0]])],"derivedFrom":subQ0})])],"isStart":false});}
            var Q11;
            {var subQ0=sQuery(id+"F8.wireOp",EDGE,"E124");Q11=makeQuery(id+"F16.opExtrude","CAP_EDGE",EDGE,{"disambiguationData":[OSD([subQ0]),TDD([makeQuery(id+"F8.imprint","IMPRINT",EDGE,{"disambiguationData":[TD([[makeQuery(id+"F8.imprint","INTERSECT",VERTEX,{"derivedFrom":[sQuery(id+"F8.wireOp",EDGE,"E146.MirrorCS"),subQ0]}),1.0]])],"derivedFrom":subQ0})])],"isStart":false});}
            var Q12;
            {var subQ0=sQuery(id+"F8.wireOp",EDGE,"E124");Q12=makeQuery(id+"F16.opExtrude","CAP_EDGE",EDGE,{"disambiguationData":[OSD([subQ0]),TDD([makeQuery(id+"F8.imprint","IMPRINT",EDGE,{"disambiguationData":[TD([[makeQuery(id+"F8.imprint","INTERSECT",VERTEX,{"derivedFrom":[sQuery(id+"F8.wireOp",EDGE,"E136"),subQ0]}),1.0]])],"derivedFrom":subQ0})])],"isStart":false});}
            var Q13;
            {var subQ0=sQuery(id+"F8.wireOp",EDGE,"E124");Q13=makeQuery(id+"F16.opExtrude","CAP_EDGE",EDGE,{"disambiguationData":[OSD([subQ0]),TDD([makeQuery(id+"F8.imprint","IMPRINT",EDGE,{"disambiguationData":[TD([[makeQuery(id+"F8.imprint","INTERSECT",VERTEX,{"derivedFrom":[sQuery(id+"F8.wireOp",EDGE,"E135"),subQ0]}),1.0]])],"derivedFrom":subQ0})])],"isStart":false});}
            var Q14;
            {var subQ0=sQuery(id+"F8.wireOp",EDGE,"E124");Q14=makeQuery(id+"F16.opExtrude","CAP_EDGE",EDGE,{"disambiguationData":[OSD([subQ0]),TDD([makeQuery(id+"F8.imprint","IMPRINT",EDGE,{"disambiguationData":[TD([[makeQuery(id+"F8.imprint","INTERSECT",VERTEX,{"derivedFrom":[sQuery(id+"F8.wireOp",EDGE,"E134"),subQ0]}),1.0]])],"derivedFrom":subQ0})])],"isStart":false});}
            var Q15;
            {var subQ0=sQuery(id+"F8.wireOp",EDGE,"E124");Q15=makeQuery(id+"F16.opExtrude","CAP_EDGE",EDGE,{"disambiguationData":[OSD([subQ0]),TDD([makeQuery(id+"F8.imprint","IMPRINT",EDGE,{"disambiguationData":[TD([[makeQuery(id+"F8.imprint","INTERSECT",VERTEX,{"derivedFrom":[sQuery(id+"F8.wireOp",EDGE,"E133"),subQ0]}),1.0]])],"derivedFrom":subQ0})])],"isStart":false});}
            var Q16;
            {var subQ0=sQuery(id+"F8.wireOp",EDGE,"E124");Q16=makeQuery(id+"F16.opExtrude","CAP_EDGE",EDGE,{"disambiguationData":[OSD([subQ0]),TDD([makeQuery(id+"F8.imprint","IMPRINT",EDGE,{"disambiguationData":[TD([[makeQuery(id+"F8.imprint","INTERSECT",VERTEX,{"derivedFrom":[sQuery(id+"F8.wireOp",EDGE,"E132"),subQ0]}),1.0]])],"derivedFrom":subQ0})])],"isStart":false});}
            var Q17;
            {var subQ0=sQuery(id+"F8.wireOp",EDGE,"E124");Q17=makeQuery(id+"F16.opExtrude","CAP_EDGE",EDGE,{"disambiguationData":[OSD([subQ0]),TDD([makeQuery(id+"F8.imprint","IMPRINT",EDGE,{"disambiguationData":[TD([[makeQuery(id+"F8.imprint","INTERSECT",VERTEX,{"derivedFrom":[sQuery(id+"F8.wireOp",EDGE,"E131"),subQ0]}),1.0]])],"derivedFrom":subQ0})])],"isStart":false});}
            var Q18;
            {var subQ0=sQuery(id+"F8.wireOp",EDGE,"E124");Q18=makeQuery(id+"F16.opExtrude","CAP_EDGE",EDGE,{"disambiguationData":[OSD([subQ0]),TDD([makeQuery(id+"F8.imprint","IMPRINT",EDGE,{"disambiguationData":[TD([[makeQuery(id+"F8.imprint","INTERSECT",VERTEX,{"derivedFrom":[sQuery(id+"F8.wireOp",EDGE,"E130"),subQ0]}),1.0]])],"derivedFrom":subQ0})])],"isStart":false});}
            var Q19;
            {var subQ0=sQuery(id+"F8.wireOp",EDGE,"E124");Q19=makeQuery(id+"F16.opExtrude","CAP_EDGE",EDGE,{"disambiguationData":[OSD([subQ0]),TDD([makeQuery(id+"F8.imprint","IMPRINT",EDGE,{"disambiguationData":[TD([[makeQuery(id+"F8.imprint","INTERSECT",VERTEX,{"derivedFrom":[sQuery(id+"F8.wireOp",EDGE,"E129"),subQ0]}),1.0]])],"derivedFrom":subQ0})])],"isStart":false});}
            var Q20;
            {var subQ0=sQuery(id+"F8.wireOp",EDGE,"E124");Q20=makeQuery(id+"F16.opExtrude","CAP_EDGE",EDGE,{"disambiguationData":[OSD([subQ0]),TDD([makeQuery(id+"F8.imprint","IMPRINT",EDGE,{"disambiguationData":[TD([[makeQuery(id+"F8.imprint","INTERSECT",VERTEX,{"derivedFrom":[sQuery(id+"F8.wireOp",EDGE,"E128"),subQ0]}),1.0]])],"derivedFrom":subQ0})])],"isStart":false});}
            var Q21;
            {var subQ0=sQuery(id+"F8.wireOp",EDGE,"E124");Q21=makeQuery(id+"F16.opExtrude","CAP_EDGE",EDGE,{"disambiguationData":[OSD([subQ0]),TDD([makeQuery(id+"F8.imprint","IMPRINT",EDGE,{"disambiguationData":[TD([[makeQuery(id+"F8.imprint","INTERSECT",VERTEX,{"derivedFrom":[sQuery(id+"F8.wireOp",EDGE,"E127"),subQ0]}),1.0]])],"derivedFrom":subQ0})])],"isStart":false});}
            var Q22;
            {var subQ0=sQuery(id+"F8.wireOp",EDGE,"E124");Q22=makeQuery(id+"F16.opExtrude","CAP_EDGE",EDGE,{"disambiguationData":[OSD([subQ0]),TDD([makeQuery(id+"F8.imprint","IMPRINT",EDGE,{"disambiguationData":[TD([[makeQuery(id+"F8.imprint","INTERSECT",VERTEX,{"derivedFrom":[sQuery(id+"F8.wireOp",EDGE,"E126"),subQ0]}),1.0]])],"derivedFrom":subQ0})])],"isStart":false});}
            var Q23;
            {var subQ0=sQuery(id+"F8.wireOp",EDGE,"E124");Q23=makeQuery(id+"F16.opExtrude","CAP_EDGE",EDGE,{"disambiguationData":[OSD([subQ0]),TDD([makeQuery(id+"F8.imprint","IMPRINT",EDGE,{"disambiguationData":[TD([[makeQuery(id+"F8.imprint","INTERSECT",VERTEX,{"derivedFrom":[sQuery(id+"F8.wireOp",EDGE,"E125"),subQ0]}),1.0]])],"derivedFrom":subQ0})])],"isStart":false});}
            fillet(context, id + "F38", {"entities" : qUnion([Q0, Q1, Q2, Q3, Q4, Q5, Q6, Q7, Q8, Q9, Q10, Q11, Q12, Q13, Q14, Q15, Q16, Q17, Q18, Q19, Q20, Q21, Q22, Q23]), "radius" : 3 * mm, "tangentPropagation" : true, "allowEdgeOverflow" : false});
        }
        {
            var Q0;
            {var subQ0=sQuery(id+"F8.wireOp",EDGE,"E124");Q0=makeQuery(id+"F15.opExtrude","CAP_EDGE",EDGE,{"disambiguationData":[OSD([subQ0]),TDD([makeQuery(id+"F8.imprint","IMPRINT",EDGE,{"disambiguationData":[TD([[makeQuery(id+"F8.imprint","INTERSECT",VERTEX,{"derivedFrom":[sQuery(id+"F8.wireOp",EDGE,"E139.MirrorCS"),subQ0]}),-1.0]])],"derivedFrom":subQ0})])],"isStart":false});}
            var Q1;
            {var subQ0=sQuery(id+"F8.wireOp",EDGE,"E124");Q1=makeQuery(id+"F15.opExtrude","CAP_EDGE",EDGE,{"disambiguationData":[OSD([subQ0]),TDD([makeQuery(id+"F8.imprint","IMPRINT",EDGE,{"disambiguationData":[TD([[makeQuery(id+"F8.imprint","INTERSECT",VERTEX,{"derivedFrom":[sQuery(id+"F8.wireOp",EDGE,"E140.MirrorCS"),subQ0]}),-1.0]])],"derivedFrom":subQ0})])],"isStart":false});}
            var Q2;
            {var subQ0=sQuery(id+"F8.wireOp",EDGE,"E124");Q2=makeQuery(id+"F15.opExtrude","CAP_EDGE",EDGE,{"disambiguationData":[OSD([subQ0]),TDD([makeQuery(id+"F8.imprint","IMPRINT",EDGE,{"disambiguationData":[TD([[makeQuery(id+"F8.imprint","INTERSECT",VERTEX,{"derivedFrom":[sQuery(id+"F8.wireOp",EDGE,"E141.MirrorCS"),subQ0]}),-1.0]])],"derivedFrom":subQ0})])],"isStart":false});}
            var Q3;
            {var subQ0=sQuery(id+"F8.wireOp",EDGE,"E124");Q3=makeQuery(id+"F15.opExtrude","CAP_EDGE",EDGE,{"disambiguationData":[OSD([subQ0]),TDD([makeQuery(id+"F8.imprint","IMPRINT",EDGE,{"disambiguationData":[TD([[makeQuery(id+"F8.imprint","INTERSECT",VERTEX,{"derivedFrom":[sQuery(id+"F8.wireOp",EDGE,"E147"),subQ0]}),-1.0]])],"derivedFrom":subQ0})])],"isStart":false});}
            var Q4;
            {var subQ0=sQuery(id+"F8.wireOp",EDGE,"E124");Q4=makeQuery(id+"F15.opExtrude","CAP_EDGE",EDGE,{"disambiguationData":[OSD([subQ0]),TDD([makeQuery(id+"F8.imprint","IMPRINT",EDGE,{"disambiguationData":[TD([[makeQuery(id+"F8.imprint","INTERSECT",VERTEX,{"derivedFrom":[sQuery(id+"F8.wireOp",EDGE,"E142.MirrorCS"),subQ0]}),-1.0]])],"derivedFrom":subQ0})])],"isStart":false});}
            var Q5;
            {var subQ0=sQuery(id+"F8.wireOp",EDGE,"E124");Q5=makeQuery(id+"F15.opExtrude","CAP_EDGE",EDGE,{"disambiguationData":[OSD([subQ0]),TDD([makeQuery(id+"F8.imprint","IMPRINT",EDGE,{"disambiguationData":[TD([[makeQuery(id+"F8.imprint","INTERSECT",VERTEX,{"derivedFrom":[sQuery(id+"F8.wireOp",EDGE,"E138.MirrorCS"),subQ0]}),-1.0]])],"derivedFrom":subQ0})])],"isStart":false});}
            var Q6;
            {var subQ0=sQuery(id+"F8.wireOp",EDGE,"E124");Q6=makeQuery(id+"F15.opExtrude","CAP_EDGE",EDGE,{"disambiguationData":[OSD([subQ0]),TDD([makeQuery(id+"F8.imprint","IMPRINT",EDGE,{"disambiguationData":[TD([[makeQuery(id+"F8.imprint","INTERSECT",VERTEX,{"derivedFrom":[sQuery(id+"F8.wireOp",EDGE,"E137.MirrorCS"),subQ0]}),-1.0]])],"derivedFrom":subQ0})])],"isStart":false});}
            var Q7;
            {var subQ0=sQuery(id+"F8.wireOp",EDGE,"E124");Q7=makeQuery(id+"F15.opExtrude","CAP_EDGE",EDGE,{"disambiguationData":[OSD([subQ0]),TDD([makeQuery(id+"F8.imprint","IMPRINT",EDGE,{"disambiguationData":[TD([[makeQuery(id+"F8.imprint","INTERSECT",VERTEX,{"derivedFrom":[sQuery(id+"F8.wireOp",EDGE,"E148"),subQ0]}),-1.0]])],"derivedFrom":subQ0})])],"isStart":false});}
            var Q8;
            {var subQ0=sQuery(id+"F8.wireOp",EDGE,"E124");Q8=makeQuery(id+"F15.opExtrude","CAP_EDGE",EDGE,{"disambiguationData":[OSD([subQ0]),TDD([makeQuery(id+"F8.imprint","IMPRINT",EDGE,{"disambiguationData":[TD([[makeQuery(id+"F8.imprint","INTERSECT",VERTEX,{"derivedFrom":[sQuery(id+"F8.wireOp",EDGE,"E125"),subQ0]}),-1.0]])],"derivedFrom":subQ0})])],"isStart":false});}
            var Q9;
            {var subQ0=sQuery(id+"F8.wireOp",EDGE,"E124");Q9=makeQuery(id+"F15.opExtrude","CAP_EDGE",EDGE,{"disambiguationData":[OSD([subQ0]),TDD([makeQuery(id+"F8.imprint","IMPRINT",EDGE,{"disambiguationData":[TD([[makeQuery(id+"F8.imprint","INTERSECT",VERTEX,{"derivedFrom":[sQuery(id+"F8.wireOp",EDGE,"E126"),subQ0]}),-1.0]])],"derivedFrom":subQ0})])],"isStart":false});}
            var Q10;
            {var subQ0=sQuery(id+"F8.wireOp",EDGE,"E124");Q10=makeQuery(id+"F15.opExtrude","CAP_EDGE",EDGE,{"disambiguationData":[OSD([subQ0]),TDD([makeQuery(id+"F8.imprint","IMPRINT",EDGE,{"disambiguationData":[TD([[makeQuery(id+"F8.imprint","INTERSECT",VERTEX,{"derivedFrom":[sQuery(id+"F8.wireOp",EDGE,"E143.MirrorCS"),subQ0]}),-1.0]])],"derivedFrom":subQ0})])],"isStart":false});}
            var Q11;
            {var subQ0=sQuery(id+"F8.wireOp",EDGE,"E124");Q11=makeQuery(id+"F15.opExtrude","CAP_EDGE",EDGE,{"disambiguationData":[OSD([subQ0]),TDD([makeQuery(id+"F8.imprint","IMPRINT",EDGE,{"disambiguationData":[TD([[makeQuery(id+"F8.imprint","INTERSECT",VERTEX,{"derivedFrom":[sQuery(id+"F8.wireOp",EDGE,"E144.MirrorCS"),subQ0]}),-1.0]])],"derivedFrom":subQ0})])],"isStart":false});}
            var Q12;
            {var subQ0=sQuery(id+"F8.wireOp",EDGE,"E124");Q12=makeQuery(id+"F15.opExtrude","CAP_EDGE",EDGE,{"disambiguationData":[OSD([subQ0]),TDD([makeQuery(id+"F8.imprint","IMPRINT",EDGE,{"disambiguationData":[TD([[makeQuery(id+"F8.imprint","INTERSECT",VERTEX,{"derivedFrom":[sQuery(id+"F8.wireOp",EDGE,"E145.MirrorCS"),subQ0]}),-1.0]])],"derivedFrom":subQ0})])],"isStart":false});}
            var Q13;
            {var subQ0=sQuery(id+"F8.wireOp",EDGE,"E124");Q13=makeQuery(id+"F15.opExtrude","CAP_EDGE",EDGE,{"disambiguationData":[OSD([subQ0]),TDD([makeQuery(id+"F8.imprint","IMPRINT",EDGE,{"disambiguationData":[TD([[makeQuery(id+"F8.imprint","INTERSECT",VERTEX,{"derivedFrom":[sQuery(id+"F8.wireOp",EDGE,"E146.MirrorCS"),subQ0]}),-1.0]])],"derivedFrom":subQ0})])],"isStart":false});}
            var Q14;
            {var subQ0=sQuery(id+"F8.wireOp",EDGE,"E124");Q14=makeQuery(id+"F15.opExtrude","CAP_EDGE",EDGE,{"disambiguationData":[OSD([subQ0]),TDD([makeQuery(id+"F8.imprint","IMPRINT",EDGE,{"disambiguationData":[TD([[makeQuery(id+"F8.imprint","INTERSECT",VERTEX,{"derivedFrom":[sQuery(id+"F8.wireOp",EDGE,"E136"),subQ0]}),-1.0]])],"derivedFrom":subQ0})])],"isStart":false});}
            var Q15;
            {var subQ0=sQuery(id+"F8.wireOp",EDGE,"E124");Q15=makeQuery(id+"F15.opExtrude","CAP_EDGE",EDGE,{"disambiguationData":[OSD([subQ0]),TDD([makeQuery(id+"F8.imprint","IMPRINT",EDGE,{"disambiguationData":[TD([[makeQuery(id+"F8.imprint","INTERSECT",VERTEX,{"derivedFrom":[sQuery(id+"F8.wireOp",EDGE,"E135"),subQ0]}),-1.0]])],"derivedFrom":subQ0})])],"isStart":false});}
            var Q16;
            {var subQ0=sQuery(id+"F8.wireOp",EDGE,"E124");Q16=makeQuery(id+"F15.opExtrude","CAP_EDGE",EDGE,{"disambiguationData":[OSD([subQ0]),TDD([makeQuery(id+"F8.imprint","IMPRINT",EDGE,{"disambiguationData":[TD([[makeQuery(id+"F8.imprint","INTERSECT",VERTEX,{"derivedFrom":[sQuery(id+"F8.wireOp",EDGE,"E134"),subQ0]}),-1.0]])],"derivedFrom":subQ0})])],"isStart":false});}
            var Q17;
            {var subQ0=sQuery(id+"F8.wireOp",EDGE,"E124");Q17=makeQuery(id+"F15.opExtrude","CAP_EDGE",EDGE,{"disambiguationData":[OSD([subQ0]),TDD([makeQuery(id+"F8.imprint","IMPRINT",EDGE,{"disambiguationData":[TD([[makeQuery(id+"F8.imprint","INTERSECT",VERTEX,{"derivedFrom":[sQuery(id+"F8.wireOp",EDGE,"E133"),subQ0]}),-1.0]])],"derivedFrom":subQ0})])],"isStart":false});}
            var Q18;
            {var subQ0=sQuery(id+"F8.wireOp",EDGE,"E124");Q18=makeQuery(id+"F15.opExtrude","CAP_EDGE",EDGE,{"disambiguationData":[OSD([subQ0]),TDD([makeQuery(id+"F8.imprint","IMPRINT",EDGE,{"disambiguationData":[TD([[makeQuery(id+"F8.imprint","INTERSECT",VERTEX,{"derivedFrom":[sQuery(id+"F8.wireOp",EDGE,"E132"),subQ0]}),-1.0]])],"derivedFrom":subQ0})])],"isStart":false});}
            var Q19;
            {var subQ0=sQuery(id+"F8.wireOp",EDGE,"E124");Q19=makeQuery(id+"F15.opExtrude","CAP_EDGE",EDGE,{"disambiguationData":[OSD([subQ0]),TDD([makeQuery(id+"F8.imprint","IMPRINT",EDGE,{"disambiguationData":[TD([[makeQuery(id+"F8.imprint","INTERSECT",VERTEX,{"derivedFrom":[sQuery(id+"F8.wireOp",EDGE,"E131"),subQ0]}),-1.0]])],"derivedFrom":subQ0})])],"isStart":false});}
            var Q20;
            {var subQ0=sQuery(id+"F8.wireOp",EDGE,"E124");Q20=makeQuery(id+"F15.opExtrude","CAP_EDGE",EDGE,{"disambiguationData":[OSD([subQ0]),TDD([makeQuery(id+"F8.imprint","IMPRINT",EDGE,{"disambiguationData":[TD([[makeQuery(id+"F8.imprint","INTERSECT",VERTEX,{"derivedFrom":[sQuery(id+"F8.wireOp",EDGE,"E130"),subQ0]}),-1.0]])],"derivedFrom":subQ0})])],"isStart":false});}
            var Q21;
            {var subQ0=sQuery(id+"F8.wireOp",EDGE,"E124");Q21=makeQuery(id+"F15.opExtrude","CAP_EDGE",EDGE,{"disambiguationData":[OSD([subQ0]),TDD([makeQuery(id+"F8.imprint","IMPRINT",EDGE,{"disambiguationData":[TD([[makeQuery(id+"F8.imprint","INTERSECT",VERTEX,{"derivedFrom":[sQuery(id+"F8.wireOp",EDGE,"E129"),subQ0]}),-1.0]])],"derivedFrom":subQ0})])],"isStart":false});}
            var Q22;
            {var subQ0=sQuery(id+"F8.wireOp",EDGE,"E124");Q22=makeQuery(id+"F15.opExtrude","CAP_EDGE",EDGE,{"disambiguationData":[OSD([subQ0]),TDD([makeQuery(id+"F8.imprint","IMPRINT",EDGE,{"disambiguationData":[TD([[makeQuery(id+"F8.imprint","INTERSECT",VERTEX,{"derivedFrom":[sQuery(id+"F8.wireOp",EDGE,"E128"),subQ0]}),-1.0]])],"derivedFrom":subQ0})])],"isStart":false});}
            var Q23;
            {var subQ0=sQuery(id+"F8.wireOp",EDGE,"E124");Q23=makeQuery(id+"F15.opExtrude","CAP_EDGE",EDGE,{"disambiguationData":[OSD([subQ0]),TDD([makeQuery(id+"F8.imprint","IMPRINT",EDGE,{"disambiguationData":[TD([[makeQuery(id+"F8.imprint","INTERSECT",VERTEX,{"derivedFrom":[sQuery(id+"F8.wireOp",EDGE,"E127"),subQ0]}),-1.0]])],"derivedFrom":subQ0})])],"isStart":false});}
            fillet(context, id + "F39", {"entities" : qUnion([Q0, Q1, Q2, Q3, Q4, Q5, Q6, Q7, Q8, Q9, Q10, Q11, Q12, Q13, Q14, Q15, Q16, Q17, Q18, Q19, Q20, Q21, Q22, Q23]), "radius" : 2.7 * mm, "tangentPropagation" : true, "allowEdgeOverflow" : false});
        }
        {
            var Q0;
            Q0=makeQuery(id+"F27.imprint","IMPRINT",FACE,{"disambiguationData":[TD([[makeQuery(id+"F27.imprint","IMPRINT",EDGE,{"derivedFrom":sQuery(id+"F27.wireOp",EDGE,"E371")}),1.0]])]});
            extrude(context, id + "F40", {"entities" : qUnion([Q0]), "depth" : 4 * mm});
        }
        {
            var Q0;
            Q0=makeQuery(id+"F27.imprint","IMPRINT",FACE,{"disambiguationData":[TD([[makeQuery(id+"F27.imprint","IMPRINT",EDGE,{"derivedFrom":sQuery(id+"F27.wireOp",EDGE,"E371")}),1.0]])]});
            var Q1;
            Q1=makeQuery(id+"F27.imprint","IMPRINT",FACE,{"disambiguationData":[TD([[makeQuery(id+"F27.imprint","IMPRINT",EDGE,{"derivedFrom":sQuery(id+"F27.wireOp",EDGE,"E371")}),-1.0]])]});
            extrude(context, id + "F41", {"entities" : qUnion([Q0, Q1]), "operationType" : NewBodyOperationType.ADD, "oppositeDirection" : true, "depth" : 1.5 * mm});
        }
    });
